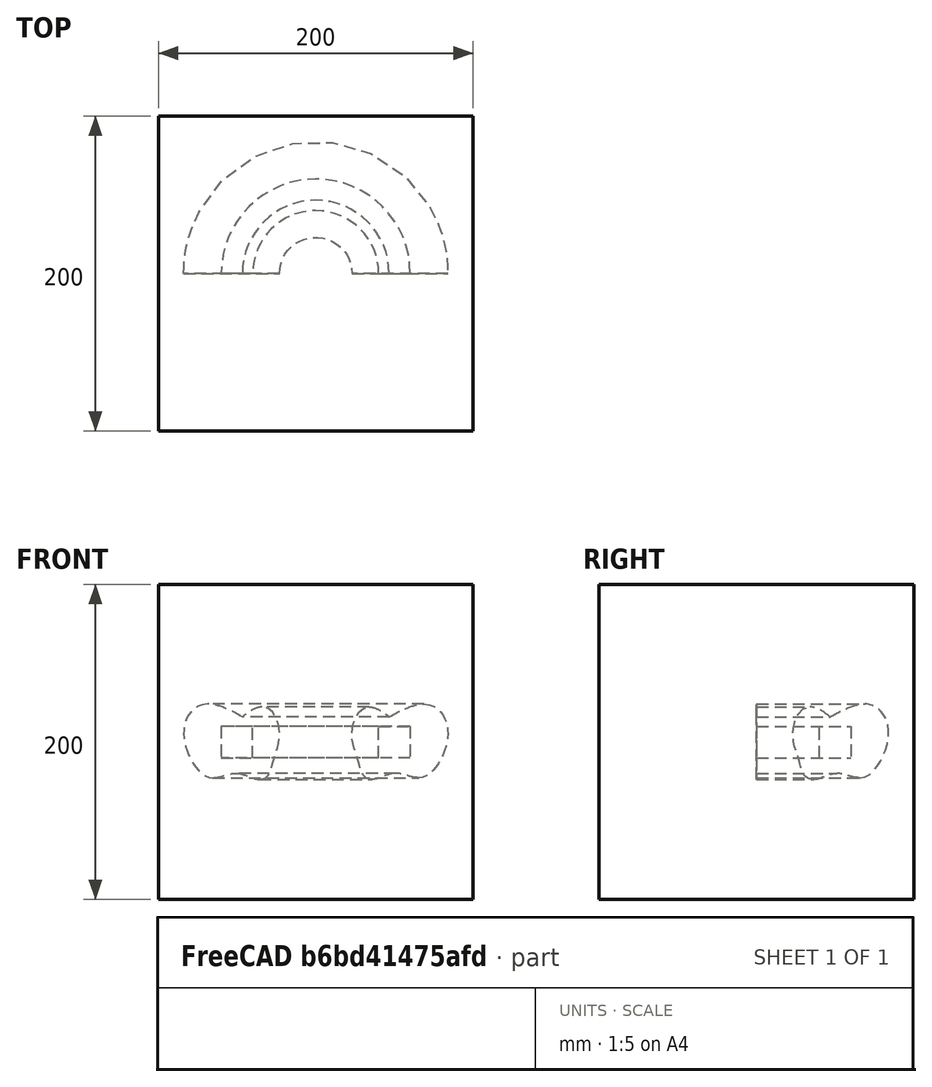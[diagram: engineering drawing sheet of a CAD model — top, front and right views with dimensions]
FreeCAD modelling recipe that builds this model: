
FCSTD DOCUMENT  (FreeCAD 0.21R33694 (Git))
Label: revolve
License: All rights reserved
LicenseURL: http://en.wikipedia.org/wiki/All_rights_reserved
objects: App::DocumentObjectGroupPython×1248, App::Part×2, Part::FeaturePython×1, Sketcher::SketchObject×1, Part::Revolution×1
note: 3 computed .brp shape members not serialized (recipe doc carries the construction recipe); baked Part::Feature solids carry a one-line shape summary decoded from their .brp

FEATURE [App::DocumentObjectGroupPython] HALFPI  # scripted group (container) (typed FeaturePython)
  name = HALFPI
  value = pi/2.
FEATURE [App::DocumentObjectGroupPython] PI  # scripted group (container) (typed FeaturePython)
  name = PI
  value = 1.*pi
FEATURE [App::DocumentObjectGroupPython] TWOPI  # scripted group (container) (typed FeaturePython)
  name = TWOPI
  value = 2.*pi
FEATURE [App::DocumentObjectGroupPython] Constants  # scripted group (container) (typed FeaturePython)
  Group = -> [HALFPI,PI,TWOPI]
FEATURE [App::DocumentObjectGroupPython] Variables  # scripted group (container) (typed FeaturePython)
FEATURE [App::DocumentObjectGroupPython] Quantities  # scripted group (container) (typed FeaturePython)
FEATURE [App::DocumentObjectGroupPython] Isotopes  # scripted group (container) (typed FeaturePython)
FEATURE [App::DocumentObjectGroupPython] Elements  # scripted group (container) (typed FeaturePython)
FEATURE [App::DocumentObjectGroupPython] G4Isotopes  # scripted group (container) (typed FeaturePython)
FEATURE [App::DocumentObjectGroupPython] H_element  # scripted group (container) (typed FeaturePython)
  Z = 1
  atom_value = 1.008
  formula = H
  name = H_element
FEATURE [App::DocumentObjectGroupPython] He_element  # scripted group (container) (typed FeaturePython)
  Z = 2
  atom_value = 4.0026
  formula = He
  name = He_element
FEATURE [App::DocumentObjectGroupPython] Li_element  # scripted group (container) (typed FeaturePython)
  Z = 3
  atom_value = 6.94
  formula = Li
  name = Li_element
FEATURE [App::DocumentObjectGroupPython] Be_element  # scripted group (container) (typed FeaturePython)
  Z = 4
  atom_value = 9.01218
  formula = Be
  name = Be_element
FEATURE [App::DocumentObjectGroupPython] B_element  # scripted group (container) (typed FeaturePython)
  Z = 5
  atom_value = 10.81
  formula = B
  name = B_element
FEATURE [App::DocumentObjectGroupPython] C_element  # scripted group (container) (typed FeaturePython)
  Z = 6
  atom_value = 12.011
  formula = C
  name = C_element
FEATURE [App::DocumentObjectGroupPython] N_element  # scripted group (container) (typed FeaturePython)
  Z = 7
  atom_value = 14.007
  formula = N
  name = N_element
FEATURE [App::DocumentObjectGroupPython] O_element  # scripted group (container) (typed FeaturePython)
  Z = 8
  atom_value = 15.999
  formula = O
  name = O_element
FEATURE [App::DocumentObjectGroupPython] F_element  # scripted group (container) (typed FeaturePython)
  Z = 9
  atom_value = 18.9984
  formula = F
  name = F_element
FEATURE [App::DocumentObjectGroupPython] Ne_element  # scripted group (container) (typed FeaturePython)
  Z = 10
  atom_value = 20.1797
  formula = Ne
  name = Ne_element
FEATURE [App::DocumentObjectGroupPython] Na_element  # scripted group (container) (typed FeaturePython)
  Z = 11
  atom_value = 22.9898
  formula = Na
  name = Na_element
FEATURE [App::DocumentObjectGroupPython] Mg_element  # scripted group (container) (typed FeaturePython)
  Z = 12
  atom_value = 24.305
  formula = Mg
  name = Mg_element
FEATURE [App::DocumentObjectGroupPython] Al_element  # scripted group (container) (typed FeaturePython)
  Z = 13
  atom_value = 26.9815
  formula = Al
  name = Al_element
FEATURE [App::DocumentObjectGroupPython] Si_element  # scripted group (container) (typed FeaturePython)
  Z = 14
  atom_value = 28.085
  formula = Si
  name = Si_element
FEATURE [App::DocumentObjectGroupPython] P_element  # scripted group (container) (typed FeaturePython)
  Z = 15
  atom_value = 30.9738
  formula = P
  name = P_element
FEATURE [App::DocumentObjectGroupPython] S_element  # scripted group (container) (typed FeaturePython)
  Z = 16
  atom_value = 32.06
  formula = S
  name = S_element
FEATURE [App::DocumentObjectGroupPython] Cl_element  # scripted group (container) (typed FeaturePython)
  Z = 17
  atom_value = 35.45
  formula = Cl
  name = Cl_element
FEATURE [App::DocumentObjectGroupPython] Ar_element  # scripted group (container) (typed FeaturePython)
  Z = 18
  atom_value = 39.95
  formula = Ar
  name = Ar_element
FEATURE [App::DocumentObjectGroupPython] K_element  # scripted group (container) (typed FeaturePython)
  Z = 19
  atom_value = 39.0983
  formula = K
  name = K_element
FEATURE [App::DocumentObjectGroupPython] Ca_element  # scripted group (container) (typed FeaturePython)
  Z = 20
  atom_value = 40.078
  formula = Ca
  name = Ca_element
FEATURE [App::DocumentObjectGroupPython] Sc_element  # scripted group (container) (typed FeaturePython)
  Z = 21
  atom_value = 44.9559
  formula = Sc
  name = Sc_element
FEATURE [App::DocumentObjectGroupPython] Ti_element  # scripted group (container) (typed FeaturePython)
  Z = 22
  atom_value = 47.867
  formula = Ti
  name = Ti_element
FEATURE [App::DocumentObjectGroupPython] V_element  # scripted group (container) (typed FeaturePython)
  Z = 23
  atom_value = 50.9415
  formula = V
  name = V_element
FEATURE [App::DocumentObjectGroupPython] Cr_element  # scripted group (container) (typed FeaturePython)
  Z = 24
  atom_value = 51.9961
  formula = Cr
  name = Cr_element
FEATURE [App::DocumentObjectGroupPython] Mn_element  # scripted group (container) (typed FeaturePython)
  Z = 25
  atom_value = 54.938
  formula = Mn
  name = Mn_element
FEATURE [App::DocumentObjectGroupPython] Fe_element  # scripted group (container) (typed FeaturePython)
  Z = 26
  atom_value = 55.845
  formula = Fe
  name = Fe_element
FEATURE [App::DocumentObjectGroupPython] Co_element  # scripted group (container) (typed FeaturePython)
  Z = 27
  atom_value = 58.9332
  formula = Co
  name = Co_element
FEATURE [App::DocumentObjectGroupPython] Ni_element  # scripted group (container) (typed FeaturePython)
  Z = 28
  atom_value = 58.6934
  formula = Ni
  name = Ni_element
FEATURE [App::DocumentObjectGroupPython] Cu_element  # scripted group (container) (typed FeaturePython)
  Z = 29
  atom_value = 63.546
  formula = Cu
  name = Cu_element
FEATURE [App::DocumentObjectGroupPython] Zn_element  # scripted group (container) (typed FeaturePython)
  Z = 30
  atom_value = 65.38
  formula = Zn
  name = Zn_element
FEATURE [App::DocumentObjectGroupPython] Ga_element  # scripted group (container) (typed FeaturePython)
  Z = 31
  atom_value = 69.723
  formula = Ga
  name = Ga_element
FEATURE [App::DocumentObjectGroupPython] Ge_element  # scripted group (container) (typed FeaturePython)
  Z = 32
  atom_value = 72.63
  formula = Ge
  name = Ge_element
FEATURE [App::DocumentObjectGroupPython] As_element  # scripted group (container) (typed FeaturePython)
  Z = 33
  atom_value = 74.9216
  formula = As
  name = As_element
FEATURE [App::DocumentObjectGroupPython] Se_element  # scripted group (container) (typed FeaturePython)
  Z = 34
  atom_value = 78.971
  formula = Se
  name = Se_element
FEATURE [App::DocumentObjectGroupPython] Br_element  # scripted group (container) (typed FeaturePython)
  Z = 35
  atom_value = 79.904
  formula = Br
  name = Br_element
FEATURE [App::DocumentObjectGroupPython] Kr_element  # scripted group (container) (typed FeaturePython)
  Z = 36
  atom_value = 83.798
  formula = Kr
  name = Kr_element
FEATURE [App::DocumentObjectGroupPython] Rb_element  # scripted group (container) (typed FeaturePython)
  Z = 37
  atom_value = 85.4678
  formula = Rb
  name = Rb_element
FEATURE [App::DocumentObjectGroupPython] Sr_element  # scripted group (container) (typed FeaturePython)
  Z = 38
  atom_value = 87.62
  formula = Sr
  name = Sr_element
FEATURE [App::DocumentObjectGroupPython] Y_element  # scripted group (container) (typed FeaturePython)
  Z = 39
  atom_value = 88.9058
  formula = Y
  name = Y_element
FEATURE [App::DocumentObjectGroupPython] Zr_element  # scripted group (container) (typed FeaturePython)
  Z = 40
  atom_value = 91.224
  formula = Zr
  name = Zr_element
FEATURE [App::DocumentObjectGroupPython] Nb_element  # scripted group (container) (typed FeaturePython)
  Z = 41
  atom_value = 92.9064
  formula = Nb
  name = Nb_element
FEATURE [App::DocumentObjectGroupPython] Mo_element  # scripted group (container) (typed FeaturePython)
  Z = 42
  atom_value = 95.95
  formula = Mo
  name = Mo_element
FEATURE [App::DocumentObjectGroupPython] Tc_element  # scripted group (container) (typed FeaturePython)
  Z = 43
  atom_value = 97
  formula = Tc
  name = Tc_element
FEATURE [App::DocumentObjectGroupPython] Ru_element  # scripted group (container) (typed FeaturePython)
  Z = 44
  atom_value = 101.07
  formula = Ru
  name = Ru_element
FEATURE [App::DocumentObjectGroupPython] Rh_element  # scripted group (container) (typed FeaturePython)
  Z = 45
  atom_value = 102.905
  formula = Rh
  name = Rh_element
FEATURE [App::DocumentObjectGroupPython] Pd_element  # scripted group (container) (typed FeaturePython)
  Z = 46
  atom_value = 106.42
  formula = Pd
  name = Pd_element
FEATURE [App::DocumentObjectGroupPython] Ag_element  # scripted group (container) (typed FeaturePython)
  Z = 47
  atom_value = 107.868
  formula = Ag
  name = Ag_element
FEATURE [App::DocumentObjectGroupPython] Cd_element  # scripted group (container) (typed FeaturePython)
  Z = 48
  atom_value = 112.414
  formula = Cd
  name = Cd_element
FEATURE [App::DocumentObjectGroupPython] In_element  # scripted group (container) (typed FeaturePython)
  Z = 49
  atom_value = 114.818
  formula = In
  name = In_element
FEATURE [App::DocumentObjectGroupPython] Sn_element  # scripted group (container) (typed FeaturePython)
  Z = 50
  atom_value = 118.71
  formula = Sn
  name = Sn_element
FEATURE [App::DocumentObjectGroupPython] Sb_element  # scripted group (container) (typed FeaturePython)
  Z = 51
  atom_value = 121.76
  formula = Sb
  name = Sb_element
FEATURE [App::DocumentObjectGroupPython] Te_element  # scripted group (container) (typed FeaturePython)
  Z = 52
  atom_value = 127.6
  formula = Te
  name = Te_element
FEATURE [App::DocumentObjectGroupPython] I_element  # scripted group (container) (typed FeaturePython)
  Z = 53
  atom_value = 126.904
  formula = I
  name = I_element
FEATURE [App::DocumentObjectGroupPython] Xe_element  # scripted group (container) (typed FeaturePython)
  Z = 54
  atom_value = 131.293
  formula = Xe
  name = Xe_element
FEATURE [App::DocumentObjectGroupPython] Cs_element  # scripted group (container) (typed FeaturePython)
  Z = 55
  atom_value = 132.905
  formula = Cs
  name = Cs_element
FEATURE [App::DocumentObjectGroupPython] Ba_element  # scripted group (container) (typed FeaturePython)
  Z = 56
  atom_value = 137.327
  formula = Ba
  name = Ba_element
FEATURE [App::DocumentObjectGroupPython] La_element  # scripted group (container) (typed FeaturePython)
  Z = 57
  atom_value = 138.905
  formula = La
  name = La_element
FEATURE [App::DocumentObjectGroupPython] Ce_element  # scripted group (container) (typed FeaturePython)
  Z = 58
  atom_value = 140.116
  formula = Ce
  name = Ce_element
FEATURE [App::DocumentObjectGroupPython] Pr_element  # scripted group (container) (typed FeaturePython)
  Z = 59
  atom_value = 140.908
  formula = Pr
  name = Pr_element
FEATURE [App::DocumentObjectGroupPython] Nd_element  # scripted group (container) (typed FeaturePython)
  Z = 60
  atom_value = 144.242
  formula = Nd
  name = Nd_element
FEATURE [App::DocumentObjectGroupPython] Pm_element  # scripted group (container) (typed FeaturePython)
  Z = 61
  atom_value = 145
  formula = Pm
  name = Pm_element
FEATURE [App::DocumentObjectGroupPython] Sm_element  # scripted group (container) (typed FeaturePython)
  Z = 62
  atom_value = 150.36
  formula = Sm
  name = Sm_element
FEATURE [App::DocumentObjectGroupPython] Eu_element  # scripted group (container) (typed FeaturePython)
  Z = 63
  atom_value = 151.964
  formula = Eu
  name = Eu_element
FEATURE [App::DocumentObjectGroupPython] Gd_element  # scripted group (container) (typed FeaturePython)
  Z = 64
  atom_value = 157.25
  formula = Gd
  name = Gd_element
FEATURE [App::DocumentObjectGroupPython] Tb_element  # scripted group (container) (typed FeaturePython)
  Z = 65
  atom_value = 158.925
  formula = Tb
  name = Tb_element
FEATURE [App::DocumentObjectGroupPython] Dy_element  # scripted group (container) (typed FeaturePython)
  Z = 66
  atom_value = 162.5
  formula = Dy
  name = Dy_element
FEATURE [App::DocumentObjectGroupPython] Ho_element  # scripted group (container) (typed FeaturePython)
  Z = 67
  atom_value = 164.93
  formula = Ho
  name = Ho_element
FEATURE [App::DocumentObjectGroupPython] Er_element  # scripted group (container) (typed FeaturePython)
  Z = 68
  atom_value = 167.259
  formula = Er
  name = Er_element
FEATURE [App::DocumentObjectGroupPython] Tm_element  # scripted group (container) (typed FeaturePython)
  Z = 69
  atom_value = 168.934
  formula = Tm
  name = Tm_element
FEATURE [App::DocumentObjectGroupPython] Yb_element  # scripted group (container) (typed FeaturePython)
  Z = 70
  atom_value = 173.045
  formula = Yb
  name = Yb_element
FEATURE [App::DocumentObjectGroupPython] Lu_element  # scripted group (container) (typed FeaturePython)
  Z = 71
  atom_value = 174.967
  formula = Lu
  name = Lu_element
FEATURE [App::DocumentObjectGroupPython] Hf_element  # scripted group (container) (typed FeaturePython)
  Z = 72
  atom_value = 178.49
  formula = Hf
  name = Hf_element
FEATURE [App::DocumentObjectGroupPython] Ta_element  # scripted group (container) (typed FeaturePython)
  Z = 73
  atom_value = 180.948
  formula = Ta
  name = Ta_element
FEATURE [App::DocumentObjectGroupPython] W_element  # scripted group (container) (typed FeaturePython)
  Z = 74
  atom_value = 183.84
  formula = W
  name = W_element
FEATURE [App::DocumentObjectGroupPython] Re_element  # scripted group (container) (typed FeaturePython)
  Z = 75
  atom_value = 186.207
  formula = Re
  name = Re_element
FEATURE [App::DocumentObjectGroupPython] Os_element  # scripted group (container) (typed FeaturePython)
  Z = 76
  atom_value = 190.23
  formula = Os
  name = Os_element
FEATURE [App::DocumentObjectGroupPython] Ir_element  # scripted group (container) (typed FeaturePython)
  Z = 77
  atom_value = 192.217
  formula = Ir
  name = Ir_element
FEATURE [App::DocumentObjectGroupPython] Pt_element  # scripted group (container) (typed FeaturePython)
  Z = 78
  atom_value = 195.084
  formula = Pt
  name = Pt_element
FEATURE [App::DocumentObjectGroupPython] Au_element  # scripted group (container) (typed FeaturePython)
  Z = 79
  atom_value = 196.967
  formula = Au
  name = Au_element
FEATURE [App::DocumentObjectGroupPython] Hg_element  # scripted group (container) (typed FeaturePython)
  Z = 80
  atom_value = 200.592
  formula = Hg
  name = Hg_element
FEATURE [App::DocumentObjectGroupPython] Tl_element  # scripted group (container) (typed FeaturePython)
  Z = 81
  atom_value = 204.38
  formula = Tl
  name = Tl_element
FEATURE [App::DocumentObjectGroupPython] Pb_element  # scripted group (container) (typed FeaturePython)
  Z = 82
  atom_value = 207.2
  formula = Pb
  name = Pb_element
FEATURE [App::DocumentObjectGroupPython] Bi_element  # scripted group (container) (typed FeaturePython)
  Z = 83
  atom_value = 208.98
  formula = Bi
  name = Bi_element
FEATURE [App::DocumentObjectGroupPython] Po_element  # scripted group (container) (typed FeaturePython)
  Z = 84
  atom_value = 209
  formula = Po
  name = Po_element
FEATURE [App::DocumentObjectGroupPython] At_element  # scripted group (container) (typed FeaturePython)
  Z = 85
  atom_value = 210
  formula = At
  name = At_element
FEATURE [App::DocumentObjectGroupPython] Rn_element  # scripted group (container) (typed FeaturePython)
  Z = 86
  atom_value = 222
  formula = Rn
  name = Rn_element
FEATURE [App::DocumentObjectGroupPython] Fr_element  # scripted group (container) (typed FeaturePython)
  Z = 87
  atom_value = 223
  formula = Fr
  name = Fr_element
FEATURE [App::DocumentObjectGroupPython] Ra_element  # scripted group (container) (typed FeaturePython)
  Z = 88
  atom_value = 226
  formula = Ra
  name = Ra_element
FEATURE [App::DocumentObjectGroupPython] Ac_element  # scripted group (container) (typed FeaturePython)
  Z = 89
  atom_value = 227
  formula = Ac
  name = Ac_element
FEATURE [App::DocumentObjectGroupPython] Th_element  # scripted group (container) (typed FeaturePython)
  Z = 90
  atom_value = 232.038
  formula = Th
  name = Th_element
FEATURE [App::DocumentObjectGroupPython] Pa_element  # scripted group (container) (typed FeaturePython)
  Z = 91
  atom_value = 231.036
  formula = Pa
  name = Pa_element
FEATURE [App::DocumentObjectGroupPython] U_element  # scripted group (container) (typed FeaturePython)
  Z = 92
  atom_value = 238.029
  formula = U
  name = U_element
FEATURE [App::DocumentObjectGroupPython] Np_element  # scripted group (container) (typed FeaturePython)
  Z = 93
  atom_value = 237
  formula = Np
  name = Np_element
FEATURE [App::DocumentObjectGroupPython] Pu_element  # scripted group (container) (typed FeaturePython)
  Z = 94
  atom_value = 244
  formula = Pu
  name = Pu_element
FEATURE [App::DocumentObjectGroupPython] Am_element  # scripted group (container) (typed FeaturePython)
  Z = 95
  atom_value = 243
  formula = Am
  name = Am_element
FEATURE [App::DocumentObjectGroupPython] Cm_element  # scripted group (container) (typed FeaturePython)
  Z = 96
  atom_value = 247
  formula = Cm
  name = Cm_element
FEATURE [App::DocumentObjectGroupPython] Bk_element  # scripted group (container) (typed FeaturePython)
  Z = 97
  atom_value = 247
  formula = Bk
  name = Bk_element
FEATURE [App::DocumentObjectGroupPython] Cf_element  # scripted group (container) (typed FeaturePython)
  Z = 98
  atom_value = 251
  formula = Cf
  name = Cf_element
FEATURE [App::DocumentObjectGroupPython] G4Elements  # scripted group (container) (typed FeaturePython)
  Group = -> [H_element,He_element,Li_element,Be_element,B_element,C_element,N_element,O_element,F_element,Ne_element,Na_element,Mg_element,Al_element,Si_element,P_element,S_element,Cl_element,Ar_element,K_element,Ca_element,Sc_element,Ti_element,V_element,Cr_element,Mn_element,Fe_element,Co_element,Ni_element,Cu_element,Zn_element,Ga_element,Ge_element,As_element,Se_element,Br_element,Kr_element,Rb_element,+61 more]
FEATURE [App::DocumentObjectGroupPython] H_element001  label="H_element : 0.101"  # scripted group (container) (typed FeaturePython)
  n = 0.101327
FEATURE [App::DocumentObjectGroupPython] C_element001  label="C_element : 0.775"  # scripted group (container) (typed FeaturePython)
  n = 0.7755
FEATURE [App::DocumentObjectGroupPython] N_element001  label="N_element : 0.035"  # scripted group (container) (typed FeaturePython)
  n = 0.035057
FEATURE [App::DocumentObjectGroupPython] O_element001  label="O_element : 0.052"  # scripted group (container) (typed FeaturePython)
  n = 0.0523159
FEATURE [App::DocumentObjectGroupPython] F_element001  label="F_element : 0.017"  # scripted group (container) (typed FeaturePython)
  n = 0.017422
FEATURE [App::DocumentObjectGroupPython] Ca_element001  label="Ca_element : 0.018"  # scripted group (container) (typed FeaturePython)
  n = 0.018378
FEATURE [App::DocumentObjectGroupPython] G4_A_150_TISSUE  label="G4_A-150_TISSUE"  # scripted group (container) (typed FeaturePython)
  Dunit = g/cm3
  Dvalue = 1.127
  Group = -> [H_element001,C_element001,N_element001,O_element001,F_element001,Ca_element001]
  conduct = 2
  density = 1
  expand = 3
  formula = G4_A-150_TISSUE
  name = G4_A-150_TISSUE
  specific = 4
FEATURE [App::DocumentObjectGroupPython] C_element002  label="C_element : 3"  # scripted group (container) (typed FeaturePython)
  n = 3
  ref = C_element
FEATURE [App::DocumentObjectGroupPython] H_element002  label="H_element : 6"  # scripted group (container) (typed FeaturePython)
  n = 6
  ref = H_element
FEATURE [App::DocumentObjectGroupPython] O_element002  label="O_element : 1"  # scripted group (container) (typed FeaturePython)
  n = 1
  ref = O_element
FEATURE [App::DocumentObjectGroupPython] G4_ACETONE  # scripted group (container) (typed FeaturePython)
  Dunit = g/cm3
  Dvalue = 0.7899
  Group = -> [C_element002,H_element002,O_element002]
  conduct = 2
  density = 1
  expand = 3
  formula = G4_ACETONE
  name = G4_ACETONE
  specific = 4
FEATURE [App::DocumentObjectGroupPython] C_element003  label="C_element : 2"  # scripted group (container) (typed FeaturePython)
  n = 2
  ref = C_element
FEATURE [App::DocumentObjectGroupPython] H_element003  label="H_element : 2"  # scripted group (container) (typed FeaturePython)
  n = 2
  ref = H_element
FEATURE [App::DocumentObjectGroupPython] G4_ACETYLENE  # scripted group (container) (typed FeaturePython)
  Dunit = g/cm3
  Dvalue = 0.0010967
  Group = -> [C_element003,H_element003]
  conduct = 2
  density = 1
  expand = 3
  formula = G4_ACETYLENE
  name = G4_ACETYLENE
  specific = 4
FEATURE [App::DocumentObjectGroupPython] C_element004  label="C_element : 5"  # scripted group (container) (typed FeaturePython)
  n = 5
  ref = C_element
FEATURE [App::DocumentObjectGroupPython] H_element004  label="H_element : 5"  # scripted group (container) (typed FeaturePython)
  n = 5
  ref = H_element
FEATURE [App::DocumentObjectGroupPython] N_element002  label="N_element : 5"  # scripted group (container) (typed FeaturePython)
  n = 5
  ref = N_element
FEATURE [App::DocumentObjectGroupPython] G4_ADENINE  # scripted group (container) (typed FeaturePython)
  Dunit = g/cm3
  Dvalue = 1.6
  Group = -> [C_element004,H_element004,N_element002]
  conduct = 2
  density = 1
  expand = 3
  formula = G4_ADENINE
  name = G4_ADENINE
  specific = 4
FEATURE [App::DocumentObjectGroupPython] H_element005  label="H_element : 0.114"  # scripted group (container) (typed FeaturePython)
  n = 0.114
FEATURE [App::DocumentObjectGroupPython] C_element005  label="C_element : 0.598"  # scripted group (container) (typed FeaturePython)
  n = 0.598
FEATURE [App::DocumentObjectGroupPython] N_element003  label="N_element : 0.007"  # scripted group (container) (typed FeaturePython)
  n = 0.007
FEATURE [App::DocumentObjectGroupPython] O_element003  label="O_element : 0.278"  # scripted group (container) (typed FeaturePython)
  n = 0.278
FEATURE [App::DocumentObjectGroupPython] Na_element001  label="Na_element : 0.001"  # scripted group (container) (typed FeaturePython)
  n = 0.001
FEATURE [App::DocumentObjectGroupPython] S_element001  label="S_element : 0.001"  # scripted group (container) (typed FeaturePython)
  n = 0.001
FEATURE [App::DocumentObjectGroupPython] Cl_element001  label="Cl_element : 0.001"  # scripted group (container) (typed FeaturePython)
  n = 0.001
FEATURE [App::DocumentObjectGroupPython] G4_ADIPOSE_TISSUE_ICRP  # scripted group (container) (typed FeaturePython)
  Dunit = g/cm3
  Dvalue = 0.95
  Group = -> [H_element005,C_element005,N_element003,O_element003,Na_element001,S_element001,Cl_element001]
  conduct = 2
  density = 1
  expand = 3
  formula = G4_ADIPOSE_TISSUE_ICRP
  name = G4_ADIPOSE_TISSUE_ICRP
  specific = 4
FEATURE [App::DocumentObjectGroupPython] C_element006  label="C_element : 0.000"  # scripted group (container) (typed FeaturePython)
  n = 0.000124
FEATURE [App::DocumentObjectGroupPython] N_element004  label="N_element : 0.755"  # scripted group (container) (typed FeaturePython)
  n = 0.755268
FEATURE [App::DocumentObjectGroupPython] O_element004  label="O_element : 0.232"  # scripted group (container) (typed FeaturePython)
  n = 0.231781
FEATURE [App::DocumentObjectGroupPython] Ar_element001  label="Ar_element : 0.013"  # scripted group (container) (typed FeaturePython)
  n = 0.012827
FEATURE [App::DocumentObjectGroupPython] G4_AIR  # scripted group (container) (typed FeaturePython)
  Dunit = g/cm3
  Dvalue = 0.00120479
  Group = -> [C_element006,N_element004,O_element004,Ar_element001]
  conduct = 2
  density = 1
  expand = 3
  formula = G4_AIR
  name = G4_AIR
  specific = 4
FEATURE [App::DocumentObjectGroupPython] C_element007  label="C_element : 006"  # scripted group (container) (typed FeaturePython)
  n = 3
  ref = C_element
FEATURE [App::DocumentObjectGroupPython] H_element006  label="H_element : 7"  # scripted group (container) (typed FeaturePython)
  n = 7
  ref = H_element
FEATURE [App::DocumentObjectGroupPython] N_element005  label="N_element : 1"  # scripted group (container) (typed FeaturePython)
  n = 1
  ref = N_element
FEATURE [App::DocumentObjectGroupPython] O_element005  label="O_element : 2"  # scripted group (container) (typed FeaturePython)
  n = 2
  ref = O_element
FEATURE [App::DocumentObjectGroupPython] G4_ALANINE  # scripted group (container) (typed FeaturePython)
  Dunit = g/cm3
  Dvalue = 1.42
  Group = -> [C_element007,H_element006,N_element005,O_element005]
  conduct = 2
  density = 1
  expand = 3
  formula = G4_ALANINE
  name = G4_ALANINE
  specific = 4
FEATURE [App::DocumentObjectGroupPython] Al_element001  label="Al_element : 2"  # scripted group (container) (typed FeaturePython)
  n = 2
  ref = Al_element
FEATURE [App::DocumentObjectGroupPython] O_element006  label="O_element : 3"  # scripted group (container) (typed FeaturePython)
  n = 3
  ref = O_element
FEATURE [App::DocumentObjectGroupPython] G4_ALUMINUM_OXIDE  # scripted group (container) (typed FeaturePython)
  Dunit = g/cm3
  Dvalue = 3.97
  Group = -> [Al_element001,O_element006]
  conduct = 2
  density = 1
  expand = 3
  formula = G4_ALUMINUM_OXIDE
  name = G4_ALUMINUM_OXIDE
  specific = 4
FEATURE [App::DocumentObjectGroupPython] H_element007  label="H_element : 0.106"  # scripted group (container) (typed FeaturePython)
  n = 0.10593
FEATURE [App::DocumentObjectGroupPython] C_element008  label="C_element : 0.789"  # scripted group (container) (typed FeaturePython)
  n = 0.788974
FEATURE [App::DocumentObjectGroupPython] O_element007  label="O_element : 0.105"  # scripted group (container) (typed FeaturePython)
  n = 0.105096
FEATURE [App::DocumentObjectGroupPython] G4_AMBER  # scripted group (container) (typed FeaturePython)
  Dunit = g/cm3
  Dvalue = 1.1
  Group = -> [H_element007,C_element008,O_element007]
  conduct = 2
  density = 1
  expand = 3
  formula = G4_AMBER
  name = G4_AMBER
  specific = 4
FEATURE [App::DocumentObjectGroupPython] N_element006  label="N_element : 006"  # scripted group (container) (typed FeaturePython)
  n = 1
  ref = N_element
FEATURE [App::DocumentObjectGroupPython] H_element008  label="H_element : 3"  # scripted group (container) (typed FeaturePython)
  n = 3
  ref = H_element
FEATURE [App::DocumentObjectGroupPython] G4_AMMONIA  # scripted group (container) (typed FeaturePython)
  Dunit = g/cm3
  Dvalue = 0.000826019
  Group = -> [N_element006,H_element008]
  conduct = 2
  density = 1
  expand = 3
  formula = G4_AMMONIA
  name = G4_AMMONIA
  specific = 4
FEATURE [App::DocumentObjectGroupPython] C_element009  label="C_element : 6"  # scripted group (container) (typed FeaturePython)
  n = 6
  ref = C_element
FEATURE [App::DocumentObjectGroupPython] H_element009  label="H_element : 008"  # scripted group (container) (typed FeaturePython)
  n = 7
  ref = H_element
FEATURE [App::DocumentObjectGroupPython] N_element007  label="N_element : 007"  # scripted group (container) (typed FeaturePython)
  n = 1
  ref = N_element
FEATURE [App::DocumentObjectGroupPython] G4_ANILINE  # scripted group (container) (typed FeaturePython)
  Dunit = g/cm3
  Dvalue = 1.0235
  Group = -> [C_element009,H_element009,N_element007]
  conduct = 2
  density = 1
  expand = 3
  formula = G4_ANILINE
  name = G4_ANILINE
  specific = 4
FEATURE [App::DocumentObjectGroupPython] C_element010  label="C_element : 14"  # scripted group (container) (typed FeaturePython)
  n = 14
  ref = C_element
FEATURE [App::DocumentObjectGroupPython] H_element010  label="H_element : 10"  # scripted group (container) (typed FeaturePython)
  n = 10
  ref = H_element
FEATURE [App::DocumentObjectGroupPython] G4_ANTHRACENE  # scripted group (container) (typed FeaturePython)
  Dunit = g/cm3
  Dvalue = 1.283
  Group = -> [C_element010,H_element010]
  conduct = 2
  density = 1
  expand = 3
  formula = G4_ANTHRACENE
  name = G4_ANTHRACENE
  specific = 4
FEATURE [App::DocumentObjectGroupPython] H_element011  label="H_element : 0.065"  # scripted group (container) (typed FeaturePython)
  n = 0.0654709
FEATURE [App::DocumentObjectGroupPython] C_element011  label="C_element : 0.537"  # scripted group (container) (typed FeaturePython)
  n = 0.536944
FEATURE [App::DocumentObjectGroupPython] N_element008  label="N_element : 0.021"  # scripted group (container) (typed FeaturePython)
  n = 0.0215
FEATURE [App::DocumentObjectGroupPython] O_element008  label="O_element : 0.032"  # scripted group (container) (typed FeaturePython)
  n = 0.032085
FEATURE [App::DocumentObjectGroupPython] F_element002  label="F_element : 0.167"  # scripted group (container) (typed FeaturePython)
  n = 0.167411
FEATURE [App::DocumentObjectGroupPython] Ca_element002  label="Ca_element : 0.177"  # scripted group (container) (typed FeaturePython)
  n = 0.176589
FEATURE [App::DocumentObjectGroupPython] G4_B_100_BONE  label="G4_B-100_BONE"  # scripted group (container) (typed FeaturePython)
  Dunit = g/cm3
  Dvalue = 1.45
  Group = -> [H_element011,C_element011,N_element008,O_element008,F_element002,Ca_element002]
  conduct = 2
  density = 1
  expand = 3
  formula = G4_B-100_BONE
  name = G4_B-100_BONE
  specific = 4
FEATURE [App::DocumentObjectGroupPython] H_element012  label="H_element : 0.057"  # scripted group (container) (typed FeaturePython)
  n = 0.057441
FEATURE [App::DocumentObjectGroupPython] C_element012  label="C_element : 0.790"  # scripted group (container) (typed FeaturePython)
  n = 0.774591
FEATURE [App::DocumentObjectGroupPython] O_element009  label="O_element : 0.168"  # scripted group (container) (typed FeaturePython)
  n = 0.167968
FEATURE [App::DocumentObjectGroupPython] G4_BAKELITE  # scripted group (container) (typed FeaturePython)
  Dunit = g/cm3
  Dvalue = 1.25
  Group = -> [H_element012,C_element012,O_element009]
  conduct = 2
  density = 1
  expand = 3
  formula = G4_BAKELITE
  name = G4_BAKELITE
  specific = 4
FEATURE [App::DocumentObjectGroupPython] Ba_element001  label="Ba_element : 1"  # scripted group (container) (typed FeaturePython)
  n = 1
  ref = Ba_element
FEATURE [App::DocumentObjectGroupPython] F_element003  label="F_element : 2"  # scripted group (container) (typed FeaturePython)
  n = 2
  ref = F_element
FEATURE [App::DocumentObjectGroupPython] G4_BARIUM_FLUORIDE  # scripted group (container) (typed FeaturePython)
  Dunit = g/cm3
  Dvalue = 4.89
  Group = -> [Ba_element001,F_element003]
  conduct = 2
  density = 1
  expand = 3
  formula = G4_BARIUM_FLUORIDE
  name = G4_BARIUM_FLUORIDE
  specific = 4
FEATURE [App::DocumentObjectGroupPython] Ba_element002  label="Ba_element : 002"  # scripted group (container) (typed FeaturePython)
  n = 1
  ref = Ba_element
FEATURE [App::DocumentObjectGroupPython] S_element002  label="S_element : 1"  # scripted group (container) (typed FeaturePython)
  n = 1
  ref = S_element
FEATURE [App::DocumentObjectGroupPython] O_element010  label="O_element : 4"  # scripted group (container) (typed FeaturePython)
  n = 4
  ref = O_element
FEATURE [App::DocumentObjectGroupPython] G4_BARIUM_SULFATE  # scripted group (container) (typed FeaturePython)
  Dunit = g/cm3
  Dvalue = 4.5
  Group = -> [Ba_element002,S_element002,O_element010]
  conduct = 2
  density = 1
  expand = 3
  formula = G4_BARIUM_SULFATE
  name = G4_BARIUM_SULFATE
  specific = 4
FEATURE [App::DocumentObjectGroupPython] C_element013  label="C_element : 007"  # scripted group (container) (typed FeaturePython)
  n = 6
  ref = C_element
FEATURE [App::DocumentObjectGroupPython] H_element013  label="H_element : 009"  # scripted group (container) (typed FeaturePython)
  n = 6
  ref = H_element
FEATURE [App::DocumentObjectGroupPython] G4_BENZENE  # scripted group (container) (typed FeaturePython)
  Dunit = g/cm3
  Dvalue = 0.87865
  Group = -> [C_element013,H_element013]
  conduct = 2
  density = 1
  expand = 3
  formula = G4_BENZENE
  name = G4_BENZENE
  specific = 4
FEATURE [App::DocumentObjectGroupPython] Be_element001  label="Be_element : 1"  # scripted group (container) (typed FeaturePython)
  n = 1
  ref = Be_element
FEATURE [App::DocumentObjectGroupPython] O_element011  label="O_element : 005"  # scripted group (container) (typed FeaturePython)
  n = 1
  ref = O_element
FEATURE [App::DocumentObjectGroupPython] G4_BERYLLIUM_OXIDE  # scripted group (container) (typed FeaturePython)
  Dunit = g/cm3
  Dvalue = 3.01
  Group = -> [Be_element001,O_element011]
  conduct = 2
  density = 1
  expand = 3
  formula = G4_BERYLLIUM_OXIDE
  name = G4_BERYLLIUM_OXIDE
  specific = 4
FEATURE [App::DocumentObjectGroupPython] Bi_element001  label="Bi_element : 4"  # scripted group (container) (typed FeaturePython)
  n = 4
  ref = Bi_element
FEATURE [App::DocumentObjectGroupPython] Ge_element001  label="Ge_element : 3"  # scripted group (container) (typed FeaturePython)
  n = 3
  ref = Ge_element
FEATURE [App::DocumentObjectGroupPython] O_element012  label="O_element : 12"  # scripted group (container) (typed FeaturePython)
  n = 12
  ref = O_element
FEATURE [App::DocumentObjectGroupPython] G4_BGO  # scripted group (container) (typed FeaturePython)
  Dunit = g/cm3
  Dvalue = 7.13
  Group = -> [Bi_element001,Ge_element001,O_element012]
  conduct = 2
  density = 1
  expand = 3
  formula = G4_BGO
  name = G4_BGO
  specific = 4
FEATURE [App::DocumentObjectGroupPython] H_element014  label="H_element : 0.102"  # scripted group (container) (typed FeaturePython)
  n = 0.102
FEATURE [App::DocumentObjectGroupPython] C_element014  label="C_element : 0.110"  # scripted group (container) (typed FeaturePython)
  n = 0.11
FEATURE [App::DocumentObjectGroupPython] N_element009  label="N_element : 0.033"  # scripted group (container) (typed FeaturePython)
  n = 0.033
FEATURE [App::DocumentObjectGroupPython] O_element013  label="O_element : 0.745"  # scripted group (container) (typed FeaturePython)
  n = 0.745
FEATURE [App::DocumentObjectGroupPython] Na_element002  label="Na_element : 0.002"  # scripted group (container) (typed FeaturePython)
  n = 0.001
FEATURE [App::DocumentObjectGroupPython] P_element001  label="P_element : 0.001"  # scripted group (container) (typed FeaturePython)
  n = 0.001
FEATURE [App::DocumentObjectGroupPython] S_element003  label="S_element : 0.002"  # scripted group (container) (typed FeaturePython)
  n = 0.002
FEATURE [App::DocumentObjectGroupPython] Cl_element002  label="Cl_element : 0.003"  # scripted group (container) (typed FeaturePython)
  n = 0.003
FEATURE [App::DocumentObjectGroupPython] K_element001  label="K_element : 0.002"  # scripted group (container) (typed FeaturePython)
  n = 0.002
FEATURE [App::DocumentObjectGroupPython] Fe_element001  label="Fe_element : 0.001"  # scripted group (container) (typed FeaturePython)
  n = 0.001
FEATURE [App::DocumentObjectGroupPython] G4_BLOOD_ICRP  # scripted group (container) (typed FeaturePython)
  Dunit = g/cm3
  Dvalue = 1.06
  Group = -> [H_element014,C_element014,N_element009,O_element013,Na_element002,P_element001,S_element003,Cl_element002,K_element001,Fe_element001]
  conduct = 2
  density = 1
  expand = 3
  formula = G4_BLOOD_ICRP
  name = G4_BLOOD_ICRP
  specific = 4
FEATURE [App::DocumentObjectGroupPython] H_element015  label="H_element : 0.064"  # scripted group (container) (typed FeaturePython)
  n = 0.064
FEATURE [App::DocumentObjectGroupPython] C_element015  label="C_element : 0.278"  # scripted group (container) (typed FeaturePython)
  n = 0.278
FEATURE [App::DocumentObjectGroupPython] N_element010  label="N_element : 0.027"  # scripted group (container) (typed FeaturePython)
  n = 0.027
FEATURE [App::DocumentObjectGroupPython] O_element014  label="O_element : 0.410"  # scripted group (container) (typed FeaturePython)
  n = 0.41
FEATURE [App::DocumentObjectGroupPython] Mg_element001  label="Mg_element : 0.002"  # scripted group (container) (typed FeaturePython)
  n = 0.002
FEATURE [App::DocumentObjectGroupPython] P_element002  label="P_element : 0.070"  # scripted group (container) (typed FeaturePython)
  n = 0.07
FEATURE [App::DocumentObjectGroupPython] S_element004  label="S_element : 0.003"  # scripted group (container) (typed FeaturePython)
  n = 0.002
FEATURE [App::DocumentObjectGroupPython] Ca_element003  label="Ca_element : 0.147"  # scripted group (container) (typed FeaturePython)
  n = 0.147
FEATURE [App::DocumentObjectGroupPython] G4_BONE_COMPACT_ICRU  # scripted group (container) (typed FeaturePython)
  Dunit = g/cm3
  Dvalue = 1.85
  Group = -> [H_element015,C_element015,N_element010,O_element014,Mg_element001,P_element002,S_element004,Ca_element003]
  conduct = 2
  density = 1
  expand = 3
  formula = G4_BONE_COMPACT_ICRU
  name = G4_BONE_COMPACT_ICRU
  specific = 4
FEATURE [App::DocumentObjectGroupPython] H_element016  label="H_element : 0.034"  # scripted group (container) (typed FeaturePython)
  n = 0.034
FEATURE [App::DocumentObjectGroupPython] C_element016  label="C_element : 0.155"  # scripted group (container) (typed FeaturePython)
  n = 0.155
FEATURE [App::DocumentObjectGroupPython] N_element011  label="N_element : 0.042"  # scripted group (container) (typed FeaturePython)
  n = 0.042
FEATURE [App::DocumentObjectGroupPython] O_element015  label="O_element : 0.435"  # scripted group (container) (typed FeaturePython)
  n = 0.435
FEATURE [App::DocumentObjectGroupPython] Na_element003  label="Na_element : 0.003"  # scripted group (container) (typed FeaturePython)
  n = 0.001
FEATURE [App::DocumentObjectGroupPython] Mg_element002  label="Mg_element : 0.003"  # scripted group (container) (typed FeaturePython)
  n = 0.002
FEATURE [App::DocumentObjectGroupPython] P_element003  label="P_element : 0.103"  # scripted group (container) (typed FeaturePython)
  n = 0.103
FEATURE [App::DocumentObjectGroupPython] S_element005  label="S_element : 0.004"  # scripted group (container) (typed FeaturePython)
  n = 0.003
FEATURE [App::DocumentObjectGroupPython] Ca_element004  label="Ca_element : 0.225"  # scripted group (container) (typed FeaturePython)
  n = 0.225
FEATURE [App::DocumentObjectGroupPython] G4_BONE_CORTICAL_ICRP  # scripted group (container) (typed FeaturePython)
  Dunit = g/cm3
  Dvalue = 1.92
  Group = -> [H_element016,C_element016,N_element011,O_element015,Na_element003,Mg_element002,P_element003,S_element005,Ca_element004]
  conduct = 2
  density = 1
  expand = 3
  formula = G4_BONE_CORTICAL_ICRP
  name = G4_BONE_CORTICAL_ICRP
  specific = 4
FEATURE [App::DocumentObjectGroupPython] B_element001  label="B_element : 4"  # scripted group (container) (typed FeaturePython)
  n = 4
  ref = B_element
FEATURE [App::DocumentObjectGroupPython] C_element017  label="C_element : 1"  # scripted group (container) (typed FeaturePython)
  n = 1
  ref = C_element
FEATURE [App::DocumentObjectGroupPython] G4_BORON_CARBIDE  # scripted group (container) (typed FeaturePython)
  Dunit = g/cm3
  Dvalue = 2.52
  Group = -> [B_element001,C_element017]
  conduct = 2
  density = 1
  expand = 3
  formula = G4_BORON_CARBIDE
  name = G4_BORON_CARBIDE
  specific = 4
FEATURE [App::DocumentObjectGroupPython] B_element002  label="B_element : 2"  # scripted group (container) (typed FeaturePython)
  n = 2
  ref = B_element
FEATURE [App::DocumentObjectGroupPython] O_element016  label="O_element : 006"  # scripted group (container) (typed FeaturePython)
  n = 3
  ref = O_element
FEATURE [App::DocumentObjectGroupPython] G4_BORON_OXIDE  # scripted group (container) (typed FeaturePython)
  Dunit = g/cm3
  Dvalue = 1.812
  Group = -> [B_element002,O_element016]
  conduct = 2
  density = 1
  expand = 3
  formula = G4_BORON_OXIDE
  name = G4_BORON_OXIDE
  specific = 4
FEATURE [App::DocumentObjectGroupPython] H_element017  label="H_element : 0.107"  # scripted group (container) (typed FeaturePython)
  n = 0.107
FEATURE [App::DocumentObjectGroupPython] C_element018  label="C_element : 0.145"  # scripted group (container) (typed FeaturePython)
  n = 0.145
FEATURE [App::DocumentObjectGroupPython] N_element012  label="N_element : 0.022"  # scripted group (container) (typed FeaturePython)
  n = 0.022
FEATURE [App::DocumentObjectGroupPython] O_element017  label="O_element : 0.712"  # scripted group (container) (typed FeaturePython)
  n = 0.712
FEATURE [App::DocumentObjectGroupPython] Na_element004  label="Na_element : 0.004"  # scripted group (container) (typed FeaturePython)
  n = 0.002
FEATURE [App::DocumentObjectGroupPython] P_element004  label="P_element : 0.004"  # scripted group (container) (typed FeaturePython)
  n = 0.004
FEATURE [App::DocumentObjectGroupPython] S_element006  label="S_element : 0.005"  # scripted group (container) (typed FeaturePython)
  n = 0.002
FEATURE [App::DocumentObjectGroupPython] Cl_element003  label="Cl_element : 0.004"  # scripted group (container) (typed FeaturePython)
  n = 0.003
FEATURE [App::DocumentObjectGroupPython] K_element002  label="K_element : 0.003"  # scripted group (container) (typed FeaturePython)
  n = 0.003
FEATURE [App::DocumentObjectGroupPython] G4_BRAIN_ICRP  # scripted group (container) (typed FeaturePython)
  Dunit = g/cm3
  Dvalue = 1.04
  Group = -> [H_element017,C_element018,N_element012,O_element017,Na_element004,P_element004,S_element006,Cl_element003,K_element002]
  conduct = 2
  density = 1
  expand = 3
  formula = G4_BRAIN_ICRP
  name = G4_BRAIN_ICRP
  specific = 4
FEATURE [App::DocumentObjectGroupPython] C_element019  label="C_element : 4"  # scripted group (container) (typed FeaturePython)
  n = 4
  ref = C_element
FEATURE [App::DocumentObjectGroupPython] H_element018  label="H_element : 010"  # scripted group (container) (typed FeaturePython)
  n = 10
  ref = H_element
FEATURE [App::DocumentObjectGroupPython] G4_BUTANE  # scripted group (container) (typed FeaturePython)
  Dunit = g/cm3
  Dvalue = 0.00249343
  Group = -> [C_element019,H_element018]
  conduct = 2
  density = 1
  expand = 3
  formula = G4_BUTANE
  name = G4_BUTANE
  specific = 4
FEATURE [App::DocumentObjectGroupPython] C_element020  label="C_element : 008"  # scripted group (container) (typed FeaturePython)
  n = 4
  ref = C_element
FEATURE [App::DocumentObjectGroupPython] H_element019  label="H_element : 011"  # scripted group (container) (typed FeaturePython)
  n = 10
  ref = H_element
FEATURE [App::DocumentObjectGroupPython] O_element018  label="O_element : 007"  # scripted group (container) (typed FeaturePython)
  n = 1
  ref = O_element
FEATURE [App::DocumentObjectGroupPython] G4_N_BUTYL_ALCOHOL  label="G4_N-BUTYL_ALCOHOL"  # scripted group (container) (typed FeaturePython)
  Dunit = g/cm3
  Dvalue = 0.8098
  Group = -> [C_element020,H_element019,O_element018]
  conduct = 2
  density = 1
  expand = 3
  formula = G4_N-BUTYL_ALCOHOL
  name = G4_N-BUTYL_ALCOHOL
  specific = 4
FEATURE [App::DocumentObjectGroupPython] H_element020  label="H_element : 0.025"  # scripted group (container) (typed FeaturePython)
  n = 0.02468
FEATURE [App::DocumentObjectGroupPython] C_element021  label="C_element : 0.502"  # scripted group (container) (typed FeaturePython)
  n = 0.501611
FEATURE [App::DocumentObjectGroupPython] O_element019  label="O_element : 0.005"  # scripted group (container) (typed FeaturePython)
  n = 0.004527
FEATURE [App::DocumentObjectGroupPython] F_element004  label="F_element : 0.465"  # scripted group (container) (typed FeaturePython)
  n = 0.465209
FEATURE [App::DocumentObjectGroupPython] Si_element001  label="Si_element : 0.004"  # scripted group (container) (typed FeaturePython)
  n = 0.003973
FEATURE [App::DocumentObjectGroupPython] G4_C_552  label="G4_C-552"  # scripted group (container) (typed FeaturePython)
  Dunit = g/cm3
  Dvalue = 1.76
  Group = -> [H_element020,C_element021,O_element019,F_element004,Si_element001]
  conduct = 2
  density = 1
  expand = 3
  formula = G4_C-552
  name = G4_C-552
  specific = 4
FEATURE [App::DocumentObjectGroupPython] Cd_element001  label="Cd_element : 1"  # scripted group (container) (typed FeaturePython)
  n = 1
  ref = Cd_element
FEATURE [App::DocumentObjectGroupPython] Te_element001  label="Te_element : 1"  # scripted group (container) (typed FeaturePython)
  n = 1
  ref = Te_element
FEATURE [App::DocumentObjectGroupPython] G4_CADMIUM_TELLURIDE  # scripted group (container) (typed FeaturePython)
  Dunit = g/cm3
  Dvalue = 6.2
  Group = -> [Cd_element001,Te_element001]
  conduct = 2
  density = 1
  expand = 3
  formula = G4_CADMIUM_TELLURIDE
  name = G4_CADMIUM_TELLURIDE
  specific = 4
FEATURE [App::DocumentObjectGroupPython] Cd_element002  label="Cd_element : 002"  # scripted group (container) (typed FeaturePython)
  n = 1
  ref = Cd_element
FEATURE [App::DocumentObjectGroupPython] W_element001  label="W_element : 1"  # scripted group (container) (typed FeaturePython)
  n = 1
  ref = W_element
FEATURE [App::DocumentObjectGroupPython] O_element020  label="O_element : 008"  # scripted group (container) (typed FeaturePython)
  n = 4
  ref = O_element
FEATURE [App::DocumentObjectGroupPython] G4_CADMIUM_TUNGSTATE  # scripted group (container) (typed FeaturePython)
  Dunit = g/cm3
  Dvalue = 7.9
  Group = -> [Cd_element002,W_element001,O_element020]
  conduct = 2
  density = 1
  expand = 3
  formula = G4_CADMIUM_TUNGSTATE
  name = G4_CADMIUM_TUNGSTATE
  specific = 4
FEATURE [App::DocumentObjectGroupPython] Ca_element005  label="Ca_element : 1"  # scripted group (container) (typed FeaturePython)
  n = 1
  ref = Ca_element
FEATURE [App::DocumentObjectGroupPython] C_element022  label="C_element : 009"  # scripted group (container) (typed FeaturePython)
  n = 1
  ref = C_element
FEATURE [App::DocumentObjectGroupPython] O_element021  label="O_element : 009"  # scripted group (container) (typed FeaturePython)
  n = 3
  ref = O_element
FEATURE [App::DocumentObjectGroupPython] G4_CALCIUM_CARBONATE  # scripted group (container) (typed FeaturePython)
  Dunit = g/cm3
  Dvalue = 2.8
  Group = -> [Ca_element005,C_element022,O_element021]
  conduct = 2
  density = 1
  expand = 3
  formula = G4_CALCIUM_CARBONATE
  name = G4_CALCIUM_CARBONATE
  specific = 4
FEATURE [App::DocumentObjectGroupPython] Ca_element006  label="Ca_element : 002"  # scripted group (container) (typed FeaturePython)
  n = 1
  ref = Ca_element
FEATURE [App::DocumentObjectGroupPython] F_element005  label="F_element : 003"  # scripted group (container) (typed FeaturePython)
  n = 2
  ref = F_element
FEATURE [App::DocumentObjectGroupPython] G4_CALCIUM_FLUORIDE  # scripted group (container) (typed FeaturePython)
  Dunit = g/cm3
  Dvalue = 3.18
  Group = -> [Ca_element006,F_element005]
  conduct = 2
  density = 1
  expand = 3
  formula = G4_CALCIUM_FLUORIDE
  name = G4_CALCIUM_FLUORIDE
  specific = 4
FEATURE [App::DocumentObjectGroupPython] Ca_element007  label="Ca_element : 003"  # scripted group (container) (typed FeaturePython)
  n = 1
  ref = Ca_element
FEATURE [App::DocumentObjectGroupPython] O_element022  label="O_element : 010"  # scripted group (container) (typed FeaturePython)
  n = 1
  ref = O_element
FEATURE [App::DocumentObjectGroupPython] G4_CALCIUM_OXIDE  # scripted group (container) (typed FeaturePython)
  Dunit = g/cm3
  Dvalue = 3.3
  Group = -> [Ca_element007,O_element022]
  conduct = 2
  density = 1
  expand = 3
  formula = G4_CALCIUM_OXIDE
  name = G4_CALCIUM_OXIDE
  specific = 4
FEATURE [App::DocumentObjectGroupPython] Ca_element008  label="Ca_element : 004"  # scripted group (container) (typed FeaturePython)
  n = 1
  ref = Ca_element
FEATURE [App::DocumentObjectGroupPython] S_element007  label="S_element : 002"  # scripted group (container) (typed FeaturePython)
  n = 1
  ref = S_element
FEATURE [App::DocumentObjectGroupPython] O_element023  label="O_element : 011"  # scripted group (container) (typed FeaturePython)
  n = 4
  ref = O_element
FEATURE [App::DocumentObjectGroupPython] G4_CALCIUM_SULFATE  # scripted group (container) (typed FeaturePython)
  Dunit = g/cm3
  Dvalue = 2.96
  Group = -> [Ca_element008,S_element007,O_element023]
  conduct = 2
  density = 1
  expand = 3
  formula = G4_CALCIUM_SULFATE
  name = G4_CALCIUM_SULFATE
  specific = 4
FEATURE [App::DocumentObjectGroupPython] Ca_element009  label="Ca_element : 005"  # scripted group (container) (typed FeaturePython)
  n = 1
  ref = Ca_element
FEATURE [App::DocumentObjectGroupPython] W_element002  label="W_element : 002"  # scripted group (container) (typed FeaturePython)
  n = 1
  ref = W_element
FEATURE [App::DocumentObjectGroupPython] O_element024  label="O_element : 012"  # scripted group (container) (typed FeaturePython)
  n = 4
  ref = O_element
FEATURE [App::DocumentObjectGroupPython] G4_CALCIUM_TUNGSTATE  # scripted group (container) (typed FeaturePython)
  Dunit = g/cm3
  Dvalue = 6.062
  Group = -> [Ca_element009,W_element002,O_element024]
  conduct = 2
  density = 1
  expand = 3
  formula = G4_CALCIUM_TUNGSTATE
  name = G4_CALCIUM_TUNGSTATE
  specific = 4
FEATURE [App::DocumentObjectGroupPython] C_element023  label="C_element : 010"  # scripted group (container) (typed FeaturePython)
  n = 1
  ref = C_element
FEATURE [App::DocumentObjectGroupPython] O_element025  label="O_element : 013"  # scripted group (container) (typed FeaturePython)
  n = 2
  ref = O_element
FEATURE [App::DocumentObjectGroupPython] G4_CARBON_DIOXIDE  # scripted group (container) (typed FeaturePython)
  Dunit = g/cm3
  Dvalue = 0.00184212
  Group = -> [C_element023,O_element025]
  conduct = 2
  density = 1
  expand = 3
  formula = G4_CARBON_DIOXIDE
  name = G4_CARBON_DIOXIDE
  specific = 4
FEATURE [App::DocumentObjectGroupPython] C_element024  label="C_element : 011"  # scripted group (container) (typed FeaturePython)
  n = 1
  ref = C_element
FEATURE [App::DocumentObjectGroupPython] Cl_element004  label="Cl_element : 4"  # scripted group (container) (typed FeaturePython)
  n = 4
  ref = Cl_element
FEATURE [App::DocumentObjectGroupPython] G4_CARBON_TETRACHLORIDE  # scripted group (container) (typed FeaturePython)
  Dunit = g/cm3
  Dvalue = 1.594
  Group = -> [C_element024,Cl_element004]
  conduct = 2
  density = 1
  expand = 3
  formula = G4_CARBON_TETRACHLORIDE
  name = G4_CARBON_TETRACHLORIDE
  specific = 4
FEATURE [App::DocumentObjectGroupPython] C_element025  label="C_element : 012"  # scripted group (container) (typed FeaturePython)
  n = 6
  ref = C_element
FEATURE [App::DocumentObjectGroupPython] H_element021  label="H_element : 012"  # scripted group (container) (typed FeaturePython)
  n = 10
  ref = H_element
FEATURE [App::DocumentObjectGroupPython] O_element026  label="O_element : 5"  # scripted group (container) (typed FeaturePython)
  n = 5
  ref = O_element
FEATURE [App::DocumentObjectGroupPython] G4_CELLULOSE_CELLOPHANE  # scripted group (container) (typed FeaturePython)
  Dunit = g/cm3
  Dvalue = 1.42
  Group = -> [C_element025,H_element021,O_element026]
  conduct = 2
  density = 1
  expand = 3
  formula = G4_CELLULOSE_CELLOPHANE
  name = G4_CELLULOSE_CELLOPHANE
  specific = 4
FEATURE [App::DocumentObjectGroupPython] H_element022  label="H_element : 0.067"  # scripted group (container) (typed FeaturePython)
  n = 0.067125
FEATURE [App::DocumentObjectGroupPython] C_element026  label="C_element : 0.545"  # scripted group (container) (typed FeaturePython)
  n = 0.545403
FEATURE [App::DocumentObjectGroupPython] O_element027  label="O_element : 0.387"  # scripted group (container) (typed FeaturePython)
  n = 0.387472
FEATURE [App::DocumentObjectGroupPython] G4_CELLULOSE_BUTYRATE  # scripted group (container) (typed FeaturePython)
  Dunit = g/cm3
  Dvalue = 1.2
  Group = -> [H_element022,C_element026,O_element027]
  conduct = 2
  density = 1
  expand = 3
  formula = G4_CELLULOSE_BUTYRATE
  name = G4_CELLULOSE_BUTYRATE
  specific = 4
FEATURE [App::DocumentObjectGroupPython] H_element023  label="H_element : 0.029"  # scripted group (container) (typed FeaturePython)
  n = 0.029216
FEATURE [App::DocumentObjectGroupPython] C_element027  label="C_element : 0.271"  # scripted group (container) (typed FeaturePython)
  n = 0.271296
FEATURE [App::DocumentObjectGroupPython] N_element013  label="N_element : 0.121"  # scripted group (container) (typed FeaturePython)
  n = 0.121276
FEATURE [App::DocumentObjectGroupPython] O_element028  label="O_element : 0.578"  # scripted group (container) (typed FeaturePython)
  n = 0.578212
FEATURE [App::DocumentObjectGroupPython] G4_CELLULOSE_NITRATE  # scripted group (container) (typed FeaturePython)
  Dunit = g/cm3
  Dvalue = 1.49
  Group = -> [H_element023,C_element027,N_element013,O_element028]
  conduct = 2
  density = 1
  expand = 3
  formula = G4_CELLULOSE_NITRATE
  name = G4_CELLULOSE_NITRATE
  specific = 4
FEATURE [App::DocumentObjectGroupPython] H_element024  label="H_element : 0.108"  # scripted group (container) (typed FeaturePython)
  n = 0.107596
FEATURE [App::DocumentObjectGroupPython] N_element014  label="N_element : 0.001"  # scripted group (container) (typed FeaturePython)
  n = 0.0008
FEATURE [App::DocumentObjectGroupPython] O_element029  label="O_element : 0.875"  # scripted group (container) (typed FeaturePython)
  n = 0.874976
FEATURE [App::DocumentObjectGroupPython] S_element008  label="S_element : 0.015"  # scripted group (container) (typed FeaturePython)
  n = 0.014627
FEATURE [App::DocumentObjectGroupPython] Ce_element001  label="Ce_element : 0.002"  # scripted group (container) (typed FeaturePython)
  n = 0.002001
FEATURE [App::DocumentObjectGroupPython] G4_CERIC_SULFATE  # scripted group (container) (typed FeaturePython)
  Dunit = g/cm3
  Dvalue = 1.03
  Group = -> [H_element024,N_element014,O_element029,S_element008,Ce_element001]
  conduct = 2
  density = 1
  expand = 3
  formula = G4_CERIC_SULFATE
  name = G4_CERIC_SULFATE
  specific = 4
FEATURE [App::DocumentObjectGroupPython] Cs_element001  label="Cs_element : 1"  # scripted group (container) (typed FeaturePython)
  n = 1
  ref = Cs_element
FEATURE [App::DocumentObjectGroupPython] F_element006  label="F_element : 1"  # scripted group (container) (typed FeaturePython)
  n = 1
  ref = F_element
FEATURE [App::DocumentObjectGroupPython] G4_CESIUM_FLUORIDE  # scripted group (container) (typed FeaturePython)
  Dunit = g/cm3
  Dvalue = 4.115
  Group = -> [Cs_element001,F_element006]
  conduct = 2
  density = 1
  expand = 3
  formula = G4_CESIUM_FLUORIDE
  name = G4_CESIUM_FLUORIDE
  specific = 4
FEATURE [App::DocumentObjectGroupPython] Cs_element002  label="Cs_element : 002"  # scripted group (container) (typed FeaturePython)
  n = 1
  ref = Cs_element
FEATURE [App::DocumentObjectGroupPython] I_element001  label="I_element : 1"  # scripted group (container) (typed FeaturePython)
  n = 1
  ref = I_element
FEATURE [App::DocumentObjectGroupPython] G4_CESIUM_IODIDE  # scripted group (container) (typed FeaturePython)
  Dunit = g/cm3
  Dvalue = 4.51
  Group = -> [Cs_element002,I_element001]
  conduct = 2
  density = 1
  expand = 3
  formula = G4_CESIUM_IODIDE
  name = G4_CESIUM_IODIDE
  specific = 4
FEATURE [App::DocumentObjectGroupPython] C_element028  label="C_element : 013"  # scripted group (container) (typed FeaturePython)
  n = 6
  ref = C_element
FEATURE [App::DocumentObjectGroupPython] H_element025  label="H_element : 013"  # scripted group (container) (typed FeaturePython)
  n = 5
  ref = H_element
FEATURE [App::DocumentObjectGroupPython] Cl_element005  label="Cl_element : 1"  # scripted group (container) (typed FeaturePython)
  n = 1
  ref = Cl_element
FEATURE [App::DocumentObjectGroupPython] G4_CHLOROBENZENE  # scripted group (container) (typed FeaturePython)
  Dunit = g/cm3
  Dvalue = 1.1058
  Group = -> [C_element028,H_element025,Cl_element005]
  conduct = 2
  density = 1
  expand = 3
  formula = G4_CHLOROBENZENE
  name = G4_CHLOROBENZENE
  specific = 4
FEATURE [App::DocumentObjectGroupPython] C_element029  label="C_element : 014"  # scripted group (container) (typed FeaturePython)
  n = 1
  ref = C_element
FEATURE [App::DocumentObjectGroupPython] H_element026  label="H_element : 1"  # scripted group (container) (typed FeaturePython)
  n = 1
  ref = H_element
FEATURE [App::DocumentObjectGroupPython] Cl_element006  label="Cl_element : 3"  # scripted group (container) (typed FeaturePython)
  n = 3
  ref = Cl_element
FEATURE [App::DocumentObjectGroupPython] G4_CHLOROFORM  # scripted group (container) (typed FeaturePython)
  Dunit = g/cm3
  Dvalue = 1.4832
  Group = -> [C_element029,H_element026,Cl_element006]
  conduct = 2
  density = 1
  expand = 3
  formula = G4_CHLOROFORM
  name = G4_CHLOROFORM
  specific = 4
FEATURE [App::DocumentObjectGroupPython] H_element027  label="H_element : 0.010"  # scripted group (container) (typed FeaturePython)
  n = 0.01
FEATURE [App::DocumentObjectGroupPython] C_element030  label="C_element : 0.001"  # scripted group (container) (typed FeaturePython)
  n = 0.001
FEATURE [App::DocumentObjectGroupPython] O_element030  label="O_element : 0.529"  # scripted group (container) (typed FeaturePython)
  n = 0.529107
FEATURE [App::DocumentObjectGroupPython] Na_element005  label="Na_element : 0.016"  # scripted group (container) (typed FeaturePython)
  n = 0.016
FEATURE [App::DocumentObjectGroupPython] Mg_element003  label="Mg_element : 0.004"  # scripted group (container) (typed FeaturePython)
  n = 0.002
FEATURE [App::DocumentObjectGroupPython] Al_element002  label="Al_element : 0.034"  # scripted group (container) (typed FeaturePython)
  n = 0.033872
FEATURE [App::DocumentObjectGroupPython] Si_element002  label="Si_element : 0.337"  # scripted group (container) (typed FeaturePython)
  n = 0.337021
FEATURE [App::DocumentObjectGroupPython] K_element003  label="K_element : 0.013"  # scripted group (container) (typed FeaturePython)
  n = 0.013
FEATURE [App::DocumentObjectGroupPython] Ca_element010  label="Ca_element : 0.044"  # scripted group (container) (typed FeaturePython)
  n = 0.044
FEATURE [App::DocumentObjectGroupPython] Fe_element002  label="Fe_element : 0.014"  # scripted group (container) (typed FeaturePython)
  n = 0.014
FEATURE [App::DocumentObjectGroupPython] G4_CONCRETE  # scripted group (container) (typed FeaturePython)
  Dunit = g/cm3
  Dvalue = 2.3
  Group = -> [H_element027,C_element030,O_element030,Na_element005,Mg_element003,Al_element002,Si_element002,K_element003,Ca_element010,Fe_element002]
  conduct = 2
  density = 1
  expand = 3
  formula = G4_CONCRETE
  name = G4_CONCRETE
  specific = 4
FEATURE [App::DocumentObjectGroupPython] C_element031  label="C_element : 015"  # scripted group (container) (typed FeaturePython)
  n = 6
  ref = C_element
FEATURE [App::DocumentObjectGroupPython] H_element028  label="H_element : 12"  # scripted group (container) (typed FeaturePython)
  n = 12
  ref = H_element
FEATURE [App::DocumentObjectGroupPython] G4_CYCLOHEXANE  # scripted group (container) (typed FeaturePython)
  Dunit = g/cm3
  Dvalue = 0.779
  Group = -> [C_element031,H_element028]
  conduct = 2
  density = 1
  expand = 3
  formula = G4_CYCLOHEXANE
  name = G4_CYCLOHEXANE
  specific = 4
FEATURE [App::DocumentObjectGroupPython] C_element032  label="C_element : 016"  # scripted group (container) (typed FeaturePython)
  n = 6
  ref = C_element
FEATURE [App::DocumentObjectGroupPython] H_element029  label="H_element : 4"  # scripted group (container) (typed FeaturePython)
  n = 4
  ref = H_element
FEATURE [App::DocumentObjectGroupPython] Cl_element007  label="Cl_element : 2"  # scripted group (container) (typed FeaturePython)
  n = 2
  ref = Cl_element
FEATURE [App::DocumentObjectGroupPython] G4_1_2_DICHLOROBENZENE  label="G4_1.2-DICHLOROBENZENE"  # scripted group (container) (typed FeaturePython)
  Dunit = g/cm3
  Dvalue = 1.3048
  Group = -> [C_element032,H_element029,Cl_element007]
  conduct = 2
  density = 1
  expand = 3
  formula = G4_1.2-DICHLOROBENZENE
  name = G4_1.2-DICHLOROBENZENE
  specific = 4
FEATURE [App::DocumentObjectGroupPython] C_element033  label="C_element : 017"  # scripted group (container) (typed FeaturePython)
  n = 4
  ref = C_element
FEATURE [App::DocumentObjectGroupPython] H_element030  label="H_element : 8"  # scripted group (container) (typed FeaturePython)
  n = 8
  ref = H_element
FEATURE [App::DocumentObjectGroupPython] O_element031  label="O_element : 014"  # scripted group (container) (typed FeaturePython)
  n = 1
  ref = O_element
FEATURE [App::DocumentObjectGroupPython] Cl_element008  label="Cl_element : 005"  # scripted group (container) (typed FeaturePython)
  n = 2
  ref = Cl_element
FEATURE [App::DocumentObjectGroupPython] G4_DICHLORODIETHYL_ETHER  # scripted group (container) (typed FeaturePython)
  Dunit = g/cm3
  Dvalue = 1.2199
  Group = -> [C_element033,H_element030,O_element031,Cl_element008]
  conduct = 2
  density = 1
  expand = 3
  formula = G4_DICHLORODIETHYL_ETHER
  name = G4_DICHLORODIETHYL_ETHER
  specific = 4
FEATURE [App::DocumentObjectGroupPython] C_element034  label="C_element : 018"  # scripted group (container) (typed FeaturePython)
  n = 2
  ref = C_element
FEATURE [App::DocumentObjectGroupPython] H_element031  label="H_element : 014"  # scripted group (container) (typed FeaturePython)
  n = 4
  ref = H_element
FEATURE [App::DocumentObjectGroupPython] Cl_element009  label="Cl_element : 006"  # scripted group (container) (typed FeaturePython)
  n = 2
  ref = Cl_element
FEATURE [App::DocumentObjectGroupPython] G4_1_2_DICHLOROETHANE  label="G4_1.2-DICHLOROETHANE"  # scripted group (container) (typed FeaturePython)
  Dunit = g/cm3
  Dvalue = 1.2351
  Group = -> [C_element034,H_element031,Cl_element009]
  conduct = 2
  density = 1
  expand = 3
  formula = G4_1.2-DICHLOROETHANE
  name = G4_1.2-DICHLOROETHANE
  specific = 4
FEATURE [App::DocumentObjectGroupPython] C_element035  label="C_element : 019"  # scripted group (container) (typed FeaturePython)
  n = 4
  ref = C_element
FEATURE [App::DocumentObjectGroupPython] H_element032  label="H_element : 015"  # scripted group (container) (typed FeaturePython)
  n = 10
  ref = H_element
FEATURE [App::DocumentObjectGroupPython] O_element032  label="O_element : 015"  # scripted group (container) (typed FeaturePython)
  n = 1
  ref = O_element
FEATURE [App::DocumentObjectGroupPython] G4_DIETHYL_ETHER  # scripted group (container) (typed FeaturePython)
  Dunit = g/cm3
  Dvalue = 0.71378
  Group = -> [C_element035,H_element032,O_element032]
  conduct = 2
  density = 1
  expand = 3
  formula = G4_DIETHYL_ETHER
  name = G4_DIETHYL_ETHER
  specific = 4
FEATURE [App::DocumentObjectGroupPython] C_element036  label="C_element : 020"  # scripted group (container) (typed FeaturePython)
  n = 3
  ref = C_element
FEATURE [App::DocumentObjectGroupPython] H_element033  label="H_element : 016"  # scripted group (container) (typed FeaturePython)
  n = 7
  ref = H_element
FEATURE [App::DocumentObjectGroupPython] N_element015  label="N_element : 008"  # scripted group (container) (typed FeaturePython)
  n = 1
  ref = N_element
FEATURE [App::DocumentObjectGroupPython] O_element033  label="O_element : 016"  # scripted group (container) (typed FeaturePython)
  n = 1
  ref = O_element
FEATURE [App::DocumentObjectGroupPython] G4_N_N_DIMETHYL_FORMAMIDE  label="G4_N.N-DIMETHYL_FORMAMIDE"  # scripted group (container) (typed FeaturePython)
  Dunit = g/cm3
  Dvalue = 0.9487
  Group = -> [C_element036,H_element033,N_element015,O_element033]
  conduct = 2
  density = 1
  expand = 3
  formula = G4_N.N-DIMETHYL_FORMAMIDE
  name = G4_N.N-DIMETHYL_FORMAMIDE
  specific = 4
FEATURE [App::DocumentObjectGroupPython] C_element037  label="C_element : 021"  # scripted group (container) (typed FeaturePython)
  n = 2
  ref = C_element
FEATURE [App::DocumentObjectGroupPython] H_element034  label="H_element : 017"  # scripted group (container) (typed FeaturePython)
  n = 6
  ref = H_element
FEATURE [App::DocumentObjectGroupPython] O_element034  label="O_element : 017"  # scripted group (container) (typed FeaturePython)
  n = 1
  ref = O_element
FEATURE [App::DocumentObjectGroupPython] S_element009  label="S_element : 003"  # scripted group (container) (typed FeaturePython)
  n = 1
  ref = S_element
FEATURE [App::DocumentObjectGroupPython] G4_DIMETHYL_SULFOXIDE  # scripted group (container) (typed FeaturePython)
  Dunit = g/cm3
  Dvalue = 1.1014
  Group = -> [C_element037,H_element034,O_element034,S_element009]
  conduct = 2
  density = 1
  expand = 3
  formula = G4_DIMETHYL_SULFOXIDE
  name = G4_DIMETHYL_SULFOXIDE
  specific = 4
FEATURE [App::DocumentObjectGroupPython] C_element038  label="C_element : 022"  # scripted group (container) (typed FeaturePython)
  n = 2
  ref = C_element
FEATURE [App::DocumentObjectGroupPython] H_element035  label="H_element : 018"  # scripted group (container) (typed FeaturePython)
  n = 6
  ref = H_element
FEATURE [App::DocumentObjectGroupPython] G4_ETHANE  # scripted group (container) (typed FeaturePython)
  Dunit = g/cm3
  Dvalue = 0.00125324
  Group = -> [C_element038,H_element035]
  conduct = 2
  density = 1
  expand = 3
  formula = G4_ETHANE
  name = G4_ETHANE
  specific = 4
FEATURE [App::DocumentObjectGroupPython] C_element039  label="C_element : 023"  # scripted group (container) (typed FeaturePython)
  n = 2
  ref = C_element
FEATURE [App::DocumentObjectGroupPython] H_element036  label="H_element : 019"  # scripted group (container) (typed FeaturePython)
  n = 6
  ref = H_element
FEATURE [App::DocumentObjectGroupPython] O_element035  label="O_element : 018"  # scripted group (container) (typed FeaturePython)
  n = 1
  ref = O_element
FEATURE [App::DocumentObjectGroupPython] G4_ETHYL_ALCOHOL  # scripted group (container) (typed FeaturePython)
  Dunit = g/cm3
  Dvalue = 0.7893
  Group = -> [C_element039,H_element036,O_element035]
  conduct = 2
  density = 1
  expand = 3
  formula = G4_ETHYL_ALCOHOL
  name = G4_ETHYL_ALCOHOL
  specific = 4
FEATURE [App::DocumentObjectGroupPython] H_element037  label="H_element : 0.090"  # scripted group (container) (typed FeaturePython)
  n = 0.090027
FEATURE [App::DocumentObjectGroupPython] C_element040  label="C_element : 0.585"  # scripted group (container) (typed FeaturePython)
  n = 0.585182
FEATURE [App::DocumentObjectGroupPython] O_element036  label="O_element : 0.325"  # scripted group (container) (typed FeaturePython)
  n = 0.324791
FEATURE [App::DocumentObjectGroupPython] G4_ETHYL_CELLULOSE  # scripted group (container) (typed FeaturePython)
  Dunit = g/cm3
  Dvalue = 1.13
  Group = -> [H_element037,C_element040,O_element036]
  conduct = 2
  density = 1
  expand = 3
  formula = G4_ETHYL_CELLULOSE
  name = G4_ETHYL_CELLULOSE
  specific = 4
FEATURE [App::DocumentObjectGroupPython] C_element041  label="C_element : 024"  # scripted group (container) (typed FeaturePython)
  n = 2
  ref = C_element
FEATURE [App::DocumentObjectGroupPython] H_element038  label="H_element : 020"  # scripted group (container) (typed FeaturePython)
  n = 4
  ref = H_element
FEATURE [App::DocumentObjectGroupPython] G4_ETHYLENE  # scripted group (container) (typed FeaturePython)
  Dunit = g/cm3
  Dvalue = 0.00117497
  Group = -> [C_element041,H_element038]
  conduct = 2
  density = 1
  expand = 3
  formula = G4_ETHYLENE
  name = G4_ETHYLENE
  specific = 4
FEATURE [App::DocumentObjectGroupPython] H_element039  label="H_element : 0.096"  # scripted group (container) (typed FeaturePython)
  n = 0.096
FEATURE [App::DocumentObjectGroupPython] C_element042  label="C_element : 0.195"  # scripted group (container) (typed FeaturePython)
  n = 0.195
FEATURE [App::DocumentObjectGroupPython] N_element016  label="N_element : 0.057"  # scripted group (container) (typed FeaturePython)
  n = 0.057
FEATURE [App::DocumentObjectGroupPython] O_element037  label="O_element : 0.646"  # scripted group (container) (typed FeaturePython)
  n = 0.646
FEATURE [App::DocumentObjectGroupPython] Na_element006  label="Na_element : 0.017"  # scripted group (container) (typed FeaturePython)
  n = 0.001
FEATURE [App::DocumentObjectGroupPython] P_element005  label="P_element : 0.104"  # scripted group (container) (typed FeaturePython)
  n = 0.001
FEATURE [App::DocumentObjectGroupPython] S_element010  label="S_element : 0.016"  # scripted group (container) (typed FeaturePython)
  n = 0.003
FEATURE [App::DocumentObjectGroupPython] Cl_element010  label="Cl_element : 0.005"  # scripted group (container) (typed FeaturePython)
  n = 0.001
FEATURE [App::DocumentObjectGroupPython] G4_EYE_LENS_ICRP  # scripted group (container) (typed FeaturePython)
  Dunit = g/cm3
  Dvalue = 1.07
  Group = -> [H_element039,C_element042,N_element016,O_element037,Na_element006,P_element005,S_element010,Cl_element010]
  conduct = 2
  density = 1
  expand = 3
  formula = G4_EYE_LENS_ICRP
  name = G4_EYE_LENS_ICRP
  specific = 4
FEATURE [App::DocumentObjectGroupPython] Fe_element003  label="Fe_element : 2"  # scripted group (container) (typed FeaturePython)
  n = 2
  ref = Fe_element
FEATURE [App::DocumentObjectGroupPython] O_element038  label="O_element : 019"  # scripted group (container) (typed FeaturePython)
  n = 3
  ref = O_element
FEATURE [App::DocumentObjectGroupPython] G4_FERRIC_OXIDE  # scripted group (container) (typed FeaturePython)
  Dunit = g/cm3
  Dvalue = 5.2
  Group = -> [Fe_element003,O_element038]
  conduct = 2
  density = 1
  expand = 3
  formula = G4_FERRIC_OXIDE
  name = G4_FERRIC_OXIDE
  specific = 4
FEATURE [App::DocumentObjectGroupPython] Fe_element004  label="Fe_element : 1"  # scripted group (container) (typed FeaturePython)
  n = 1
  ref = Fe_element
FEATURE [App::DocumentObjectGroupPython] B_element003  label="B_element : 1"  # scripted group (container) (typed FeaturePython)
  n = 1
  ref = B_element
FEATURE [App::DocumentObjectGroupPython] G4_FERROBORIDE  # scripted group (container) (typed FeaturePython)
  Dunit = g/cm3
  Dvalue = 7.15
  Group = -> [Fe_element004,B_element003]
  conduct = 2
  density = 1
  expand = 3
  formula = G4_FERROBORIDE
  name = G4_FERROBORIDE
  specific = 4
FEATURE [App::DocumentObjectGroupPython] Fe_element005  label="Fe_element : 003"  # scripted group (container) (typed FeaturePython)
  n = 1
  ref = Fe_element
FEATURE [App::DocumentObjectGroupPython] O_element039  label="O_element : 020"  # scripted group (container) (typed FeaturePython)
  n = 1
  ref = O_element
FEATURE [App::DocumentObjectGroupPython] G4_FERROUS_OXIDE  # scripted group (container) (typed FeaturePython)
  Dunit = g/cm3
  Dvalue = 5.7
  Group = -> [Fe_element005,O_element039]
  conduct = 2
  density = 1
  expand = 3
  formula = G4_FERROUS_OXIDE
  name = G4_FERROUS_OXIDE
  specific = 4
FEATURE [App::DocumentObjectGroupPython] H_element040  label="H_element : 0.115"  # scripted group (container) (typed FeaturePython)
  n = 0.108259
FEATURE [App::DocumentObjectGroupPython] N_element017  label="N_element : 0.000"  # scripted group (container) (typed FeaturePython)
  n = 2.7e-05
FEATURE [App::DocumentObjectGroupPython] O_element040  label="O_element : 0.879"  # scripted group (container) (typed FeaturePython)
  n = 0.878636
FEATURE [App::DocumentObjectGroupPython] Na_element007  label="Na_element : 0.000"  # scripted group (container) (typed FeaturePython)
  n = 2.2e-05
FEATURE [App::DocumentObjectGroupPython] S_element011  label="S_element : 0.013"  # scripted group (container) (typed FeaturePython)
  n = 0.012968
FEATURE [App::DocumentObjectGroupPython] Cl_element011  label="Cl_element : 0.000"  # scripted group (container) (typed FeaturePython)
  n = 3.4e-05
FEATURE [App::DocumentObjectGroupPython] Fe_element006  label="Fe_element : 0.000"  # scripted group (container) (typed FeaturePython)
  n = 5.4e-05
FEATURE [App::DocumentObjectGroupPython] G4_FERROUS_SULFATE  # scripted group (container) (typed FeaturePython)
  Dunit = g/cm3
  Dvalue = 1.024
  Group = -> [H_element040,N_element017,O_element040,Na_element007,S_element011,Cl_element011,Fe_element006]
  conduct = 2
  density = 1
  expand = 3
  formula = G4_FERROUS_SULFATE
  name = G4_FERROUS_SULFATE
  specific = 4
FEATURE [App::DocumentObjectGroupPython] C_element043  label="C_element : 0.099"  # scripted group (container) (typed FeaturePython)
  n = 0.099335
FEATURE [App::DocumentObjectGroupPython] F_element007  label="F_element : 0.314"  # scripted group (container) (typed FeaturePython)
  n = 0.314247
FEATURE [App::DocumentObjectGroupPython] Cl_element012  label="Cl_element : 0.586"  # scripted group (container) (typed FeaturePython)
  n = 0.586418
FEATURE [App::DocumentObjectGroupPython] G4_FREON_12  label="G4_FREON-12"  # scripted group (container) (typed FeaturePython)
  Dunit = g/cm3
  Dvalue = 1.12
  Group = -> [C_element043,F_element007,Cl_element012]
  conduct = 2
  density = 1
  expand = 3
  formula = G4_FREON-12
  name = G4_FREON-12
  specific = 4
FEATURE [App::DocumentObjectGroupPython] C_element044  label="C_element : 0.057"  # scripted group (container) (typed FeaturePython)
  n = 0.057245
FEATURE [App::DocumentObjectGroupPython] F_element008  label="F_element : 0.181"  # scripted group (container) (typed FeaturePython)
  n = 0.181096
FEATURE [App::DocumentObjectGroupPython] Br_element001  label="Br_element : 0.762"  # scripted group (container) (typed FeaturePython)
  n = 0.761659
FEATURE [App::DocumentObjectGroupPython] G4_FREON_12B2  label="G4_FREON-12B2"  # scripted group (container) (typed FeaturePython)
  Dunit = g/cm3
  Dvalue = 1.8
  Group = -> [C_element044,F_element008,Br_element001]
  conduct = 2
  density = 1
  expand = 3
  formula = G4_FREON-12B2
  name = G4_FREON-12B2
  specific = 4
FEATURE [App::DocumentObjectGroupPython] C_element045  label="C_element : 0.115"  # scripted group (container) (typed FeaturePython)
  n = 0.114983
FEATURE [App::DocumentObjectGroupPython] F_element009  label="F_element : 0.546"  # scripted group (container) (typed FeaturePython)
  n = 0.545621
FEATURE [App::DocumentObjectGroupPython] Cl_element013  label="Cl_element : 0.339"  # scripted group (container) (typed FeaturePython)
  n = 0.339396
FEATURE [App::DocumentObjectGroupPython] G4_FREON_13  label="G4_FREON-13"  # scripted group (container) (typed FeaturePython)
  Dunit = g/cm3
  Dvalue = 0.95
  Group = -> [C_element045,F_element009,Cl_element013]
  conduct = 2
  density = 1
  expand = 3
  formula = G4_FREON-13
  name = G4_FREON-13
  specific = 4
FEATURE [App::DocumentObjectGroupPython] C_element046  label="C_element : 025"  # scripted group (container) (typed FeaturePython)
  n = 1
  ref = C_element
FEATURE [App::DocumentObjectGroupPython] F_element010  label="F_element : 3"  # scripted group (container) (typed FeaturePython)
  n = 3
  ref = F_element
FEATURE [App::DocumentObjectGroupPython] Br_element002  label="Br_element : 1"  # scripted group (container) (typed FeaturePython)
  n = 1
  ref = Br_element
FEATURE [App::DocumentObjectGroupPython] G4_FREON_13B1  label="G4_FREON-13B1"  # scripted group (container) (typed FeaturePython)
  Dunit = g/cm3
  Dvalue = 1.5
  Group = -> [C_element046,F_element010,Br_element002]
  conduct = 2
  density = 1
  expand = 3
  formula = G4_FREON-13B1
  name = G4_FREON-13B1
  specific = 4
FEATURE [App::DocumentObjectGroupPython] C_element047  label="C_element : 0.061"  # scripted group (container) (typed FeaturePython)
  n = 0.061309
FEATURE [App::DocumentObjectGroupPython] F_element011  label="F_element : 0.291"  # scripted group (container) (typed FeaturePython)
  n = 0.290924
FEATURE [App::DocumentObjectGroupPython] I_element002  label="I_element : 0.648"  # scripted group (container) (typed FeaturePython)
  n = 0.647767
FEATURE [App::DocumentObjectGroupPython] G4_FREON_13I1  label="G4_FREON-13I1"  # scripted group (container) (typed FeaturePython)
  Dunit = g/cm3
  Dvalue = 1.8
  Group = -> [C_element047,F_element011,I_element002]
  conduct = 2
  density = 1
  expand = 3
  formula = G4_FREON-13I1
  name = G4_FREON-13I1
  specific = 4
FEATURE [App::DocumentObjectGroupPython] Gd_element001  label="Gd_element : 2"  # scripted group (container) (typed FeaturePython)
  n = 2
  ref = Gd_element
FEATURE [App::DocumentObjectGroupPython] O_element041  label="O_element : 021"  # scripted group (container) (typed FeaturePython)
  n = 2
  ref = O_element
FEATURE [App::DocumentObjectGroupPython] S_element012  label="S_element : 004"  # scripted group (container) (typed FeaturePython)
  n = 1
  ref = S_element
FEATURE [App::DocumentObjectGroupPython] G4_GADOLINIUM_OXYSULFIDE  # scripted group (container) (typed FeaturePython)
  Dunit = g/cm3
  Dvalue = 7.44
  Group = -> [Gd_element001,O_element041,S_element012]
  conduct = 2
  density = 1
  expand = 3
  formula = G4_GADOLINIUM_OXYSULFIDE
  name = G4_GADOLINIUM_OXYSULFIDE
  specific = 4
FEATURE [App::DocumentObjectGroupPython] Ga_element001  label="Ga_element : 1"  # scripted group (container) (typed FeaturePython)
  n = 1
  ref = Ga_element
FEATURE [App::DocumentObjectGroupPython] As_element001  label="As_element : 1"  # scripted group (container) (typed FeaturePython)
  n = 1
  ref = As_element
FEATURE [App::DocumentObjectGroupPython] G4_GALLIUM_ARSENIDE  # scripted group (container) (typed FeaturePython)
  Dunit = g/cm3
  Dvalue = 5.31
  Group = -> [Ga_element001,As_element001]
  conduct = 2
  density = 1
  expand = 3
  formula = G4_GALLIUM_ARSENIDE
  name = G4_GALLIUM_ARSENIDE
  specific = 4
FEATURE [App::DocumentObjectGroupPython] H_element041  label="H_element : 0.081"  # scripted group (container) (typed FeaturePython)
  n = 0.08118
FEATURE [App::DocumentObjectGroupPython] C_element048  label="C_element : 0.416"  # scripted group (container) (typed FeaturePython)
  n = 0.41606
FEATURE [App::DocumentObjectGroupPython] N_element018  label="N_element : 0.111"  # scripted group (container) (typed FeaturePython)
  n = 0.11124
FEATURE [App::DocumentObjectGroupPython] O_element042  label="O_element : 0.381"  # scripted group (container) (typed FeaturePython)
  n = 0.38064
FEATURE [App::DocumentObjectGroupPython] S_element013  label="S_element : 0.011"  # scripted group (container) (typed FeaturePython)
  n = 0.01088
FEATURE [App::DocumentObjectGroupPython] G4_GEL_PHOTO_EMULSION  # scripted group (container) (typed FeaturePython)
  Dunit = g/cm3
  Dvalue = 1.2914
  Group = -> [H_element041,C_element048,N_element018,O_element042,S_element013]
  conduct = 2
  density = 1
  expand = 3
  formula = G4_GEL_PHOTO_EMULSION
  name = G4_GEL_PHOTO_EMULSION
  specific = 4
FEATURE [App::DocumentObjectGroupPython] B_element004  label="B_element : 0.040"  # scripted group (container) (typed FeaturePython)
  n = 0.0400639
FEATURE [App::DocumentObjectGroupPython] O_element043  label="O_element : 0.540"  # scripted group (container) (typed FeaturePython)
  n = 0.539561
FEATURE [App::DocumentObjectGroupPython] Na_element008  label="Na_element : 0.028"  # scripted group (container) (typed FeaturePython)
  n = 0.0281909
FEATURE [App::DocumentObjectGroupPython] Al_element003  label="Al_element : 0.012"  # scripted group (container) (typed FeaturePython)
  n = 0.011644
FEATURE [App::DocumentObjectGroupPython] Si_element003  label="Si_element : 0.377"  # scripted group (container) (typed FeaturePython)
  n = 0.377219
FEATURE [App::DocumentObjectGroupPython] K_element004  label="K_element : 0.014"  # scripted group (container) (typed FeaturePython)
  n = 0.00332099
FEATURE [App::DocumentObjectGroupPython] G4_Pyrex_Glass  # scripted group (container) (typed FeaturePython)
  Dunit = g/cm3
  Dvalue = 2.23
  Group = -> [B_element004,O_element043,Na_element008,Al_element003,Si_element003,K_element004]
  conduct = 2
  density = 1
  expand = 3
  formula = G4_Pyrex_Glass
  name = G4_Pyrex_Glass
  specific = 4
FEATURE [App::DocumentObjectGroupPython] O_element044  label="O_element : 0.156"  # scripted group (container) (typed FeaturePython)
  n = 0.156453
FEATURE [App::DocumentObjectGroupPython] Si_element004  label="Si_element : 0.081"  # scripted group (container) (typed FeaturePython)
  n = 0.080866
FEATURE [App::DocumentObjectGroupPython] Ti_element001  label="Ti_element : 0.008"  # scripted group (container) (typed FeaturePython)
  n = 0.008092
FEATURE [App::DocumentObjectGroupPython] As_element002  label="As_element : 0.003"  # scripted group (container) (typed FeaturePython)
  n = 0.002651
FEATURE [App::DocumentObjectGroupPython] Pb_element001  label="Pb_element : 0.752"  # scripted group (container) (typed FeaturePython)
  n = 0.751938
FEATURE [App::DocumentObjectGroupPython] G4_GLASS_LEAD  # scripted group (container) (typed FeaturePython)
  Dunit = g/cm3
  Dvalue = 6.22
  Group = -> [O_element044,Si_element004,Ti_element001,As_element002,Pb_element001]
  conduct = 2
  density = 1
  expand = 3
  formula = G4_GLASS_LEAD
  name = G4_GLASS_LEAD
  specific = 4
FEATURE [App::DocumentObjectGroupPython] O_element045  label="O_element : 0.460"  # scripted group (container) (typed FeaturePython)
  n = 0.4598
FEATURE [App::DocumentObjectGroupPython] Na_element009  label="Na_element : 0.096"  # scripted group (container) (typed FeaturePython)
  n = 0.0964411
FEATURE [App::DocumentObjectGroupPython] Si_element005  label="Si_element : 0.378"  # scripted group (container) (typed FeaturePython)
  n = 0.336553
FEATURE [App::DocumentObjectGroupPython] Ca_element011  label="Ca_element : 0.107"  # scripted group (container) (typed FeaturePython)
  n = 0.107205
FEATURE [App::DocumentObjectGroupPython] G4_GLASS_PLATE  # scripted group (container) (typed FeaturePython)
  Dunit = g/cm3
  Dvalue = 2.4
  Group = -> [O_element045,Na_element009,Si_element005,Ca_element011]
  conduct = 2
  density = 1
  expand = 3
  formula = G4_GLASS_PLATE
  name = G4_GLASS_PLATE
  specific = 4
FEATURE [App::DocumentObjectGroupPython] C_element049  label="C_element : 026"  # scripted group (container) (typed FeaturePython)
  n = 5
  ref = C_element
FEATURE [App::DocumentObjectGroupPython] H_element042  label="H_element : 021"  # scripted group (container) (typed FeaturePython)
  n = 10
  ref = H_element
FEATURE [App::DocumentObjectGroupPython] N_element019  label="N_element : 2"  # scripted group (container) (typed FeaturePython)
  n = 2
  ref = N_element
FEATURE [App::DocumentObjectGroupPython] O_element046  label="O_element : 022"  # scripted group (container) (typed FeaturePython)
  n = 3
  ref = O_element
FEATURE [App::DocumentObjectGroupPython] G4_GLUTAMINE  # scripted group (container) (typed FeaturePython)
  Dunit = g/cm3
  Dvalue = 1.46
  Group = -> [C_element049,H_element042,N_element019,O_element046]
  conduct = 2
  density = 1
  expand = 3
  formula = G4_GLUTAMINE
  name = G4_GLUTAMINE
  specific = 4
FEATURE [App::DocumentObjectGroupPython] C_element050  label="C_element : 027"  # scripted group (container) (typed FeaturePython)
  n = 3
  ref = C_element
FEATURE [App::DocumentObjectGroupPython] H_element043  label="H_element : 022"  # scripted group (container) (typed FeaturePython)
  n = 8
  ref = H_element
FEATURE [App::DocumentObjectGroupPython] O_element047  label="O_element : 023"  # scripted group (container) (typed FeaturePython)
  n = 3
  ref = O_element
FEATURE [App::DocumentObjectGroupPython] G4_GLYCEROL  # scripted group (container) (typed FeaturePython)
  Dunit = g/cm3
  Dvalue = 1.2613
  Group = -> [C_element050,H_element043,O_element047]
  conduct = 2
  density = 1
  expand = 3
  formula = G4_GLYCEROL
  name = G4_GLYCEROL
  specific = 4
FEATURE [App::DocumentObjectGroupPython] C_element051  label="C_element : 028"  # scripted group (container) (typed FeaturePython)
  n = 5
  ref = C_element
FEATURE [App::DocumentObjectGroupPython] H_element044  label="H_element : 023"  # scripted group (container) (typed FeaturePython)
  n = 5
  ref = H_element
FEATURE [App::DocumentObjectGroupPython] N_element020  label="N_element : 009"  # scripted group (container) (typed FeaturePython)
  n = 5
  ref = N_element
FEATURE [App::DocumentObjectGroupPython] O_element048  label="O_element : 024"  # scripted group (container) (typed FeaturePython)
  n = 1
  ref = O_element
FEATURE [App::DocumentObjectGroupPython] G4_GUANINE  # scripted group (container) (typed FeaturePython)
  Dunit = g/cm3
  Dvalue = 2.2
  Group = -> [C_element051,H_element044,N_element020,O_element048]
  conduct = 2
  density = 1
  expand = 3
  formula = G4_GUANINE
  name = G4_GUANINE
  specific = 4
FEATURE [App::DocumentObjectGroupPython] Ca_element012  label="Ca_element : 006"  # scripted group (container) (typed FeaturePython)
  n = 1
  ref = Ca_element
FEATURE [App::DocumentObjectGroupPython] S_element014  label="S_element : 005"  # scripted group (container) (typed FeaturePython)
  n = 1
  ref = S_element
FEATURE [App::DocumentObjectGroupPython] O_element049  label="O_element : 6"  # scripted group (container) (typed FeaturePython)
  n = 6
  ref = O_element
FEATURE [App::DocumentObjectGroupPython] H_element045  label="H_element : 024"  # scripted group (container) (typed FeaturePython)
  n = 4
  ref = H_element
FEATURE [App::DocumentObjectGroupPython] G4_GYPSUM  # scripted group (container) (typed FeaturePython)
  Dunit = g/cm3
  Dvalue = 2.32
  Group = -> [Ca_element012,S_element014,O_element049,H_element045]
  conduct = 2
  density = 1
  expand = 3
  formula = G4_GYPSUM
  name = G4_GYPSUM
  specific = 4
FEATURE [App::DocumentObjectGroupPython] C_element052  label="C_element : 7"  # scripted group (container) (typed FeaturePython)
  n = 7
  ref = C_element
FEATURE [App::DocumentObjectGroupPython] H_element046  label="H_element : 16"  # scripted group (container) (typed FeaturePython)
  n = 16
  ref = H_element
FEATURE [App::DocumentObjectGroupPython] G4_N_HEPTANE  label="G4_N-HEPTANE"  # scripted group (container) (typed FeaturePython)
  Dunit = g/cm3
  Dvalue = 0.68376
  Group = -> [C_element052,H_element046]
  conduct = 2
  density = 1
  expand = 3
  formula = G4_N-HEPTANE
  name = G4_N-HEPTANE
  specific = 4
FEATURE [App::DocumentObjectGroupPython] C_element053  label="C_element : 029"  # scripted group (container) (typed FeaturePython)
  n = 6
  ref = C_element
FEATURE [App::DocumentObjectGroupPython] H_element047  label="H_element : 14"  # scripted group (container) (typed FeaturePython)
  n = 14
  ref = H_element
FEATURE [App::DocumentObjectGroupPython] G4_N_HEXANE  label="G4_N-HEXANE"  # scripted group (container) (typed FeaturePython)
  Dunit = g/cm3
  Dvalue = 0.6603
  Group = -> [C_element053,H_element047]
  conduct = 2
  density = 1
  expand = 3
  formula = G4_N-HEXANE
  name = G4_N-HEXANE
  specific = 4
FEATURE [App::DocumentObjectGroupPython] C_element054  label="C_element : 22"  # scripted group (container) (typed FeaturePython)
  n = 22
  ref = C_element
FEATURE [App::DocumentObjectGroupPython] H_element048  label="H_element : 025"  # scripted group (container) (typed FeaturePython)
  n = 10
  ref = H_element
FEATURE [App::DocumentObjectGroupPython] N_element021  label="N_element : 010"  # scripted group (container) (typed FeaturePython)
  n = 2
  ref = N_element
FEATURE [App::DocumentObjectGroupPython] O_element050  label="O_element : 025"  # scripted group (container) (typed FeaturePython)
  n = 5
  ref = O_element
FEATURE [App::DocumentObjectGroupPython] G4_KAPTON  # scripted group (container) (typed FeaturePython)
  Dunit = g/cm3
  Dvalue = 1.42
  Group = -> [C_element054,H_element048,N_element021,O_element050]
  conduct = 2
  density = 1
  expand = 3
  formula = G4_KAPTON
  name = G4_KAPTON
  specific = 4
FEATURE [App::DocumentObjectGroupPython] La_element001  label="La_element : 1"  # scripted group (container) (typed FeaturePython)
  n = 1
  ref = La_element
FEATURE [App::DocumentObjectGroupPython] Br_element003  label="Br_element : 002"  # scripted group (container) (typed FeaturePython)
  n = 1
  ref = Br_element
FEATURE [App::DocumentObjectGroupPython] O_element051  label="O_element : 026"  # scripted group (container) (typed FeaturePython)
  n = 1
  ref = O_element
FEATURE [App::DocumentObjectGroupPython] G4_LANTHANUM_OXYBROMIDE  # scripted group (container) (typed FeaturePython)
  Dunit = g/cm3
  Dvalue = 6.28
  Group = -> [La_element001,Br_element003,O_element051]
  conduct = 2
  density = 1
  expand = 3
  formula = G4_LANTHANUM_OXYBROMIDE
  name = G4_LANTHANUM_OXYBROMIDE
  specific = 4
FEATURE [App::DocumentObjectGroupPython] La_element002  label="La_element : 2"  # scripted group (container) (typed FeaturePython)
  n = 2
  ref = La_element
FEATURE [App::DocumentObjectGroupPython] O_element052  label="O_element : 027"  # scripted group (container) (typed FeaturePython)
  n = 2
  ref = O_element
FEATURE [App::DocumentObjectGroupPython] S_element015  label="S_element : 006"  # scripted group (container) (typed FeaturePython)
  n = 1
  ref = S_element
FEATURE [App::DocumentObjectGroupPython] G4_LANTHANUM_OXYSULFIDE  # scripted group (container) (typed FeaturePython)
  Dunit = g/cm3
  Dvalue = 5.86
  Group = -> [La_element002,O_element052,S_element015]
  conduct = 2
  density = 1
  expand = 3
  formula = G4_LANTHANUM_OXYSULFIDE
  name = G4_LANTHANUM_OXYSULFIDE
  specific = 4
FEATURE [App::DocumentObjectGroupPython] O_element053  label="O_element : 0.072"  # scripted group (container) (typed FeaturePython)
  n = 0.071682
FEATURE [App::DocumentObjectGroupPython] Pb_element002  label="Pb_element : 0.928"  # scripted group (container) (typed FeaturePython)
  n = 0.928318
FEATURE [App::DocumentObjectGroupPython] G4_LEAD_OXIDE  # scripted group (container) (typed FeaturePython)
  Dunit = g/cm3
  Dvalue = 9.53
  Group = -> [O_element053,Pb_element002]
  conduct = 2
  density = 1
  expand = 3
  formula = G4_LEAD_OXIDE
  name = G4_LEAD_OXIDE
  specific = 4
FEATURE [App::DocumentObjectGroupPython] Li_element001  label="Li_element : 1"  # scripted group (container) (typed FeaturePython)
  n = 1
  ref = Li_element
FEATURE [App::DocumentObjectGroupPython] N_element022  label="N_element : 011"  # scripted group (container) (typed FeaturePython)
  n = 1
  ref = N_element
FEATURE [App::DocumentObjectGroupPython] H_element049  label="H_element : 026"  # scripted group (container) (typed FeaturePython)
  n = 2
  ref = H_element
FEATURE [App::DocumentObjectGroupPython] G4_LITHIUM_AMIDE  # scripted group (container) (typed FeaturePython)
  Dunit = g/cm3
  Dvalue = 1.178
  Group = -> [Li_element001,N_element022,H_element049]
  conduct = 2
  density = 1
  expand = 3
  formula = G4_LITHIUM_AMIDE
  name = G4_LITHIUM_AMIDE
  specific = 4
FEATURE [App::DocumentObjectGroupPython] Li_element002  label="Li_element : 2"  # scripted group (container) (typed FeaturePython)
  n = 2
  ref = Li_element
FEATURE [App::DocumentObjectGroupPython] C_element055  label="C_element : 030"  # scripted group (container) (typed FeaturePython)
  n = 1
  ref = C_element
FEATURE [App::DocumentObjectGroupPython] O_element054  label="O_element : 028"  # scripted group (container) (typed FeaturePython)
  n = 3
  ref = O_element
FEATURE [App::DocumentObjectGroupPython] G4_LITHIUM_CARBONATE  # scripted group (container) (typed FeaturePython)
  Dunit = g/cm3
  Dvalue = 2.11
  Group = -> [Li_element002,C_element055,O_element054]
  conduct = 2
  density = 1
  expand = 3
  formula = G4_LITHIUM_CARBONATE
  name = G4_LITHIUM_CARBONATE
  specific = 4
FEATURE [App::DocumentObjectGroupPython] Li_element003  label="Li_element : 003"  # scripted group (container) (typed FeaturePython)
  n = 1
  ref = Li_element
FEATURE [App::DocumentObjectGroupPython] F_element012  label="F_element : 004"  # scripted group (container) (typed FeaturePython)
  n = 1
  ref = F_element
FEATURE [App::DocumentObjectGroupPython] G4_LITHIUM_FLUORIDE  # scripted group (container) (typed FeaturePython)
  Dunit = g/cm3
  Dvalue = 2.635
  Group = -> [Li_element003,F_element012]
  conduct = 2
  density = 1
  expand = 3
  formula = G4_LITHIUM_FLUORIDE
  name = G4_LITHIUM_FLUORIDE
  specific = 4
FEATURE [App::DocumentObjectGroupPython] Li_element004  label="Li_element : 004"  # scripted group (container) (typed FeaturePython)
  n = 1
  ref = Li_element
FEATURE [App::DocumentObjectGroupPython] H_element050  label="H_element : 027"  # scripted group (container) (typed FeaturePython)
  n = 1
  ref = H_element
FEATURE [App::DocumentObjectGroupPython] G4_LITHIUM_HYDRIDE  # scripted group (container) (typed FeaturePython)
  Dunit = g/cm3
  Dvalue = 0.82
  Group = -> [Li_element004,H_element050]
  conduct = 2
  density = 1
  expand = 3
  formula = G4_LITHIUM_HYDRIDE
  name = G4_LITHIUM_HYDRIDE
  specific = 4
FEATURE [App::DocumentObjectGroupPython] Li_element005  label="Li_element : 005"  # scripted group (container) (typed FeaturePython)
  n = 1
  ref = Li_element
FEATURE [App::DocumentObjectGroupPython] I_element003  label="I_element : 002"  # scripted group (container) (typed FeaturePython)
  n = 1
  ref = I_element
FEATURE [App::DocumentObjectGroupPython] G4_LITHIUM_IODIDE  # scripted group (container) (typed FeaturePython)
  Dunit = g/cm3
  Dvalue = 3.494
  Group = -> [Li_element005,I_element003]
  conduct = 2
  density = 1
  expand = 3
  formula = G4_LITHIUM_IODIDE
  name = G4_LITHIUM_IODIDE
  specific = 4
FEATURE [App::DocumentObjectGroupPython] Li_element006  label="Li_element : 006"  # scripted group (container) (typed FeaturePython)
  n = 2
  ref = Li_element
FEATURE [App::DocumentObjectGroupPython] O_element055  label="O_element : 029"  # scripted group (container) (typed FeaturePython)
  n = 1
  ref = O_element
FEATURE [App::DocumentObjectGroupPython] G4_LITHIUM_OXIDE  # scripted group (container) (typed FeaturePython)
  Dunit = g/cm3
  Dvalue = 2.013
  Group = -> [Li_element006,O_element055]
  conduct = 2
  density = 1
  expand = 3
  formula = G4_LITHIUM_OXIDE
  name = G4_LITHIUM_OXIDE
  specific = 4
FEATURE [App::DocumentObjectGroupPython] Li_element007  label="Li_element : 007"  # scripted group (container) (typed FeaturePython)
  n = 2
  ref = Li_element
FEATURE [App::DocumentObjectGroupPython] B_element005  label="B_element : 005"  # scripted group (container) (typed FeaturePython)
  n = 4
  ref = B_element
FEATURE [App::DocumentObjectGroupPython] O_element056  label="O_element : 7"  # scripted group (container) (typed FeaturePython)
  n = 7
  ref = O_element
FEATURE [App::DocumentObjectGroupPython] G4_LITHIUM_TETRABORATE  # scripted group (container) (typed FeaturePython)
  Dunit = g/cm3
  Dvalue = 2.44
  Group = -> [Li_element007,B_element005,O_element056]
  conduct = 2
  density = 1
  expand = 3
  formula = G4_LITHIUM_TETRABORATE
  name = G4_LITHIUM_TETRABORATE
  specific = 4
FEATURE [App::DocumentObjectGroupPython] H_element051  label="H_element : 0.105"  # scripted group (container) (typed FeaturePython)
  n = 0.105
FEATURE [App::DocumentObjectGroupPython] C_element056  label="C_element : 0.083"  # scripted group (container) (typed FeaturePython)
  n = 0.083
FEATURE [App::DocumentObjectGroupPython] N_element023  label="N_element : 0.023"  # scripted group (container) (typed FeaturePython)
  n = 0.023
FEATURE [App::DocumentObjectGroupPython] O_element057  label="O_element : 0.779"  # scripted group (container) (typed FeaturePython)
  n = 0.779
FEATURE [App::DocumentObjectGroupPython] Na_element010  label="Na_element : 0.097"  # scripted group (container) (typed FeaturePython)
  n = 0.002
FEATURE [App::DocumentObjectGroupPython] P_element006  label="P_element : 0.105"  # scripted group (container) (typed FeaturePython)
  n = 0.001
FEATURE [App::DocumentObjectGroupPython] S_element016  label="S_element : 0.017"  # scripted group (container) (typed FeaturePython)
  n = 0.002
FEATURE [App::DocumentObjectGroupPython] Cl_element014  label="Cl_element : 0.587"  # scripted group (container) (typed FeaturePython)
  n = 0.003
FEATURE [App::DocumentObjectGroupPython] K_element005  label="K_element : 0.015"  # scripted group (container) (typed FeaturePython)
  n = 0.002
FEATURE [App::DocumentObjectGroupPython] G4_LUNG_ICRP  # scripted group (container) (typed FeaturePython)
  Dunit = g/cm3
  Dvalue = 1.04
  Group = -> [H_element051,C_element056,N_element023,O_element057,Na_element010,P_element006,S_element016,Cl_element014,K_element005]
  conduct = 2
  density = 1
  expand = 3
  formula = G4_LUNG_ICRP
  name = G4_LUNG_ICRP
  specific = 4
FEATURE [App::DocumentObjectGroupPython] H_element052  label="H_element : 0.116"  # scripted group (container) (typed FeaturePython)
  n = 0.114318
FEATURE [App::DocumentObjectGroupPython] C_element057  label="C_element : 0.656"  # scripted group (container) (typed FeaturePython)
  n = 0.655824
FEATURE [App::DocumentObjectGroupPython] O_element058  label="O_element : 0.092"  # scripted group (container) (typed FeaturePython)
  n = 0.0921831
FEATURE [App::DocumentObjectGroupPython] Mg_element004  label="Mg_element : 0.135"  # scripted group (container) (typed FeaturePython)
  n = 0.134792
FEATURE [App::DocumentObjectGroupPython] Ca_element013  label="Ca_element : 0.003"  # scripted group (container) (typed FeaturePython)
  n = 0.002883
FEATURE [App::DocumentObjectGroupPython] G4_M3_WAX  # scripted group (container) (typed FeaturePython)
  Dunit = g/cm3
  Dvalue = 1.05
  Group = -> [H_element052,C_element057,O_element058,Mg_element004,Ca_element013]
  conduct = 2
  density = 1
  expand = 3
  formula = G4_M3_WAX
  name = G4_M3_WAX
  specific = 4
FEATURE [App::DocumentObjectGroupPython] Mg_element005  label="Mg_element : 1"  # scripted group (container) (typed FeaturePython)
  n = 1
  ref = Mg_element
FEATURE [App::DocumentObjectGroupPython] C_element058  label="C_element : 031"  # scripted group (container) (typed FeaturePython)
  n = 1
  ref = C_element
FEATURE [App::DocumentObjectGroupPython] O_element059  label="O_element : 030"  # scripted group (container) (typed FeaturePython)
  n = 3
  ref = O_element
FEATURE [App::DocumentObjectGroupPython] G4_MAGNESIUM_CARBONATE  # scripted group (container) (typed FeaturePython)
  Dunit = g/cm3
  Dvalue = 2.958
  Group = -> [Mg_element005,C_element058,O_element059]
  conduct = 2
  density = 1
  expand = 3
  formula = G4_MAGNESIUM_CARBONATE
  name = G4_MAGNESIUM_CARBONATE
  specific = 4
FEATURE [App::DocumentObjectGroupPython] Mg_element006  label="Mg_element : 002"  # scripted group (container) (typed FeaturePython)
  n = 1
  ref = Mg_element
FEATURE [App::DocumentObjectGroupPython] F_element013  label="F_element : 005"  # scripted group (container) (typed FeaturePython)
  n = 2
  ref = F_element
FEATURE [App::DocumentObjectGroupPython] G4_MAGNESIUM_FLUORIDE  # scripted group (container) (typed FeaturePython)
  Dunit = g/cm3
  Dvalue = 3
  Group = -> [Mg_element006,F_element013]
  conduct = 2
  density = 1
  expand = 3
  formula = G4_MAGNESIUM_FLUORIDE
  name = G4_MAGNESIUM_FLUORIDE
  specific = 4
FEATURE [App::DocumentObjectGroupPython] Mg_element007  label="Mg_element : 003"  # scripted group (container) (typed FeaturePython)
  n = 1
  ref = Mg_element
FEATURE [App::DocumentObjectGroupPython] O_element060  label="O_element : 031"  # scripted group (container) (typed FeaturePython)
  n = 1
  ref = O_element
FEATURE [App::DocumentObjectGroupPython] G4_MAGNESIUM_OXIDE  # scripted group (container) (typed FeaturePython)
  Dunit = g/cm3
  Dvalue = 3.58
  Group = -> [Mg_element007,O_element060]
  conduct = 2
  density = 1
  expand = 3
  formula = G4_MAGNESIUM_OXIDE
  name = G4_MAGNESIUM_OXIDE
  specific = 4
FEATURE [App::DocumentObjectGroupPython] Mg_element008  label="Mg_element : 004"  # scripted group (container) (typed FeaturePython)
  n = 1
  ref = Mg_element
FEATURE [App::DocumentObjectGroupPython] B_element006  label="B_element : 006"  # scripted group (container) (typed FeaturePython)
  n = 4
  ref = B_element
FEATURE [App::DocumentObjectGroupPython] O_element061  label="O_element : 032"  # scripted group (container) (typed FeaturePython)
  n = 7
  ref = O_element
FEATURE [App::DocumentObjectGroupPython] G4_MAGNESIUM_TETRABORATE  # scripted group (container) (typed FeaturePython)
  Dunit = g/cm3
  Dvalue = 2.53
  Group = -> [Mg_element008,B_element006,O_element061]
  conduct = 2
  density = 1
  expand = 3
  formula = G4_MAGNESIUM_TETRABORATE
  name = G4_MAGNESIUM_TETRABORATE
  specific = 4
FEATURE [App::DocumentObjectGroupPython] Hg_element001  label="Hg_element : 1"  # scripted group (container) (typed FeaturePython)
  n = 1
  ref = Hg_element
FEATURE [App::DocumentObjectGroupPython] I_element004  label="I_element : 2"  # scripted group (container) (typed FeaturePython)
  n = 2
  ref = I_element
FEATURE [App::DocumentObjectGroupPython] G4_MERCURIC_IODIDE  # scripted group (container) (typed FeaturePython)
  Dunit = g/cm3
  Dvalue = 6.36
  Group = -> [Hg_element001,I_element004]
  conduct = 2
  density = 1
  expand = 3
  formula = G4_MERCURIC_IODIDE
  name = G4_MERCURIC_IODIDE
  specific = 4
FEATURE [App::DocumentObjectGroupPython] C_element059  label="C_element : 032"  # scripted group (container) (typed FeaturePython)
  n = 1
  ref = C_element
FEATURE [App::DocumentObjectGroupPython] H_element053  label="H_element : 028"  # scripted group (container) (typed FeaturePython)
  n = 4
  ref = H_element
FEATURE [App::DocumentObjectGroupPython] G4_METHANE  # scripted group (container) (typed FeaturePython)
  Dunit = g/cm3
  Dvalue = 0.000667151
  Group = -> [C_element059,H_element053]
  conduct = 2
  density = 1
  expand = 3
  formula = G4_METHANE
  name = G4_METHANE
  specific = 4
FEATURE [App::DocumentObjectGroupPython] C_element060  label="C_element : 033"  # scripted group (container) (typed FeaturePython)
  n = 1
  ref = C_element
FEATURE [App::DocumentObjectGroupPython] H_element054  label="H_element : 029"  # scripted group (container) (typed FeaturePython)
  n = 4
  ref = H_element
FEATURE [App::DocumentObjectGroupPython] O_element062  label="O_element : 033"  # scripted group (container) (typed FeaturePython)
  n = 1
  ref = O_element
FEATURE [App::DocumentObjectGroupPython] G4_METHANOL  # scripted group (container) (typed FeaturePython)
  Dunit = g/cm3
  Dvalue = 0.7914
  Group = -> [C_element060,H_element054,O_element062]
  conduct = 2
  density = 1
  expand = 3
  formula = G4_METHANOL
  name = G4_METHANOL
  specific = 4
FEATURE [App::DocumentObjectGroupPython] H_element055  label="H_element : 0.134"  # scripted group (container) (typed FeaturePython)
  n = 0.13404
FEATURE [App::DocumentObjectGroupPython] C_element061  label="C_element : 0.778"  # scripted group (container) (typed FeaturePython)
  n = 0.77796
FEATURE [App::DocumentObjectGroupPython] O_element063  label="O_element : 0.035"  # scripted group (container) (typed FeaturePython)
  n = 0.03502
FEATURE [App::DocumentObjectGroupPython] Mg_element009  label="Mg_element : 0.039"  # scripted group (container) (typed FeaturePython)
  n = 0.038594
FEATURE [App::DocumentObjectGroupPython] Ti_element002  label="Ti_element : 0.014"  # scripted group (container) (typed FeaturePython)
  n = 0.014386
FEATURE [App::DocumentObjectGroupPython] G4_MIX_D_WAX  # scripted group (container) (typed FeaturePython)
  Dunit = g/cm3
  Dvalue = 0.99
  Group = -> [H_element055,C_element061,O_element063,Mg_element009,Ti_element002]
  conduct = 2
  density = 1
  expand = 3
  formula = G4_MIX_D_WAX
  name = G4_MIX_D_WAX
  specific = 4
FEATURE [App::DocumentObjectGroupPython] H_element056  label="H_element : 0.135"  # scripted group (container) (typed FeaturePython)
  n = 0.081192
FEATURE [App::DocumentObjectGroupPython] C_element062  label="C_element : 0.583"  # scripted group (container) (typed FeaturePython)
  n = 0.583442
FEATURE [App::DocumentObjectGroupPython] N_element024  label="N_element : 0.018"  # scripted group (container) (typed FeaturePython)
  n = 0.017798
FEATURE [App::DocumentObjectGroupPython] O_element064  label="O_element : 0.186"  # scripted group (container) (typed FeaturePython)
  n = 0.186381
FEATURE [App::DocumentObjectGroupPython] Mg_element010  label="Mg_element : 0.130"  # scripted group (container) (typed FeaturePython)
  n = 0.130287
FEATURE [App::DocumentObjectGroupPython] Cl_element015  label="Cl_element : 0.588"  # scripted group (container) (typed FeaturePython)
  n = 0.0009
FEATURE [App::DocumentObjectGroupPython] G4_MS20_TISSUE  # scripted group (container) (typed FeaturePython)
  Dunit = g/cm3
  Dvalue = 1
  Group = -> [H_element056,C_element062,N_element024,O_element064,Mg_element010,Cl_element015]
  conduct = 2
  density = 1
  expand = 3
  formula = G4_MS20_TISSUE
  name = G4_MS20_TISSUE
  specific = 4
FEATURE [App::DocumentObjectGroupPython] H_element057  label="H_element : 0.136"  # scripted group (container) (typed FeaturePython)
  n = 0.102
FEATURE [App::DocumentObjectGroupPython] C_element063  label="C_element : 0.143"  # scripted group (container) (typed FeaturePython)
  n = 0.143
FEATURE [App::DocumentObjectGroupPython] N_element025  label="N_element : 0.034"  # scripted group (container) (typed FeaturePython)
  n = 0.034
FEATURE [App::DocumentObjectGroupPython] O_element065  label="O_element : 0.710"  # scripted group (container) (typed FeaturePython)
  n = 0.71
FEATURE [App::DocumentObjectGroupPython] Na_element011  label="Na_element : 0.098"  # scripted group (container) (typed FeaturePython)
  n = 0.001
FEATURE [App::DocumentObjectGroupPython] P_element007  label="P_element : 0.002"  # scripted group (container) (typed FeaturePython)
  n = 0.002
FEATURE [App::DocumentObjectGroupPython] S_element017  label="S_element : 0.018"  # scripted group (container) (typed FeaturePython)
  n = 0.003
FEATURE [App::DocumentObjectGroupPython] Cl_element016  label="Cl_element : 0.589"  # scripted group (container) (typed FeaturePython)
  n = 0.001
FEATURE [App::DocumentObjectGroupPython] K_element006  label="K_element : 0.004"  # scripted group (container) (typed FeaturePython)
  n = 0.004
FEATURE [App::DocumentObjectGroupPython] G4_MUSCLE_SKELETAL_ICRP  # scripted group (container) (typed FeaturePython)
  Dunit = g/cm3
  Dvalue = 1.05
  Group = -> [H_element057,C_element063,N_element025,O_element065,Na_element011,P_element007,S_element017,Cl_element016,K_element006]
  conduct = 2
  density = 1
  expand = 3
  formula = G4_MUSCLE_SKELETAL_ICRP
  name = G4_MUSCLE_SKELETAL_ICRP
  specific = 4
FEATURE [App::DocumentObjectGroupPython] H_element058  label="H_element : 0.137"  # scripted group (container) (typed FeaturePython)
  n = 0.102102
FEATURE [App::DocumentObjectGroupPython] C_element064  label="C_element : 0.123"  # scripted group (container) (typed FeaturePython)
  n = 0.123123
FEATURE [App::DocumentObjectGroupPython] N_element026  label="N_element : 0.756"  # scripted group (container) (typed FeaturePython)
  n = 0.035035
FEATURE [App::DocumentObjectGroupPython] O_element066  label="O_element : 0.730"  # scripted group (container) (typed FeaturePython)
  n = 0.72973
FEATURE [App::DocumentObjectGroupPython] Na_element012  label="Na_element : 0.099"  # scripted group (container) (typed FeaturePython)
  n = 0.001001
FEATURE [App::DocumentObjectGroupPython] P_element008  label="P_element : 0.106"  # scripted group (container) (typed FeaturePython)
  n = 0.002002
FEATURE [App::DocumentObjectGroupPython] S_element018  label="S_element : 0.019"  # scripted group (container) (typed FeaturePython)
  n = 0.004004
FEATURE [App::DocumentObjectGroupPython] K_element007  label="K_element : 0.016"  # scripted group (container) (typed FeaturePython)
  n = 0.003003
FEATURE [App::DocumentObjectGroupPython] G4_MUSCLE_STRIATED_ICRU  # scripted group (container) (typed FeaturePython)
  Dunit = g/cm3
  Dvalue = 1.04
  Group = -> [H_element058,C_element064,N_element026,O_element066,Na_element012,P_element008,S_element018,K_element007]
  conduct = 2
  density = 1
  expand = 3
  formula = G4_MUSCLE_STRIATED_ICRU
  name = G4_MUSCLE_STRIATED_ICRU
  specific = 4
FEATURE [App::DocumentObjectGroupPython] H_element059  label="H_element : 0.098"  # scripted group (container) (typed FeaturePython)
  n = 0.0982341
FEATURE [App::DocumentObjectGroupPython] C_element065  label="C_element : 0.156"  # scripted group (container) (typed FeaturePython)
  n = 0.156214
FEATURE [App::DocumentObjectGroupPython] N_element027  label="N_element : 0.757"  # scripted group (container) (typed FeaturePython)
  n = 0.035451
FEATURE [App::DocumentObjectGroupPython] O_element067  label="O_element : 0.880"  # scripted group (container) (typed FeaturePython)
  n = 0.710101
FEATURE [App::DocumentObjectGroupPython] G4_MUSCLE_WITH_SUCROSE  # scripted group (container) (typed FeaturePython)
  Dunit = g/cm3
  Dvalue = 1.11
  Group = -> [H_element059,C_element065,N_element027,O_element067]
  conduct = 2
  density = 1
  expand = 3
  formula = G4_MUSCLE_WITH_SUCROSE
  name = G4_MUSCLE_WITH_SUCROSE
  specific = 4
FEATURE [App::DocumentObjectGroupPython] H_element060  label="H_element : 0.138"  # scripted group (container) (typed FeaturePython)
  n = 0.101969
FEATURE [App::DocumentObjectGroupPython] C_element066  label="C_element : 0.120"  # scripted group (container) (typed FeaturePython)
  n = 0.120058
FEATURE [App::DocumentObjectGroupPython] N_element028  label="N_element : 0.758"  # scripted group (container) (typed FeaturePython)
  n = 0.035451
FEATURE [App::DocumentObjectGroupPython] O_element068  label="O_element : 0.743"  # scripted group (container) (typed FeaturePython)
  n = 0.742522
FEATURE [App::DocumentObjectGroupPython] G4_MUSCLE_WITHOUT_SUCROSE  # scripted group (container) (typed FeaturePython)
  Dunit = g/cm3
  Dvalue = 1.07
  Group = -> [H_element060,C_element066,N_element028,O_element068]
  conduct = 2
  density = 1
  expand = 3
  formula = G4_MUSCLE_WITHOUT_SUCROSE
  name = G4_MUSCLE_WITHOUT_SUCROSE
  specific = 4
FEATURE [App::DocumentObjectGroupPython] C_element067  label="C_element : 10"  # scripted group (container) (typed FeaturePython)
  n = 10
  ref = C_element
FEATURE [App::DocumentObjectGroupPython] H_element061  label="H_element : 030"  # scripted group (container) (typed FeaturePython)
  n = 8
  ref = H_element
FEATURE [App::DocumentObjectGroupPython] G4_NAPHTHALENE  # scripted group (container) (typed FeaturePython)
  Dunit = g/cm3
  Dvalue = 1.145
  Group = -> [C_element067,H_element061]
  conduct = 2
  density = 1
  expand = 3
  formula = G4_NAPHTHALENE
  name = G4_NAPHTHALENE
  specific = 4
FEATURE [App::DocumentObjectGroupPython] C_element068  label="C_element : 034"  # scripted group (container) (typed FeaturePython)
  n = 6
  ref = C_element
FEATURE [App::DocumentObjectGroupPython] H_element062  label="H_element : 031"  # scripted group (container) (typed FeaturePython)
  n = 5
  ref = H_element
FEATURE [App::DocumentObjectGroupPython] N_element029  label="N_element : 012"  # scripted group (container) (typed FeaturePython)
  n = 1
  ref = N_element
FEATURE [App::DocumentObjectGroupPython] O_element069  label="O_element : 034"  # scripted group (container) (typed FeaturePython)
  n = 2
  ref = O_element
FEATURE [App::DocumentObjectGroupPython] G4_NITROBENZENE  # scripted group (container) (typed FeaturePython)
  Dunit = g/cm3
  Dvalue = 1.19867
  Group = -> [C_element068,H_element062,N_element029,O_element069]
  conduct = 2
  density = 1
  expand = 3
  formula = G4_NITROBENZENE
  name = G4_NITROBENZENE
  specific = 4
FEATURE [App::DocumentObjectGroupPython] N_element030  label="N_element : 013"  # scripted group (container) (typed FeaturePython)
  n = 2
  ref = N_element
FEATURE [App::DocumentObjectGroupPython] O_element070  label="O_element : 035"  # scripted group (container) (typed FeaturePython)
  n = 1
  ref = O_element
FEATURE [App::DocumentObjectGroupPython] G4_NITROUS_OXIDE  # scripted group (container) (typed FeaturePython)
  Dunit = g/cm3
  Dvalue = 0.00183094
  Group = -> [N_element030,O_element070]
  conduct = 2
  density = 1
  expand = 3
  formula = G4_NITROUS_OXIDE
  name = G4_NITROUS_OXIDE
  specific = 4
FEATURE [App::DocumentObjectGroupPython] H_element063  label="H_element : 0.104"  # scripted group (container) (typed FeaturePython)
  n = 0.103509
FEATURE [App::DocumentObjectGroupPython] C_element069  label="C_element : 0.648"  # scripted group (container) (typed FeaturePython)
  n = 0.648416
FEATURE [App::DocumentObjectGroupPython] N_element031  label="N_element : 0.100"  # scripted group (container) (typed FeaturePython)
  n = 0.0995361
FEATURE [App::DocumentObjectGroupPython] O_element071  label="O_element : 0.149"  # scripted group (container) (typed FeaturePython)
  n = 0.148539
FEATURE [App::DocumentObjectGroupPython] G4_NYLON_8062  label="G4_NYLON-8062"  # scripted group (container) (typed FeaturePython)
  Dunit = g/cm3
  Dvalue = 1.08
  Group = -> [H_element063,C_element069,N_element031,O_element071]
  conduct = 2
  density = 1
  expand = 3
  formula = G4_NYLON-8062
  name = G4_NYLON-8062
  specific = 4
FEATURE [App::DocumentObjectGroupPython] C_element070  label="C_element : 035"  # scripted group (container) (typed FeaturePython)
  n = 6
  ref = C_element
FEATURE [App::DocumentObjectGroupPython] H_element064  label="H_element : 11"  # scripted group (container) (typed FeaturePython)
  n = 11
  ref = H_element
FEATURE [App::DocumentObjectGroupPython] N_element032  label="N_element : 014"  # scripted group (container) (typed FeaturePython)
  n = 1
  ref = N_element
FEATURE [App::DocumentObjectGroupPython] O_element072  label="O_element : 036"  # scripted group (container) (typed FeaturePython)
  n = 1
  ref = O_element
FEATURE [App::DocumentObjectGroupPython] G4_NYLON_6_6  label="G4_NYLON-6-6"  # scripted group (container) (typed FeaturePython)
  Dunit = g/cm3
  Dvalue = 1.14
  Group = -> [C_element070,H_element064,N_element032,O_element072]
  conduct = 2
  density = 1
  expand = 3
  formula = G4_NYLON-6-6
  name = G4_NYLON-6-6
  specific = 4
FEATURE [App::DocumentObjectGroupPython] H_element065  label="H_element : 0.139"  # scripted group (container) (typed FeaturePython)
  n = 0.107062
FEATURE [App::DocumentObjectGroupPython] C_element071  label="C_element : 0.680"  # scripted group (container) (typed FeaturePython)
  n = 0.680449
FEATURE [App::DocumentObjectGroupPython] N_element033  label="N_element : 0.099"  # scripted group (container) (typed FeaturePython)
  n = 0.099189
FEATURE [App::DocumentObjectGroupPython] O_element073  label="O_element : 0.113"  # scripted group (container) (typed FeaturePython)
  n = 0.1133
FEATURE [App::DocumentObjectGroupPython] G4_NYLON_6_10  label="G4_NYLON-6-10"  # scripted group (container) (typed FeaturePython)
  Dunit = g/cm3
  Dvalue = 1.14
  Group = -> [H_element065,C_element071,N_element033,O_element073]
  conduct = 2
  density = 1
  expand = 3
  formula = G4_NYLON-6-10
  name = G4_NYLON-6-10
  specific = 4
FEATURE [App::DocumentObjectGroupPython] H_element066  label="H_element : 0.140"  # scripted group (container) (typed FeaturePython)
  n = 0.115476
FEATURE [App::DocumentObjectGroupPython] C_element072  label="C_element : 0.721"  # scripted group (container) (typed FeaturePython)
  n = 0.720818
FEATURE [App::DocumentObjectGroupPython] N_element034  label="N_element : 0.076"  # scripted group (container) (typed FeaturePython)
  n = 0.0764169
FEATURE [App::DocumentObjectGroupPython] O_element074  label="O_element : 0.087"  # scripted group (container) (typed FeaturePython)
  n = 0.0872889
FEATURE [App::DocumentObjectGroupPython] G4_NYLON_11_RILSAN  label="G4_NYLON-11_RILSAN"  # scripted group (container) (typed FeaturePython)
  Dunit = g/cm3
  Dvalue = 1.425
  Group = -> [H_element066,C_element072,N_element034,O_element074]
  conduct = 2
  density = 1
  expand = 3
  formula = G4_NYLON-11_RILSAN
  name = G4_NYLON-11_RILSAN
  specific = 4
FEATURE [App::DocumentObjectGroupPython] C_element073  label="C_element : 8"  # scripted group (container) (typed FeaturePython)
  n = 8
  ref = C_element
FEATURE [App::DocumentObjectGroupPython] H_element067  label="H_element : 18"  # scripted group (container) (typed FeaturePython)
  n = 18
  ref = H_element
FEATURE [App::DocumentObjectGroupPython] G4_OCTANE  # scripted group (container) (typed FeaturePython)
  Dunit = g/cm3
  Dvalue = 0.7026
  Group = -> [C_element073,H_element067]
  conduct = 2
  density = 1
  expand = 3
  formula = G4_OCTANE
  name = G4_OCTANE
  specific = 4
FEATURE [App::DocumentObjectGroupPython] C_element074  label="C_element : 25"  # scripted group (container) (typed FeaturePython)
  n = 25
  ref = C_element
FEATURE [App::DocumentObjectGroupPython] H_element068  label="H_element : 52"  # scripted group (container) (typed FeaturePython)
  n = 52
  ref = H_element
FEATURE [App::DocumentObjectGroupPython] G4_PARAFFIN  # scripted group (container) (typed FeaturePython)
  Dunit = g/cm3
  Dvalue = 0.93
  Group = -> [C_element074,H_element068]
  conduct = 2
  density = 1
  expand = 3
  formula = G4_PARAFFIN
  name = G4_PARAFFIN
  specific = 4
FEATURE [App::DocumentObjectGroupPython] C_element075  label="C_element : 036"  # scripted group (container) (typed FeaturePython)
  n = 5
  ref = C_element
FEATURE [App::DocumentObjectGroupPython] H_element069  label="H_element : 032"  # scripted group (container) (typed FeaturePython)
  n = 12
  ref = H_element
FEATURE [App::DocumentObjectGroupPython] G4_N_PENTANE  label="G4_N-PENTANE"  # scripted group (container) (typed FeaturePython)
  Dunit = g/cm3
  Dvalue = 0.6262
  Group = -> [C_element075,H_element069]
  conduct = 2
  density = 1
  expand = 3
  formula = G4_N-PENTANE
  name = G4_N-PENTANE
  specific = 4
FEATURE [App::DocumentObjectGroupPython] H_element070  label="H_element : 0.014"  # scripted group (container) (typed FeaturePython)
  n = 0.0141
FEATURE [App::DocumentObjectGroupPython] C_element076  label="C_element : 0.072"  # scripted group (container) (typed FeaturePython)
  n = 0.072261
FEATURE [App::DocumentObjectGroupPython] N_element035  label="N_element : 0.019"  # scripted group (container) (typed FeaturePython)
  n = 0.01932
FEATURE [App::DocumentObjectGroupPython] O_element075  label="O_element : 0.066"  # scripted group (container) (typed FeaturePython)
  n = 0.066101
FEATURE [App::DocumentObjectGroupPython] S_element019  label="S_element : 0.020"  # scripted group (container) (typed FeaturePython)
  n = 0.00189
FEATURE [App::DocumentObjectGroupPython] Br_element004  label="Br_element : 0.349"  # scripted group (container) (typed FeaturePython)
  n = 0.349103
FEATURE [App::DocumentObjectGroupPython] Ag_element001  label="Ag_element : 0.474"  # scripted group (container) (typed FeaturePython)
  n = 0.474105
FEATURE [App::DocumentObjectGroupPython] I_element005  label="I_element : 0.003"  # scripted group (container) (typed FeaturePython)
  n = 0.00312
FEATURE [App::DocumentObjectGroupPython] G4_PHOTO_EMULSION  # scripted group (container) (typed FeaturePython)
  Dunit = g/cm3
  Dvalue = 3.815
  Group = -> [H_element070,C_element076,N_element035,O_element075,S_element019,Br_element004,Ag_element001,I_element005]
  conduct = 2
  density = 1
  expand = 3
  formula = G4_PHOTO_EMULSION
  name = G4_PHOTO_EMULSION
  specific = 4
FEATURE [App::DocumentObjectGroupPython] C_element077  label="C_element : 9"  # scripted group (container) (typed FeaturePython)
  n = 9
  ref = C_element
FEATURE [App::DocumentObjectGroupPython] H_element071  label="H_element : 033"  # scripted group (container) (typed FeaturePython)
  n = 10
  ref = H_element
FEATURE [App::DocumentObjectGroupPython] G4_PLASTIC_SC_VINYLTOLUENE  # scripted group (container) (typed FeaturePython)
  Dunit = g/cm3
  Dvalue = 1.032
  Group = -> [C_element077,H_element071]
  conduct = 2
  density = 1
  expand = 3
  formula = G4_PLASTIC_SC_VINYLTOLUENE
  name = G4_PLASTIC_SC_VINYLTOLUENE
  specific = 4
FEATURE [App::DocumentObjectGroupPython] Pu_element001  label="Pu_element : 1"  # scripted group (container) (typed FeaturePython)
  n = 1
  ref = Pu_element
FEATURE [App::DocumentObjectGroupPython] O_element076  label="O_element : 037"  # scripted group (container) (typed FeaturePython)
  n = 2
  ref = O_element
FEATURE [App::DocumentObjectGroupPython] G4_PLUTONIUM_DIOXIDE  # scripted group (container) (typed FeaturePython)
  Dunit = g/cm3
  Dvalue = 11.46
  Group = -> [Pu_element001,O_element076]
  conduct = 2
  density = 1
  expand = 3
  formula = G4_PLUTONIUM_DIOXIDE
  name = G4_PLUTONIUM_DIOXIDE
  specific = 4
FEATURE [App::DocumentObjectGroupPython] C_element078  label="C_element : 037"  # scripted group (container) (typed FeaturePython)
  n = 3
  ref = C_element
FEATURE [App::DocumentObjectGroupPython] H_element072  label="H_element : 034"  # scripted group (container) (typed FeaturePython)
  n = 3
  ref = H_element
FEATURE [App::DocumentObjectGroupPython] N_element036  label="N_element : 015"  # scripted group (container) (typed FeaturePython)
  n = 1
  ref = N_element
FEATURE [App::DocumentObjectGroupPython] G4_POLYACRYLONITRILE  # scripted group (container) (typed FeaturePython)
  Dunit = g/cm3
  Dvalue = 1.17
  Group = -> [C_element078,H_element072,N_element036]
  conduct = 2
  density = 1
  expand = 3
  formula = G4_POLYACRYLONITRILE
  name = G4_POLYACRYLONITRILE
  specific = 4
FEATURE [App::DocumentObjectGroupPython] C_element079  label="C_element : 16"  # scripted group (container) (typed FeaturePython)
  n = 16
  ref = C_element
FEATURE [App::DocumentObjectGroupPython] H_element073  label="H_element : 035"  # scripted group (container) (typed FeaturePython)
  n = 14
  ref = H_element
FEATURE [App::DocumentObjectGroupPython] O_element077  label="O_element : 038"  # scripted group (container) (typed FeaturePython)
  n = 3
  ref = O_element
FEATURE [App::DocumentObjectGroupPython] G4_POLYCARBONATE  # scripted group (container) (typed FeaturePython)
  Dunit = g/cm3
  Dvalue = 1.2
  Group = -> [C_element079,H_element073,O_element077]
  conduct = 2
  density = 1
  expand = 3
  formula = G4_POLYCARBONATE
  name = G4_POLYCARBONATE
  specific = 4
FEATURE [App::DocumentObjectGroupPython] C_element080  label="C_element : 038"  # scripted group (container) (typed FeaturePython)
  n = 8
  ref = C_element
FEATURE [App::DocumentObjectGroupPython] H_element074  label="H_element : 036"  # scripted group (container) (typed FeaturePython)
  n = 7
  ref = H_element
FEATURE [App::DocumentObjectGroupPython] Cl_element017  label="Cl_element : 007"  # scripted group (container) (typed FeaturePython)
  n = 1
  ref = Cl_element
FEATURE [App::DocumentObjectGroupPython] G4_POLYCHLOROSTYRENE  # scripted group (container) (typed FeaturePython)
  Dunit = g/cm3
  Dvalue = 1.3
  Group = -> [C_element080,H_element074,Cl_element017]
  conduct = 2
  density = 1
  expand = 3
  formula = G4_POLYCHLOROSTYRENE
  name = G4_POLYCHLOROSTYRENE
  specific = 4
FEATURE [App::DocumentObjectGroupPython] C_element081  label="C_element : 039"  # scripted group (container) (typed FeaturePython)
  n = 1
  ref = C_element
FEATURE [App::DocumentObjectGroupPython] H_element075  label="H_element : 037"  # scripted group (container) (typed FeaturePython)
  n = 2
  ref = H_element
FEATURE [App::DocumentObjectGroupPython] G4_POLYETHYLENE  # scripted group (container) (typed FeaturePython)
  Dunit = g/cm3
  Dvalue = 0.94
  Group = -> [C_element081,H_element075]
  conduct = 2
  density = 1
  expand = 3
  formula = G4_POLYETHYLENE
  name = G4_POLYETHYLENE
  specific = 4
FEATURE [App::DocumentObjectGroupPython] C_element082  label="C_element : 040"  # scripted group (container) (typed FeaturePython)
  n = 10
  ref = C_element
FEATURE [App::DocumentObjectGroupPython] H_element076  label="H_element : 038"  # scripted group (container) (typed FeaturePython)
  n = 8
  ref = H_element
FEATURE [App::DocumentObjectGroupPython] O_element078  label="O_element : 039"  # scripted group (container) (typed FeaturePython)
  n = 4
  ref = O_element
FEATURE [App::DocumentObjectGroupPython] G4_MYLAR  # scripted group (container) (typed FeaturePython)
  Dunit = g/cm3
  Dvalue = 1.4
  Group = -> [C_element082,H_element076,O_element078]
  conduct = 2
  density = 1
  expand = 3
  formula = G4_MYLAR
  name = G4_MYLAR
  specific = 4
FEATURE [App::DocumentObjectGroupPython] C_element083  label="C_element : 041"  # scripted group (container) (typed FeaturePython)
  n = 5
  ref = C_element
FEATURE [App::DocumentObjectGroupPython] H_element077  label="H_element : 039"  # scripted group (container) (typed FeaturePython)
  n = 8
  ref = H_element
FEATURE [App::DocumentObjectGroupPython] O_element079  label="O_element : 040"  # scripted group (container) (typed FeaturePython)
  n = 2
  ref = O_element
FEATURE [App::DocumentObjectGroupPython] G4_PLEXIGLASS  # scripted group (container) (typed FeaturePython)
  Dunit = g/cm3
  Dvalue = 1.19
  Group = -> [C_element083,H_element077,O_element079]
  conduct = 2
  density = 1
  expand = 3
  formula = G4_PLEXIGLASS
  name = G4_PLEXIGLASS
  specific = 4
FEATURE [App::DocumentObjectGroupPython] C_element084  label="C_element : 042"  # scripted group (container) (typed FeaturePython)
  n = 1
  ref = C_element
FEATURE [App::DocumentObjectGroupPython] H_element078  label="H_element : 040"  # scripted group (container) (typed FeaturePython)
  n = 2
  ref = H_element
FEATURE [App::DocumentObjectGroupPython] O_element080  label="O_element : 041"  # scripted group (container) (typed FeaturePython)
  n = 1
  ref = O_element
FEATURE [App::DocumentObjectGroupPython] G4_POLYOXYMETHYLENE  # scripted group (container) (typed FeaturePython)
  Dunit = g/cm3
  Dvalue = 1.425
  Group = -> [C_element084,H_element078,O_element080]
  conduct = 2
  density = 1
  expand = 3
  formula = G4_POLYOXYMETHYLENE
  name = G4_POLYOXYMETHYLENE
  specific = 4
FEATURE [App::DocumentObjectGroupPython] C_element085  label="C_element : 043"  # scripted group (container) (typed FeaturePython)
  n = 2
  ref = C_element
FEATURE [App::DocumentObjectGroupPython] H_element079  label="H_element : 041"  # scripted group (container) (typed FeaturePython)
  n = 4
  ref = H_element
FEATURE [App::DocumentObjectGroupPython] G4_POLYPROPYLENE  # scripted group (container) (typed FeaturePython)
  Dunit = g/cm3
  Dvalue = 0.9
  Group = -> [C_element085,H_element079]
  conduct = 2
  density = 1
  expand = 3
  formula = G4_POLYPROPYLENE
  name = G4_POLYPROPYLENE
  specific = 4
FEATURE [App::DocumentObjectGroupPython] C_element086  label="C_element : 044"  # scripted group (container) (typed FeaturePython)
  n = 8
  ref = C_element
FEATURE [App::DocumentObjectGroupPython] H_element080  label="H_element : 042"  # scripted group (container) (typed FeaturePython)
  n = 8
  ref = H_element
FEATURE [App::DocumentObjectGroupPython] G4_POLYSTYRENE  # scripted group (container) (typed FeaturePython)
  Dunit = g/cm3
  Dvalue = 1.06
  Group = -> [C_element086,H_element080]
  conduct = 2
  density = 1
  expand = 3
  formula = G4_POLYSTYRENE
  name = G4_POLYSTYRENE
  specific = 4
FEATURE [App::DocumentObjectGroupPython] C_element087  label="C_element : 045"  # scripted group (container) (typed FeaturePython)
  n = 2
  ref = C_element
FEATURE [App::DocumentObjectGroupPython] F_element014  label="F_element : 4"  # scripted group (container) (typed FeaturePython)
  n = 4
  ref = F_element
FEATURE [App::DocumentObjectGroupPython] G4_TEFLON  # scripted group (container) (typed FeaturePython)
  Dunit = g/cm3
  Dvalue = 2.2
  Group = -> [C_element087,F_element014]
  conduct = 2
  density = 1
  expand = 3
  formula = G4_TEFLON
  name = G4_TEFLON
  specific = 4
FEATURE [App::DocumentObjectGroupPython] C_element088  label="C_element : 046"  # scripted group (container) (typed FeaturePython)
  n = 2
  ref = C_element
FEATURE [App::DocumentObjectGroupPython] F_element015  label="F_element : 006"  # scripted group (container) (typed FeaturePython)
  n = 3
  ref = F_element
FEATURE [App::DocumentObjectGroupPython] Cl_element018  label="Cl_element : 008"  # scripted group (container) (typed FeaturePython)
  n = 1
  ref = Cl_element
FEATURE [App::DocumentObjectGroupPython] G4_POLYTRIFLUOROCHLOROETHYLENE  # scripted group (container) (typed FeaturePython)
  Dunit = g/cm3
  Dvalue = 2.1
  Group = -> [C_element088,F_element015,Cl_element018]
  conduct = 2
  density = 1
  expand = 3
  formula = G4_POLYTRIFLUOROCHLOROETHYLENE
  name = G4_POLYTRIFLUOROCHLOROETHYLENE
  specific = 4
FEATURE [App::DocumentObjectGroupPython] C_element089  label="C_element : 047"  # scripted group (container) (typed FeaturePython)
  n = 4
  ref = C_element
FEATURE [App::DocumentObjectGroupPython] H_element081  label="H_element : 043"  # scripted group (container) (typed FeaturePython)
  n = 6
  ref = H_element
FEATURE [App::DocumentObjectGroupPython] O_element081  label="O_element : 042"  # scripted group (container) (typed FeaturePython)
  n = 2
  ref = O_element
FEATURE [App::DocumentObjectGroupPython] G4_POLYVINYL_ACETATE  # scripted group (container) (typed FeaturePython)
  Dunit = g/cm3
  Dvalue = 1.19
  Group = -> [C_element089,H_element081,O_element081]
  conduct = 2
  density = 1
  expand = 3
  formula = G4_POLYVINYL_ACETATE
  name = G4_POLYVINYL_ACETATE
  specific = 4
FEATURE [App::DocumentObjectGroupPython] C_element090  label="C_element : 048"  # scripted group (container) (typed FeaturePython)
  n = 2
  ref = C_element
FEATURE [App::DocumentObjectGroupPython] H_element082  label="H_element : 044"  # scripted group (container) (typed FeaturePython)
  n = 4
  ref = H_element
FEATURE [App::DocumentObjectGroupPython] O_element082  label="O_element : 043"  # scripted group (container) (typed FeaturePython)
  n = 1
  ref = O_element
FEATURE [App::DocumentObjectGroupPython] G4_POLYVINYL_ALCOHOL  # scripted group (container) (typed FeaturePython)
  Dunit = g/cm3
  Dvalue = 1.3
  Group = -> [C_element090,H_element082,O_element082]
  conduct = 2
  density = 1
  expand = 3
  formula = G4_POLYVINYL_ALCOHOL
  name = G4_POLYVINYL_ALCOHOL
  specific = 4
FEATURE [App::DocumentObjectGroupPython] C_element091  label="C_element : 049"  # scripted group (container) (typed FeaturePython)
  n = 8
  ref = C_element
FEATURE [App::DocumentObjectGroupPython] H_element083  label="H_element : 045"  # scripted group (container) (typed FeaturePython)
  n = 14
  ref = H_element
FEATURE [App::DocumentObjectGroupPython] O_element083  label="O_element : 044"  # scripted group (container) (typed FeaturePython)
  n = 2
  ref = O_element
FEATURE [App::DocumentObjectGroupPython] G4_POLYVINYL_BUTYRAL  # scripted group (container) (typed FeaturePython)
  Dunit = g/cm3
  Dvalue = 1.12
  Group = -> [C_element091,H_element083,O_element083]
  conduct = 2
  density = 1
  expand = 3
  formula = G4_POLYVINYL_BUTYRAL
  name = G4_POLYVINYL_BUTYRAL
  specific = 4
FEATURE [App::DocumentObjectGroupPython] C_element092  label="C_element : 050"  # scripted group (container) (typed FeaturePython)
  n = 2
  ref = C_element
FEATURE [App::DocumentObjectGroupPython] H_element084  label="H_element : 046"  # scripted group (container) (typed FeaturePython)
  n = 3
  ref = H_element
FEATURE [App::DocumentObjectGroupPython] Cl_element019  label="Cl_element : 009"  # scripted group (container) (typed FeaturePython)
  n = 1
  ref = Cl_element
FEATURE [App::DocumentObjectGroupPython] G4_POLYVINYL_CHLORIDE  # scripted group (container) (typed FeaturePython)
  Dunit = g/cm3
  Dvalue = 1.3
  Group = -> [C_element092,H_element084,Cl_element019]
  conduct = 2
  density = 1
  expand = 3
  formula = G4_POLYVINYL_CHLORIDE
  name = G4_POLYVINYL_CHLORIDE
  specific = 4
FEATURE [App::DocumentObjectGroupPython] C_element093  label="C_element : 051"  # scripted group (container) (typed FeaturePython)
  n = 2
  ref = C_element
FEATURE [App::DocumentObjectGroupPython] H_element085  label="H_element : 047"  # scripted group (container) (typed FeaturePython)
  n = 2
  ref = H_element
FEATURE [App::DocumentObjectGroupPython] Cl_element020  label="Cl_element : 010"  # scripted group (container) (typed FeaturePython)
  n = 2
  ref = Cl_element
FEATURE [App::DocumentObjectGroupPython] G4_POLYVINYLIDENE_CHLORIDE  # scripted group (container) (typed FeaturePython)
  Dunit = g/cm3
  Dvalue = 1.7
  Group = -> [C_element093,H_element085,Cl_element020]
  conduct = 2
  density = 1
  expand = 3
  formula = G4_POLYVINYLIDENE_CHLORIDE
  name = G4_POLYVINYLIDENE_CHLORIDE
  specific = 4
FEATURE [App::DocumentObjectGroupPython] C_element094  label="C_element : 052"  # scripted group (container) (typed FeaturePython)
  n = 2
  ref = C_element
FEATURE [App::DocumentObjectGroupPython] H_element086  label="H_element : 048"  # scripted group (container) (typed FeaturePython)
  n = 2
  ref = H_element
FEATURE [App::DocumentObjectGroupPython] F_element016  label="F_element : 007"  # scripted group (container) (typed FeaturePython)
  n = 2
  ref = F_element
FEATURE [App::DocumentObjectGroupPython] G4_POLYVINYLIDENE_FLUORIDE  # scripted group (container) (typed FeaturePython)
  Dunit = g/cm3
  Dvalue = 1.76
  Group = -> [C_element094,H_element086,F_element016]
  conduct = 2
  density = 1
  expand = 3
  formula = G4_POLYVINYLIDENE_FLUORIDE
  name = G4_POLYVINYLIDENE_FLUORIDE
  specific = 4
FEATURE [App::DocumentObjectGroupPython] C_element095  label="C_element : 053"  # scripted group (container) (typed FeaturePython)
  n = 6
  ref = C_element
FEATURE [App::DocumentObjectGroupPython] H_element087  label="H_element : 9"  # scripted group (container) (typed FeaturePython)
  n = 9
  ref = H_element
FEATURE [App::DocumentObjectGroupPython] N_element037  label="N_element : 016"  # scripted group (container) (typed FeaturePython)
  n = 1
  ref = N_element
FEATURE [App::DocumentObjectGroupPython] O_element084  label="O_element : 045"  # scripted group (container) (typed FeaturePython)
  n = 1
  ref = O_element
FEATURE [App::DocumentObjectGroupPython] G4_POLYVINYL_PYRROLIDONE  # scripted group (container) (typed FeaturePython)
  Dunit = g/cm3
  Dvalue = 1.25
  Group = -> [C_element095,H_element087,N_element037,O_element084]
  conduct = 2
  density = 1
  expand = 3
  formula = G4_POLYVINYL_PYRROLIDONE
  name = G4_POLYVINYL_PYRROLIDONE
  specific = 4
FEATURE [App::DocumentObjectGroupPython] K_element008  label="K_element : 1"  # scripted group (container) (typed FeaturePython)
  n = 1
  ref = K_element
FEATURE [App::DocumentObjectGroupPython] I_element006  label="I_element : 003"  # scripted group (container) (typed FeaturePython)
  n = 1
  ref = I_element
FEATURE [App::DocumentObjectGroupPython] G4_POTASSIUM_IODIDE  # scripted group (container) (typed FeaturePython)
  Dunit = g/cm3
  Dvalue = 3.13
  Group = -> [K_element008,I_element006]
  conduct = 2
  density = 1
  expand = 3
  formula = G4_POTASSIUM_IODIDE
  name = G4_POTASSIUM_IODIDE
  specific = 4
FEATURE [App::DocumentObjectGroupPython] K_element009  label="K_element : 2"  # scripted group (container) (typed FeaturePython)
  n = 2
  ref = K_element
FEATURE [App::DocumentObjectGroupPython] O_element085  label="O_element : 046"  # scripted group (container) (typed FeaturePython)
  n = 1
  ref = O_element
FEATURE [App::DocumentObjectGroupPython] G4_POTASSIUM_OXIDE  # scripted group (container) (typed FeaturePython)
  Dunit = g/cm3
  Dvalue = 2.32
  Group = -> [K_element009,O_element085]
  conduct = 2
  density = 1
  expand = 3
  formula = G4_POTASSIUM_OXIDE
  name = G4_POTASSIUM_OXIDE
  specific = 4
FEATURE [App::DocumentObjectGroupPython] C_element096  label="C_element : 054"  # scripted group (container) (typed FeaturePython)
  n = 3
  ref = C_element
FEATURE [App::DocumentObjectGroupPython] H_element088  label="H_element : 049"  # scripted group (container) (typed FeaturePython)
  n = 8
  ref = H_element
FEATURE [App::DocumentObjectGroupPython] G4_PROPANE  # scripted group (container) (typed FeaturePython)
  Dunit = g/cm3
  Dvalue = 0.00187939
  Group = -> [C_element096,H_element088]
  conduct = 2
  density = 1
  expand = 3
  formula = G4_PROPANE
  name = G4_PROPANE
  specific = 4
FEATURE [App::DocumentObjectGroupPython] C_element097  label="C_element : 055"  # scripted group (container) (typed FeaturePython)
  n = 3
  ref = C_element
FEATURE [App::DocumentObjectGroupPython] H_element089  label="H_element : 050"  # scripted group (container) (typed FeaturePython)
  n = 8
  ref = H_element
FEATURE [App::DocumentObjectGroupPython] G4_lPROPANE  # scripted group (container) (typed FeaturePython)
  Dunit = g/cm3
  Dvalue = 0.43
  Group = -> [C_element097,H_element089]
  conduct = 2
  density = 1
  expand = 3
  formula = G4_lPROPANE
  name = G4_lPROPANE
  specific = 4
FEATURE [App::DocumentObjectGroupPython] C_element098  label="C_element : 056"  # scripted group (container) (typed FeaturePython)
  n = 3
  ref = C_element
FEATURE [App::DocumentObjectGroupPython] H_element090  label="H_element : 051"  # scripted group (container) (typed FeaturePython)
  n = 8
  ref = H_element
FEATURE [App::DocumentObjectGroupPython] O_element086  label="O_element : 047"  # scripted group (container) (typed FeaturePython)
  n = 1
  ref = O_element
FEATURE [App::DocumentObjectGroupPython] G4_N_PROPYL_ALCOHOL  label="G4_N-PROPYL_ALCOHOL"  # scripted group (container) (typed FeaturePython)
  Dunit = g/cm3
  Dvalue = 0.8035
  Group = -> [C_element098,H_element090,O_element086]
  conduct = 2
  density = 1
  expand = 3
  formula = G4_N-PROPYL_ALCOHOL
  name = G4_N-PROPYL_ALCOHOL
  specific = 4
FEATURE [App::DocumentObjectGroupPython] C_element099  label="C_element : 057"  # scripted group (container) (typed FeaturePython)
  n = 5
  ref = C_element
FEATURE [App::DocumentObjectGroupPython] H_element091  label="H_element : 052"  # scripted group (container) (typed FeaturePython)
  n = 5
  ref = H_element
FEATURE [App::DocumentObjectGroupPython] N_element038  label="N_element : 017"  # scripted group (container) (typed FeaturePython)
  n = 1
  ref = N_element
FEATURE [App::DocumentObjectGroupPython] G4_PYRIDINE  # scripted group (container) (typed FeaturePython)
  Dunit = g/cm3
  Dvalue = 0.9819
  Group = -> [C_element099,H_element091,N_element038]
  conduct = 2
  density = 1
  expand = 3
  formula = G4_PYRIDINE
  name = G4_PYRIDINE
  specific = 4
FEATURE [App::DocumentObjectGroupPython] H_element092  label="H_element : 0.144"  # scripted group (container) (typed FeaturePython)
  n = 0.143711
FEATURE [App::DocumentObjectGroupPython] C_element100  label="C_element : 0.856"  # scripted group (container) (typed FeaturePython)
  n = 0.856289
FEATURE [App::DocumentObjectGroupPython] G4_RUBBER_BUTYL  # scripted group (container) (typed FeaturePython)
  Dunit = g/cm3
  Dvalue = 0.92
  Group = -> [H_element092,C_element100]
  conduct = 2
  density = 1
  expand = 3
  formula = G4_RUBBER_BUTYL
  name = G4_RUBBER_BUTYL
  specific = 4
FEATURE [App::DocumentObjectGroupPython] H_element093  label="H_element : 0.118"  # scripted group (container) (typed FeaturePython)
  n = 0.118371
FEATURE [App::DocumentObjectGroupPython] C_element101  label="C_element : 0.882"  # scripted group (container) (typed FeaturePython)
  n = 0.881629
FEATURE [App::DocumentObjectGroupPython] G4_RUBBER_NATURAL  # scripted group (container) (typed FeaturePython)
  Dunit = g/cm3
  Dvalue = 0.92
  Group = -> [H_element093,C_element101]
  conduct = 2
  density = 1
  expand = 3
  formula = G4_RUBBER_NATURAL
  name = G4_RUBBER_NATURAL
  specific = 4
FEATURE [App::DocumentObjectGroupPython] H_element094  label="H_element : 0.145"  # scripted group (container) (typed FeaturePython)
  n = 0.05692
FEATURE [App::DocumentObjectGroupPython] C_element102  label="C_element : 0.543"  # scripted group (container) (typed FeaturePython)
  n = 0.542646
FEATURE [App::DocumentObjectGroupPython] Cl_element021  label="Cl_element : 0.400"  # scripted group (container) (typed FeaturePython)
  n = 0.400434
FEATURE [App::DocumentObjectGroupPython] G4_RUBBER_NEOPRENE  # scripted group (container) (typed FeaturePython)
  Dunit = g/cm3
  Dvalue = 1.23
  Group = -> [H_element094,C_element102,Cl_element021]
  conduct = 2
  density = 1
  expand = 3
  formula = G4_RUBBER_NEOPRENE
  name = G4_RUBBER_NEOPRENE
  specific = 4
FEATURE [App::DocumentObjectGroupPython] Si_element006  label="Si_element : 1"  # scripted group (container) (typed FeaturePython)
  n = 1
  ref = Si_element
FEATURE [App::DocumentObjectGroupPython] O_element087  label="O_element : 048"  # scripted group (container) (typed FeaturePython)
  n = 2
  ref = O_element
FEATURE [App::DocumentObjectGroupPython] G4_SILICON_DIOXIDE  # scripted group (container) (typed FeaturePython)
  Dunit = g/cm3
  Dvalue = 2.32
  Group = -> [Si_element006,O_element087]
  conduct = 2
  density = 1
  expand = 3
  formula = G4_SILICON_DIOXIDE
  name = G4_SILICON_DIOXIDE
  specific = 4
FEATURE [App::DocumentObjectGroupPython] Ag_element002  label="Ag_element : 1"  # scripted group (container) (typed FeaturePython)
  n = 1
  ref = Ag_element
FEATURE [App::DocumentObjectGroupPython] Br_element005  label="Br_element : 003"  # scripted group (container) (typed FeaturePython)
  n = 1
  ref = Br_element
FEATURE [App::DocumentObjectGroupPython] G4_SILVER_BROMIDE  # scripted group (container) (typed FeaturePython)
  Dunit = g/cm3
  Dvalue = 6.473
  Group = -> [Ag_element002,Br_element005]
  conduct = 2
  density = 1
  expand = 3
  formula = G4_SILVER_BROMIDE
  name = G4_SILVER_BROMIDE
  specific = 4
FEATURE [App::DocumentObjectGroupPython] Ag_element003  label="Ag_element : 002"  # scripted group (container) (typed FeaturePython)
  n = 1
  ref = Ag_element
FEATURE [App::DocumentObjectGroupPython] Cl_element022  label="Cl_element : 011"  # scripted group (container) (typed FeaturePython)
  n = 1
  ref = Cl_element
FEATURE [App::DocumentObjectGroupPython] G4_SILVER_CHLORIDE  # scripted group (container) (typed FeaturePython)
  Dunit = g/cm3
  Dvalue = 5.56
  Group = -> [Ag_element003,Cl_element022]
  conduct = 2
  density = 1
  expand = 3
  formula = G4_SILVER_CHLORIDE
  name = G4_SILVER_CHLORIDE
  specific = 4
FEATURE [App::DocumentObjectGroupPython] Br_element006  label="Br_element : 0.423"  # scripted group (container) (typed FeaturePython)
  n = 0.422895
FEATURE [App::DocumentObjectGroupPython] Ag_element004  label="Ag_element : 0.574"  # scripted group (container) (typed FeaturePython)
  n = 0.573748
FEATURE [App::DocumentObjectGroupPython] I_element007  label="I_element : 0.649"  # scripted group (container) (typed FeaturePython)
  n = 0.003357
FEATURE [App::DocumentObjectGroupPython] G4_SILVER_HALIDES  # scripted group (container) (typed FeaturePython)
  Dunit = g/cm3
  Dvalue = 6.47
  Group = -> [Br_element006,Ag_element004,I_element007]
  conduct = 2
  density = 1
  expand = 3
  formula = G4_SILVER_HALIDES
  name = G4_SILVER_HALIDES
  specific = 4
FEATURE [App::DocumentObjectGroupPython] Ag_element005  label="Ag_element : 003"  # scripted group (container) (typed FeaturePython)
  n = 1
  ref = Ag_element
FEATURE [App::DocumentObjectGroupPython] I_element008  label="I_element : 004"  # scripted group (container) (typed FeaturePython)
  n = 1
  ref = I_element
FEATURE [App::DocumentObjectGroupPython] G4_SILVER_IODIDE  # scripted group (container) (typed FeaturePython)
  Dunit = g/cm3
  Dvalue = 6.01
  Group = -> [Ag_element005,I_element008]
  conduct = 2
  density = 1
  expand = 3
  formula = G4_SILVER_IODIDE
  name = G4_SILVER_IODIDE
  specific = 4
FEATURE [App::DocumentObjectGroupPython] H_element095  label="H_element : 0.100"  # scripted group (container) (typed FeaturePython)
  n = 0.1
FEATURE [App::DocumentObjectGroupPython] C_element103  label="C_element : 0.204"  # scripted group (container) (typed FeaturePython)
  n = 0.204
FEATURE [App::DocumentObjectGroupPython] N_element039  label="N_element : 0.759"  # scripted group (container) (typed FeaturePython)
  n = 0.042
FEATURE [App::DocumentObjectGroupPython] O_element088  label="O_element : 0.645"  # scripted group (container) (typed FeaturePython)
  n = 0.645
FEATURE [App::DocumentObjectGroupPython] Na_element013  label="Na_element : 0.100"  # scripted group (container) (typed FeaturePython)
  n = 0.002
FEATURE [App::DocumentObjectGroupPython] P_element009  label="P_element : 0.107"  # scripted group (container) (typed FeaturePython)
  n = 0.001
FEATURE [App::DocumentObjectGroupPython] S_element020  label="S_element : 0.021"  # scripted group (container) (typed FeaturePython)
  n = 0.002
FEATURE [App::DocumentObjectGroupPython] Cl_element023  label="Cl_element : 0.590"  # scripted group (container) (typed FeaturePython)
  n = 0.003
FEATURE [App::DocumentObjectGroupPython] K_element010  label="K_element : 0.001"  # scripted group (container) (typed FeaturePython)
  n = 0.001
FEATURE [App::DocumentObjectGroupPython] G4_SKIN_ICRP  # scripted group (container) (typed FeaturePython)
  Dunit = g/cm3
  Dvalue = 1.09
  Group = -> [H_element095,C_element103,N_element039,O_element088,Na_element013,P_element009,S_element020,Cl_element023,K_element010]
  conduct = 2
  density = 1
  expand = 3
  formula = G4_SKIN_ICRP
  name = G4_SKIN_ICRP
  specific = 4
FEATURE [App::DocumentObjectGroupPython] Na_element014  label="Na_element : 2"  # scripted group (container) (typed FeaturePython)
  n = 2
  ref = Na_element
FEATURE [App::DocumentObjectGroupPython] C_element104  label="C_element : 058"  # scripted group (container) (typed FeaturePython)
  n = 1
  ref = C_element
FEATURE [App::DocumentObjectGroupPython] O_element089  label="O_element : 049"  # scripted group (container) (typed FeaturePython)
  n = 3
  ref = O_element
FEATURE [App::DocumentObjectGroupPython] G4_SODIUM_CARBONATE  # scripted group (container) (typed FeaturePython)
  Dunit = g/cm3
  Dvalue = 2.532
  Group = -> [Na_element014,C_element104,O_element089]
  conduct = 2
  density = 1
  expand = 3
  formula = G4_SODIUM_CARBONATE
  name = G4_SODIUM_CARBONATE
  specific = 4
FEATURE [App::DocumentObjectGroupPython] Na_element015  label="Na_element : 1"  # scripted group (container) (typed FeaturePython)
  n = 1
  ref = Na_element
FEATURE [App::DocumentObjectGroupPython] I_element009  label="I_element : 005"  # scripted group (container) (typed FeaturePython)
  n = 1
  ref = I_element
FEATURE [App::DocumentObjectGroupPython] G4_SODIUM_IODIDE  # scripted group (container) (typed FeaturePython)
  Dunit = g/cm3
  Dvalue = 3.667
  Group = -> [Na_element015,I_element009]
  conduct = 2
  density = 1
  expand = 3
  formula = G4_SODIUM_IODIDE
  name = G4_SODIUM_IODIDE
  specific = 4
FEATURE [App::DocumentObjectGroupPython] Na_element016  label="Na_element : 003"  # scripted group (container) (typed FeaturePython)
  n = 2
  ref = Na_element
FEATURE [App::DocumentObjectGroupPython] O_element090  label="O_element : 050"  # scripted group (container) (typed FeaturePython)
  n = 1
  ref = O_element
FEATURE [App::DocumentObjectGroupPython] G4_SODIUM_MONOXIDE  # scripted group (container) (typed FeaturePython)
  Dunit = g/cm3
  Dvalue = 2.27
  Group = -> [Na_element016,O_element090]
  conduct = 2
  density = 1
  expand = 3
  formula = G4_SODIUM_MONOXIDE
  name = G4_SODIUM_MONOXIDE
  specific = 4
FEATURE [App::DocumentObjectGroupPython] Na_element017  label="Na_element : 004"  # scripted group (container) (typed FeaturePython)
  n = 1
  ref = Na_element
FEATURE [App::DocumentObjectGroupPython] N_element040  label="N_element : 018"  # scripted group (container) (typed FeaturePython)
  n = 1
  ref = N_element
FEATURE [App::DocumentObjectGroupPython] O_element091  label="O_element : 051"  # scripted group (container) (typed FeaturePython)
  n = 3
  ref = O_element
FEATURE [App::DocumentObjectGroupPython] G4_SODIUM_NITRATE  # scripted group (container) (typed FeaturePython)
  Dunit = g/cm3
  Dvalue = 2.261
  Group = -> [Na_element017,N_element040,O_element091]
  conduct = 2
  density = 1
  expand = 3
  formula = G4_SODIUM_NITRATE
  name = G4_SODIUM_NITRATE
  specific = 4
FEATURE [App::DocumentObjectGroupPython] C_element105  label="C_element : 059"  # scripted group (container) (typed FeaturePython)
  n = 14
  ref = C_element
FEATURE [App::DocumentObjectGroupPython] H_element096  label="H_element : 053"  # scripted group (container) (typed FeaturePython)
  n = 12
  ref = H_element
FEATURE [App::DocumentObjectGroupPython] G4_STILBENE  # scripted group (container) (typed FeaturePython)
  Dunit = g/cm3
  Dvalue = 0.9707
  Group = -> [C_element105,H_element096]
  conduct = 2
  density = 1
  expand = 3
  formula = G4_STILBENE
  name = G4_STILBENE
  specific = 4
FEATURE [App::DocumentObjectGroupPython] C_element106  label="C_element : 12"  # scripted group (container) (typed FeaturePython)
  n = 12
  ref = C_element
FEATURE [App::DocumentObjectGroupPython] H_element097  label="H_element : 22"  # scripted group (container) (typed FeaturePython)
  n = 22
  ref = H_element
FEATURE [App::DocumentObjectGroupPython] O_element092  label="O_element : 11"  # scripted group (container) (typed FeaturePython)
  n = 11
  ref = O_element
FEATURE [App::DocumentObjectGroupPython] G4_SUCROSE  # scripted group (container) (typed FeaturePython)
  Dunit = g/cm3
  Dvalue = 1.5805
  Group = -> [C_element106,H_element097,O_element092]
  conduct = 2
  density = 1
  expand = 3
  formula = G4_SUCROSE
  name = G4_SUCROSE
  specific = 4
FEATURE [App::DocumentObjectGroupPython] C_element107  label="C_element : 18"  # scripted group (container) (typed FeaturePython)
  n = 18
  ref = C_element
FEATURE [App::DocumentObjectGroupPython] H_element098  label="H_element : 054"  # scripted group (container) (typed FeaturePython)
  n = 14
  ref = H_element
FEATURE [App::DocumentObjectGroupPython] G4_TERPHENYL  # scripted group (container) (typed FeaturePython)
  Dunit = g/cm3
  Dvalue = 1.24
  Group = -> [C_element107,H_element098]
  conduct = 2
  density = 1
  expand = 3
  formula = G4_TERPHENYL
  name = G4_TERPHENYL
  specific = 4
FEATURE [App::DocumentObjectGroupPython] H_element099  label="H_element : 0.146"  # scripted group (container) (typed FeaturePython)
  n = 0.106
FEATURE [App::DocumentObjectGroupPython] C_element108  label="C_element : 0.883"  # scripted group (container) (typed FeaturePython)
  n = 0.099
FEATURE [App::DocumentObjectGroupPython] N_element041  label="N_element : 0.020"  # scripted group (container) (typed FeaturePython)
  n = 0.02
FEATURE [App::DocumentObjectGroupPython] O_element093  label="O_element : 0.766"  # scripted group (container) (typed FeaturePython)
  n = 0.766
FEATURE [App::DocumentObjectGroupPython] Na_element018  label="Na_element : 0.101"  # scripted group (container) (typed FeaturePython)
  n = 0.002
FEATURE [App::DocumentObjectGroupPython] P_element010  label="P_element : 0.108"  # scripted group (container) (typed FeaturePython)
  n = 0.001
FEATURE [App::DocumentObjectGroupPython] S_element021  label="S_element : 0.022"  # scripted group (container) (typed FeaturePython)
  n = 0.002
FEATURE [App::DocumentObjectGroupPython] Cl_element024  label="Cl_element : 0.002"  # scripted group (container) (typed FeaturePython)
  n = 0.002
FEATURE [App::DocumentObjectGroupPython] K_element011  label="K_element : 0.017"  # scripted group (container) (typed FeaturePython)
  n = 0.002
FEATURE [App::DocumentObjectGroupPython] G4_TESTIS_ICRP  # scripted group (container) (typed FeaturePython)
  Dunit = g/cm3
  Dvalue = 1.04
  Group = -> [H_element099,C_element108,N_element041,O_element093,Na_element018,P_element010,S_element021,Cl_element024,K_element011]
  conduct = 2
  density = 1
  expand = 3
  formula = G4_TESTIS_ICRP
  name = G4_TESTIS_ICRP
  specific = 4
FEATURE [App::DocumentObjectGroupPython] C_element109  label="C_element : 060"  # scripted group (container) (typed FeaturePython)
  n = 2
  ref = C_element
FEATURE [App::DocumentObjectGroupPython] Cl_element025  label="Cl_element : 012"  # scripted group (container) (typed FeaturePython)
  n = 4
  ref = Cl_element
FEATURE [App::DocumentObjectGroupPython] G4_TETRACHLOROETHYLENE  # scripted group (container) (typed FeaturePython)
  Dunit = g/cm3
  Dvalue = 1.625
  Group = -> [C_element109,Cl_element025]
  conduct = 2
  density = 1
  expand = 3
  formula = G4_TETRACHLOROETHYLENE
  name = G4_TETRACHLOROETHYLENE
  specific = 4
FEATURE [App::DocumentObjectGroupPython] Tl_element001  label="Tl_element : 1"  # scripted group (container) (typed FeaturePython)
  n = 1
  ref = Tl_element
FEATURE [App::DocumentObjectGroupPython] Cl_element026  label="Cl_element : 013"  # scripted group (container) (typed FeaturePython)
  n = 1
  ref = Cl_element
FEATURE [App::DocumentObjectGroupPython] G4_THALLIUM_CHLORIDE  # scripted group (container) (typed FeaturePython)
  Dunit = g/cm3
  Dvalue = 7.004
  Group = -> [Tl_element001,Cl_element026]
  conduct = 2
  density = 1
  expand = 3
  formula = G4_THALLIUM_CHLORIDE
  name = G4_THALLIUM_CHLORIDE
  specific = 4
FEATURE [App::DocumentObjectGroupPython] H_element100  label="H_element : 0.147"  # scripted group (container) (typed FeaturePython)
  n = 0.105
FEATURE [App::DocumentObjectGroupPython] C_element110  label="C_element : 0.256"  # scripted group (container) (typed FeaturePython)
  n = 0.256
FEATURE [App::DocumentObjectGroupPython] N_element042  label="N_element : 0.760"  # scripted group (container) (typed FeaturePython)
  n = 0.027
FEATURE [App::DocumentObjectGroupPython] O_element094  label="O_element : 0.602"  # scripted group (container) (typed FeaturePython)
  n = 0.602
FEATURE [App::DocumentObjectGroupPython] Na_element019  label="Na_element : 0.102"  # scripted group (container) (typed FeaturePython)
  n = 0.001
FEATURE [App::DocumentObjectGroupPython] P_element011  label="P_element : 0.109"  # scripted group (container) (typed FeaturePython)
  n = 0.002
FEATURE [App::DocumentObjectGroupPython] S_element022  label="S_element : 0.023"  # scripted group (container) (typed FeaturePython)
  n = 0.003
FEATURE [App::DocumentObjectGroupPython] Cl_element027  label="Cl_element : 0.591"  # scripted group (container) (typed FeaturePython)
  n = 0.002
FEATURE [App::DocumentObjectGroupPython] K_element012  label="K_element : 0.018"  # scripted group (container) (typed FeaturePython)
  n = 0.002
FEATURE [App::DocumentObjectGroupPython] G4_TISSUE_SOFT_ICRP  # scripted group (container) (typed FeaturePython)
  Dunit = g/cm3
  Dvalue = 1.03
  Group = -> [H_element100,C_element110,N_element042,O_element094,Na_element019,P_element011,S_element022,Cl_element027,K_element012]
  conduct = 2
  density = 1
  expand = 3
  formula = G4_TISSUE_SOFT_ICRP
  name = G4_TISSUE_SOFT_ICRP
  specific = 4
FEATURE [App::DocumentObjectGroupPython] H_element101  label="H_element : 0.148"  # scripted group (container) (typed FeaturePython)
  n = 0.101
FEATURE [App::DocumentObjectGroupPython] C_element111  label="C_element : 0.111"  # scripted group (container) (typed FeaturePython)
  n = 0.111
FEATURE [App::DocumentObjectGroupPython] N_element043  label="N_element : 0.026"  # scripted group (container) (typed FeaturePython)
  n = 0.026
FEATURE [App::DocumentObjectGroupPython] O_element095  label="O_element : 0.762"  # scripted group (container) (typed FeaturePython)
  n = 0.762
FEATURE [App::DocumentObjectGroupPython] G4_TISSUE_SOFT_ICRU_4  label="G4_TISSUE_SOFT_ICRU-4"  # scripted group (container) (typed FeaturePython)
  Dunit = g/cm3
  Dvalue = 1
  Group = -> [H_element101,C_element111,N_element043,O_element095]
  conduct = 2
  density = 1
  expand = 3
  formula = G4_TISSUE_SOFT_ICRU-4
  name = G4_TISSUE_SOFT_ICRU-4
  specific = 4
FEATURE [App::DocumentObjectGroupPython] H_element102  label="H_element : 0.149"  # scripted group (container) (typed FeaturePython)
  n = 0.101869
FEATURE [App::DocumentObjectGroupPython] C_element112  label="C_element : 0.456"  # scripted group (container) (typed FeaturePython)
  n = 0.456179
FEATURE [App::DocumentObjectGroupPython] N_element044  label="N_element : 0.761"  # scripted group (container) (typed FeaturePython)
  n = 0.035172
FEATURE [App::DocumentObjectGroupPython] O_element096  label="O_element : 0.407"  # scripted group (container) (typed FeaturePython)
  n = 0.40678
FEATURE [App::DocumentObjectGroupPython] G4_TISSUE_METHANE  label="G4_TISSUE-METHANE"  # scripted group (container) (typed FeaturePython)
  Dunit = g/cm3
  Dvalue = 0.00106409
  Group = -> [H_element102,C_element112,N_element044,O_element096]
  conduct = 2
  density = 1
  expand = 3
  formula = G4_TISSUE-METHANE
  name = G4_TISSUE-METHANE
  specific = 4
FEATURE [App::DocumentObjectGroupPython] H_element103  label="H_element : 0.103"  # scripted group (container) (typed FeaturePython)
  n = 0.102672
FEATURE [App::DocumentObjectGroupPython] C_element113  label="C_element : 0.569"  # scripted group (container) (typed FeaturePython)
  n = 0.56894
FEATURE [App::DocumentObjectGroupPython] N_element045  label="N_element : 0.762"  # scripted group (container) (typed FeaturePython)
  n = 0.035022
FEATURE [App::DocumentObjectGroupPython] O_element097  label="O_element : 0.293"  # scripted group (container) (typed FeaturePython)
  n = 0.293366
FEATURE [App::DocumentObjectGroupPython] G4_TISSUE_PROPANE  label="G4_TISSUE-PROPANE"  # scripted group (container) (typed FeaturePython)
  Dunit = g/cm3
  Dvalue = 0.00182628
  Group = -> [H_element103,C_element113,N_element045,O_element097]
  conduct = 2
  density = 1
  expand = 3
  formula = G4_TISSUE-PROPANE
  name = G4_TISSUE-PROPANE
  specific = 4
FEATURE [App::DocumentObjectGroupPython] Ti_element003  label="Ti_element : 1"  # scripted group (container) (typed FeaturePython)
  n = 1
  ref = Ti_element
FEATURE [App::DocumentObjectGroupPython] O_element098  label="O_element : 052"  # scripted group (container) (typed FeaturePython)
  n = 2
  ref = O_element
FEATURE [App::DocumentObjectGroupPython] G4_TITANIUM_DIOXIDE  # scripted group (container) (typed FeaturePython)
  Dunit = g/cm3
  Dvalue = 4.26
  Group = -> [Ti_element003,O_element098]
  conduct = 2
  density = 1
  expand = 3
  formula = G4_TITANIUM_DIOXIDE
  name = G4_TITANIUM_DIOXIDE
  specific = 4
FEATURE [App::DocumentObjectGroupPython] C_element114  label="C_element : 061"  # scripted group (container) (typed FeaturePython)
  n = 7
  ref = C_element
FEATURE [App::DocumentObjectGroupPython] H_element104  label="H_element : 055"  # scripted group (container) (typed FeaturePython)
  n = 8
  ref = H_element
FEATURE [App::DocumentObjectGroupPython] G4_TOLUENE  # scripted group (container) (typed FeaturePython)
  Dunit = g/cm3
  Dvalue = 0.8669
  Group = -> [C_element114,H_element104]
  conduct = 2
  density = 1
  expand = 3
  formula = G4_TOLUENE
  name = G4_TOLUENE
  specific = 4
FEATURE [App::DocumentObjectGroupPython] C_element115  label="C_element : 062"  # scripted group (container) (typed FeaturePython)
  n = 2
  ref = C_element
FEATURE [App::DocumentObjectGroupPython] H_element105  label="H_element : 056"  # scripted group (container) (typed FeaturePython)
  n = 1
  ref = H_element
FEATURE [App::DocumentObjectGroupPython] Cl_element028  label="Cl_element : 014"  # scripted group (container) (typed FeaturePython)
  n = 3
  ref = Cl_element
FEATURE [App::DocumentObjectGroupPython] G4_TRICHLOROETHYLENE  # scripted group (container) (typed FeaturePython)
  Dunit = g/cm3
  Dvalue = 1.46
  Group = -> [C_element115,H_element105,Cl_element028]
  conduct = 2
  density = 1
  expand = 3
  formula = G4_TRICHLOROETHYLENE
  name = G4_TRICHLOROETHYLENE
  specific = 4
FEATURE [App::DocumentObjectGroupPython] C_element116  label="C_element : 063"  # scripted group (container) (typed FeaturePython)
  n = 6
  ref = C_element
FEATURE [App::DocumentObjectGroupPython] H_element106  label="H_element : 15"  # scripted group (container) (typed FeaturePython)
  n = 15
  ref = H_element
FEATURE [App::DocumentObjectGroupPython] O_element099  label="O_element : 053"  # scripted group (container) (typed FeaturePython)
  n = 4
  ref = O_element
FEATURE [App::DocumentObjectGroupPython] P_element012  label="P_element : 1"  # scripted group (container) (typed FeaturePython)
  n = 1
  ref = P_element
FEATURE [App::DocumentObjectGroupPython] G4_TRIETHYL_PHOSPHATE  # scripted group (container) (typed FeaturePython)
  Dunit = g/cm3
  Dvalue = 1.07
  Group = -> [C_element116,H_element106,O_element099,P_element012]
  conduct = 2
  density = 1
  expand = 3
  formula = G4_TRIETHYL_PHOSPHATE
  name = G4_TRIETHYL_PHOSPHATE
  specific = 4
FEATURE [App::DocumentObjectGroupPython] W_element003  label="W_element : 003"  # scripted group (container) (typed FeaturePython)
  n = 1
  ref = W_element
FEATURE [App::DocumentObjectGroupPython] F_element017  label="F_element : 6"  # scripted group (container) (typed FeaturePython)
  n = 6
  ref = F_element
FEATURE [App::DocumentObjectGroupPython] G4_TUNGSTEN_HEXAFLUORIDE  # scripted group (container) (typed FeaturePython)
  Dunit = g/cm3
  Dvalue = 2.4
  Group = -> [W_element003,F_element017]
  conduct = 2
  density = 1
  expand = 3
  formula = G4_TUNGSTEN_HEXAFLUORIDE
  name = G4_TUNGSTEN_HEXAFLUORIDE
  specific = 4
FEATURE [App::DocumentObjectGroupPython] U_element001  label="U_element : 1"  # scripted group (container) (typed FeaturePython)
  n = 1
  ref = U_element
FEATURE [App::DocumentObjectGroupPython] C_element117  label="C_element : 064"  # scripted group (container) (typed FeaturePython)
  n = 2
  ref = C_element
FEATURE [App::DocumentObjectGroupPython] G4_URANIUM_DICARBIDE  # scripted group (container) (typed FeaturePython)
  Dunit = g/cm3
  Dvalue = 11.28
  Group = -> [U_element001,C_element117]
  conduct = 2
  density = 1
  expand = 3
  formula = G4_URANIUM_DICARBIDE
  name = G4_URANIUM_DICARBIDE
  specific = 4
FEATURE [App::DocumentObjectGroupPython] U_element002  label="U_element : 002"  # scripted group (container) (typed FeaturePython)
  n = 1
  ref = U_element
FEATURE [App::DocumentObjectGroupPython] C_element118  label="C_element : 065"  # scripted group (container) (typed FeaturePython)
  n = 1
  ref = C_element
FEATURE [App::DocumentObjectGroupPython] G4_URANIUM_MONOCARBIDE  # scripted group (container) (typed FeaturePython)
  Dunit = g/cm3
  Dvalue = 13.63
  Group = -> [U_element002,C_element118]
  conduct = 2
  density = 1
  expand = 3
  formula = G4_URANIUM_MONOCARBIDE
  name = G4_URANIUM_MONOCARBIDE
  specific = 4
FEATURE [App::DocumentObjectGroupPython] U_element003  label="U_element : 003"  # scripted group (container) (typed FeaturePython)
  n = 1
  ref = U_element
FEATURE [App::DocumentObjectGroupPython] O_element100  label="O_element : 054"  # scripted group (container) (typed FeaturePython)
  n = 2
  ref = O_element
FEATURE [App::DocumentObjectGroupPython] G4_URANIUM_OXIDE  # scripted group (container) (typed FeaturePython)
  Dunit = g/cm3
  Dvalue = 10.96
  Group = -> [U_element003,O_element100]
  conduct = 2
  density = 1
  expand = 3
  formula = G4_URANIUM_OXIDE
  name = G4_URANIUM_OXIDE
  specific = 4
FEATURE [App::DocumentObjectGroupPython] C_element119  label="C_element : 066"  # scripted group (container) (typed FeaturePython)
  n = 1
  ref = C_element
FEATURE [App::DocumentObjectGroupPython] H_element107  label="H_element : 057"  # scripted group (container) (typed FeaturePython)
  n = 4
  ref = H_element
FEATURE [App::DocumentObjectGroupPython] N_element046  label="N_element : 019"  # scripted group (container) (typed FeaturePython)
  n = 2
  ref = N_element
FEATURE [App::DocumentObjectGroupPython] O_element101  label="O_element : 055"  # scripted group (container) (typed FeaturePython)
  n = 1
  ref = O_element
FEATURE [App::DocumentObjectGroupPython] G4_UREA  # scripted group (container) (typed FeaturePython)
  Dunit = g/cm3
  Dvalue = 1.323
  Group = -> [C_element119,H_element107,N_element046,O_element101]
  conduct = 2
  density = 1
  expand = 3
  formula = G4_UREA
  name = G4_UREA
  specific = 4
FEATURE [App::DocumentObjectGroupPython] C_element120  label="C_element : 067"  # scripted group (container) (typed FeaturePython)
  n = 5
  ref = C_element
FEATURE [App::DocumentObjectGroupPython] H_element108  label="H_element : 058"  # scripted group (container) (typed FeaturePython)
  n = 11
  ref = H_element
FEATURE [App::DocumentObjectGroupPython] N_element047  label="N_element : 020"  # scripted group (container) (typed FeaturePython)
  n = 1
  ref = N_element
FEATURE [App::DocumentObjectGroupPython] O_element102  label="O_element : 056"  # scripted group (container) (typed FeaturePython)
  n = 2
  ref = O_element
FEATURE [App::DocumentObjectGroupPython] G4_VALINE  # scripted group (container) (typed FeaturePython)
  Dunit = g/cm3
  Dvalue = 1.23
  Group = -> [C_element120,H_element108,N_element047,O_element102]
  conduct = 2
  density = 1
  expand = 3
  formula = G4_VALINE
  name = G4_VALINE
  specific = 4
FEATURE [App::DocumentObjectGroupPython] H_element109  label="H_element : 0.009"  # scripted group (container) (typed FeaturePython)
  n = 0.009417
FEATURE [App::DocumentObjectGroupPython] C_element121  label="C_element : 0.281"  # scripted group (container) (typed FeaturePython)
  n = 0.280555
FEATURE [App::DocumentObjectGroupPython] F_element018  label="F_element : 0.710"  # scripted group (container) (typed FeaturePython)
  n = 0.710028
FEATURE [App::DocumentObjectGroupPython] G4_VITON  # scripted group (container) (typed FeaturePython)
  Dunit = g/cm3
  Dvalue = 1.8
  Group = -> [H_element109,C_element121,F_element018]
  conduct = 2
  density = 1
  expand = 3
  formula = G4_VITON
  name = G4_VITON
  specific = 4
FEATURE [App::DocumentObjectGroupPython] H_element110  label="H_element : 059"  # scripted group (container) (typed FeaturePython)
  n = 2
  ref = H_element
FEATURE [App::DocumentObjectGroupPython] O_element103  label="O_element : 057"  # scripted group (container) (typed FeaturePython)
  n = 1
  ref = O_element
FEATURE [App::DocumentObjectGroupPython] G4_WATER  # scripted group (container) (typed FeaturePython)
  Dunit = g/cm3
  Dvalue = 1
  Group = -> [H_element110,O_element103]
  conduct = 2
  density = 1
  expand = 3
  formula = G4_WATER
  name = G4_WATER
  specific = 4
FEATURE [App::DocumentObjectGroupPython] H_element111  label="H_element : 060"  # scripted group (container) (typed FeaturePython)
  n = 2
  ref = H_element
FEATURE [App::DocumentObjectGroupPython] O_element104  label="O_element : 058"  # scripted group (container) (typed FeaturePython)
  n = 1
  ref = O_element
FEATURE [App::DocumentObjectGroupPython] G4_WATER_VAPOR  # scripted group (container) (typed FeaturePython)
  Dunit = g/cm3
  Dvalue = 0.000756182
  Group = -> [H_element111,O_element104]
  conduct = 2
  density = 1
  expand = 3
  formula = G4_WATER_VAPOR
  name = G4_WATER_VAPOR
  specific = 4
FEATURE [App::DocumentObjectGroupPython] C_element122  label="C_element : 068"  # scripted group (container) (typed FeaturePython)
  n = 8
  ref = C_element
FEATURE [App::DocumentObjectGroupPython] H_element112  label="H_element : 061"  # scripted group (container) (typed FeaturePython)
  n = 10
  ref = H_element
FEATURE [App::DocumentObjectGroupPython] G4_XYLENE  # scripted group (container) (typed FeaturePython)
  Dunit = g/cm3
  Dvalue = 0.87
  Group = -> [C_element122,H_element112]
  conduct = 2
  density = 1
  expand = 3
  formula = G4_XYLENE
  name = G4_XYLENE
  specific = 4
FEATURE [App::DocumentObjectGroupPython] C_element123  label="C_element : 069"  # scripted group (container) (typed FeaturePython)
  n = 1
  ref = C_element
FEATURE [App::DocumentObjectGroupPython] G4_GRAPHITE  # scripted group (container) (typed FeaturePython)
  Dunit = g/cm3
  Dvalue = 2.21
  Group = -> [C_element123]
  conduct = 2
  density = 1
  expand = 3
  formula = G4_GRAPHITE
  name = G4_GRAPHITE
  specific = 4
FEATURE [App::DocumentObjectGroupPython] NIST  # scripted group (container) (typed FeaturePython)
  Group = -> [G4_A_150_TISSUE,G4_ACETONE,G4_ACETYLENE,G4_ADENINE,G4_ADIPOSE_TISSUE_ICRP,G4_AIR,G4_ALANINE,G4_ALUMINUM_OXIDE,G4_AMBER,G4_AMMONIA,G4_ANILINE,G4_ANTHRACENE,G4_B_100_BONE,G4_BAKELITE,G4_BARIUM_FLUORIDE,G4_BARIUM_SULFATE,G4_BENZENE,G4_BERYLLIUM_OXIDE,G4_BGO,G4_BLOOD_ICRP,G4_BONE_COMPACT_ICRU,G4_BONE_CORTICAL_ICRP,G4_BORON_CARBIDE,G4_BORON_OXIDE,G4_BRAIN_ICRP,G4_BUTANE,G4_N_BUTYL_ALCOHOL,G4_C_552,+152 more]
FEATURE [App::DocumentObjectGroupPython] H_element113  label="H_element : 062"  # scripted group (container) (typed FeaturePython)
  n = 1
  ref = H_element
FEATURE [App::DocumentObjectGroupPython] G4_H  # scripted group (container) (typed FeaturePython)
  Dunit = g/cm3
  Dvalue = 8.3748e-05
  Group = -> [H_element113]
  conduct = 2
  density = 1
  expand = 3
  formula = H
  name = G4_H
  specific = 4
FEATURE [App::DocumentObjectGroupPython] He_element001  label="He_element : 1"  # scripted group (container) (typed FeaturePython)
  n = 1
  ref = He_element
FEATURE [App::DocumentObjectGroupPython] G4_He  # scripted group (container) (typed FeaturePython)
  Dunit = g/cm3
  Dvalue = 0.000166322
  Group = -> [He_element001]
  conduct = 2
  density = 1
  expand = 3
  formula = He
  name = G4_He
  specific = 4
FEATURE [App::DocumentObjectGroupPython] Li_element008  label="Li_element : 008"  # scripted group (container) (typed FeaturePython)
  n = 1
  ref = Li_element
FEATURE [App::DocumentObjectGroupPython] G4_Li  # scripted group (container) (typed FeaturePython)
  Dunit = g/cm3
  Dvalue = 0.534
  Group = -> [Li_element008]
  conduct = 2
  density = 1
  expand = 3
  formula = Li
  name = G4_Li
  specific = 4
FEATURE [App::DocumentObjectGroupPython] Be_element002  label="Be_element : 002"  # scripted group (container) (typed FeaturePython)
  n = 1
  ref = Be_element
FEATURE [App::DocumentObjectGroupPython] G4_Be  # scripted group (container) (typed FeaturePython)
  Dunit = g/cm3
  Dvalue = 1.848
  Group = -> [Be_element002]
  conduct = 2
  density = 1
  expand = 3
  formula = Be
  name = G4_Be
  specific = 4
FEATURE [App::DocumentObjectGroupPython] B_element007  label="B_element : 007"  # scripted group (container) (typed FeaturePython)
  n = 1
  ref = B_element
FEATURE [App::DocumentObjectGroupPython] G4_B  # scripted group (container) (typed FeaturePython)
  Dunit = g/cm3
  Dvalue = 2.37
  Group = -> [B_element007]
  conduct = 2
  density = 1
  expand = 3
  formula = B
  name = G4_B
  specific = 4
FEATURE [App::DocumentObjectGroupPython] C_element124  label="C_element : 070"  # scripted group (container) (typed FeaturePython)
  n = 1
  ref = C_element
FEATURE [App::DocumentObjectGroupPython] G4_C  # scripted group (container) (typed FeaturePython)
  Dunit = g/cm3
  Dvalue = 2
  Group = -> [C_element124]
  conduct = 2
  density = 1
  expand = 3
  formula = C
  name = G4_C
  specific = 4
FEATURE [App::DocumentObjectGroupPython] N_element048  label="N_element : 021"  # scripted group (container) (typed FeaturePython)
  n = 1
  ref = N_element
FEATURE [App::DocumentObjectGroupPython] G4_N  # scripted group (container) (typed FeaturePython)
  Dunit = g/cm3
  Dvalue = 0.0011652
  Group = -> [N_element048]
  conduct = 2
  density = 1
  expand = 3
  formula = N
  name = G4_N
  specific = 4
FEATURE [App::DocumentObjectGroupPython] O_element105  label="O_element : 059"  # scripted group (container) (typed FeaturePython)
  n = 1
  ref = O_element
FEATURE [App::DocumentObjectGroupPython] G4_O  # scripted group (container) (typed FeaturePython)
  Dunit = g/cm3
  Dvalue = 0.00133151
  Group = -> [O_element105]
  conduct = 2
  density = 1
  expand = 3
  formula = O
  name = G4_O
  specific = 4
FEATURE [App::DocumentObjectGroupPython] F_element019  label="F_element : 008"  # scripted group (container) (typed FeaturePython)
  n = 1
  ref = F_element
FEATURE [App::DocumentObjectGroupPython] G4_F  # scripted group (container) (typed FeaturePython)
  Dunit = g/cm3
  Dvalue = 0.00158029
  Group = -> [F_element019]
  conduct = 2
  density = 1
  expand = 3
  formula = F
  name = G4_F
  specific = 4
FEATURE [App::DocumentObjectGroupPython] Ne_element001  label="Ne_element : 1"  # scripted group (container) (typed FeaturePython)
  n = 1
  ref = Ne_element
FEATURE [App::DocumentObjectGroupPython] G4_Ne  # scripted group (container) (typed FeaturePython)
  Dunit = g/cm3
  Dvalue = 0.000838505
  Group = -> [Ne_element001]
  conduct = 2
  density = 1
  expand = 3
  formula = Ne
  name = G4_Ne
  specific = 4
FEATURE [App::DocumentObjectGroupPython] Na_element020  label="Na_element : 005"  # scripted group (container) (typed FeaturePython)
  n = 1
  ref = Na_element
FEATURE [App::DocumentObjectGroupPython] G4_Na  # scripted group (container) (typed FeaturePython)
  Dunit = g/cm3
  Dvalue = 0.971
  Group = -> [Na_element020]
  conduct = 2
  density = 1
  expand = 3
  formula = Na
  name = G4_Na
  specific = 4
FEATURE [App::DocumentObjectGroupPython] Mg_element011  label="Mg_element : 005"  # scripted group (container) (typed FeaturePython)
  n = 1
  ref = Mg_element
FEATURE [App::DocumentObjectGroupPython] G4_Mg  # scripted group (container) (typed FeaturePython)
  Dunit = g/cm3
  Dvalue = 1.74
  Group = -> [Mg_element011]
  conduct = 2
  density = 1
  expand = 3
  formula = Mg
  name = G4_Mg
  specific = 4
FEATURE [App::DocumentObjectGroupPython] Al_element004  label="Al_element : 1"  # scripted group (container) (typed FeaturePython)
  n = 1
  ref = Al_element
FEATURE [App::DocumentObjectGroupPython] G4_Al  # scripted group (container) (typed FeaturePython)
  Dunit = g/cm3
  Dvalue = 2.699
  Group = -> [Al_element004]
  conduct = 2
  density = 1
  expand = 3
  formula = Al
  name = G4_Al
  specific = 4
FEATURE [App::DocumentObjectGroupPython] Si_element007  label="Si_element : 002"  # scripted group (container) (typed FeaturePython)
  n = 1
  ref = Si_element
FEATURE [App::DocumentObjectGroupPython] G4_Si  # scripted group (container) (typed FeaturePython)
  Dunit = g/cm3
  Dvalue = 2.33
  Group = -> [Si_element007]
  conduct = 2
  density = 1
  expand = 3
  formula = Si
  name = G4_Si
  specific = 4
FEATURE [App::DocumentObjectGroupPython] P_element013  label="P_element : 002"  # scripted group (container) (typed FeaturePython)
  n = 1
  ref = P_element
FEATURE [App::DocumentObjectGroupPython] G4_P  # scripted group (container) (typed FeaturePython)
  Dunit = g/cm3
  Dvalue = 2.2
  Group = -> [P_element013]
  conduct = 2
  density = 1
  expand = 3
  formula = P
  name = G4_P
  specific = 4
FEATURE [App::DocumentObjectGroupPython] S_element023  label="S_element : 007"  # scripted group (container) (typed FeaturePython)
  n = 1
  ref = S_element
FEATURE [App::DocumentObjectGroupPython] G4_S  # scripted group (container) (typed FeaturePython)
  Dunit = g/cm3
  Dvalue = 2
  Group = -> [S_element023]
  conduct = 2
  density = 1
  expand = 3
  formula = S
  name = G4_S
  specific = 4
FEATURE [App::DocumentObjectGroupPython] Cl_element029  label="Cl_element : 015"  # scripted group (container) (typed FeaturePython)
  n = 1
  ref = Cl_element
FEATURE [App::DocumentObjectGroupPython] G4_Cl  # scripted group (container) (typed FeaturePython)
  Dunit = g/cm3
  Dvalue = 0.00299473
  Group = -> [Cl_element029]
  conduct = 2
  density = 1
  expand = 3
  formula = Cl
  name = G4_Cl
  specific = 4
FEATURE [App::DocumentObjectGroupPython] Ar_element002  label="Ar_element : 1"  # scripted group (container) (typed FeaturePython)
  n = 1
  ref = Ar_element
FEATURE [App::DocumentObjectGroupPython] G4_Ar  # scripted group (container) (typed FeaturePython)
  Dunit = g/cm3
  Dvalue = 0.00166201
  Group = -> [Ar_element002]
  conduct = 2
  density = 1
  expand = 3
  formula = Ar
  name = G4_Ar
  specific = 4
FEATURE [App::DocumentObjectGroupPython] K_element013  label="K_element : 003"  # scripted group (container) (typed FeaturePython)
  n = 1
  ref = K_element
FEATURE [App::DocumentObjectGroupPython] G4_K  # scripted group (container) (typed FeaturePython)
  Dunit = g/cm3
  Dvalue = 0.862
  Group = -> [K_element013]
  conduct = 2
  density = 1
  expand = 3
  formula = K
  name = G4_K
  specific = 4
FEATURE [App::DocumentObjectGroupPython] Ca_element014  label="Ca_element : 007"  # scripted group (container) (typed FeaturePython)
  n = 1
  ref = Ca_element
FEATURE [App::DocumentObjectGroupPython] G4_Ca  # scripted group (container) (typed FeaturePython)
  Dunit = g/cm3
  Dvalue = 1.55
  Group = -> [Ca_element014]
  conduct = 2
  density = 1
  expand = 3
  formula = Ca
  name = G4_Ca
  specific = 4
FEATURE [App::DocumentObjectGroupPython] Sc_element001  label="Sc_element : 1"  # scripted group (container) (typed FeaturePython)
  n = 1
  ref = Sc_element
FEATURE [App::DocumentObjectGroupPython] G4_Sc  # scripted group (container) (typed FeaturePython)
  Dunit = g/cm3
  Dvalue = 2.989
  Group = -> [Sc_element001]
  conduct = 2
  density = 1
  expand = 3
  formula = Sc
  name = G4_Sc
  specific = 4
FEATURE [App::DocumentObjectGroupPython] Ti_element004  label="Ti_element : 002"  # scripted group (container) (typed FeaturePython)
  n = 1
  ref = Ti_element
FEATURE [App::DocumentObjectGroupPython] G4_Ti  # scripted group (container) (typed FeaturePython)
  Dunit = g/cm3
  Dvalue = 4.54
  Group = -> [Ti_element004]
  conduct = 2
  density = 1
  expand = 3
  formula = Ti
  name = G4_Ti
  specific = 4
FEATURE [App::DocumentObjectGroupPython] V_element001  label="V_element : 1"  # scripted group (container) (typed FeaturePython)
  n = 1
  ref = V_element
FEATURE [App::DocumentObjectGroupPython] G4_V  # scripted group (container) (typed FeaturePython)
  Dunit = g/cm3
  Dvalue = 6.11
  Group = -> [V_element001]
  conduct = 2
  density = 1
  expand = 3
  formula = V
  name = G4_V
  specific = 4
FEATURE [App::DocumentObjectGroupPython] Cr_element001  label="Cr_element : 1"  # scripted group (container) (typed FeaturePython)
  n = 1
  ref = Cr_element
FEATURE [App::DocumentObjectGroupPython] G4_Cr  # scripted group (container) (typed FeaturePython)
  Dunit = g/cm3
  Dvalue = 7.18
  Group = -> [Cr_element001]
  conduct = 2
  density = 1
  expand = 3
  formula = Cr
  name = G4_Cr
  specific = 4
FEATURE [App::DocumentObjectGroupPython] Mn_element001  label="Mn_element : 1"  # scripted group (container) (typed FeaturePython)
  n = 1
  ref = Mn_element
FEATURE [App::DocumentObjectGroupPython] G4_Mn  # scripted group (container) (typed FeaturePython)
  Dunit = g/cm3
  Dvalue = 7.44
  Group = -> [Mn_element001]
  conduct = 2
  density = 1
  expand = 3
  formula = Mn
  name = G4_Mn
  specific = 4
FEATURE [App::DocumentObjectGroupPython] Fe_element007  label="Fe_element : 004"  # scripted group (container) (typed FeaturePython)
  n = 1
  ref = Fe_element
FEATURE [App::DocumentObjectGroupPython] G4_Fe  # scripted group (container) (typed FeaturePython)
  Dunit = g/cm3
  Dvalue = 7.874
  Group = -> [Fe_element007]
  conduct = 2
  density = 1
  expand = 3
  formula = Fe
  name = G4_Fe
  specific = 4
FEATURE [App::DocumentObjectGroupPython] Co_element001  label="Co_element : 1"  # scripted group (container) (typed FeaturePython)
  n = 1
  ref = Co_element
FEATURE [App::DocumentObjectGroupPython] G4_Co  # scripted group (container) (typed FeaturePython)
  Dunit = g/cm3
  Dvalue = 8.9
  Group = -> [Co_element001]
  conduct = 2
  density = 1
  expand = 3
  formula = Co
  name = G4_Co
  specific = 4
FEATURE [App::DocumentObjectGroupPython] Ni_element001  label="Ni_element : 1"  # scripted group (container) (typed FeaturePython)
  n = 1
  ref = Ni_element
FEATURE [App::DocumentObjectGroupPython] G4_Ni  # scripted group (container) (typed FeaturePython)
  Dunit = g/cm3
  Dvalue = 8.902
  Group = -> [Ni_element001]
  conduct = 2
  density = 1
  expand = 3
  formula = Ni
  name = G4_Ni
  specific = 4
FEATURE [App::DocumentObjectGroupPython] Cu_element001  label="Cu_element : 1"  # scripted group (container) (typed FeaturePython)
  n = 1
  ref = Cu_element
FEATURE [App::DocumentObjectGroupPython] G4_Cu  # scripted group (container) (typed FeaturePython)
  Dunit = g/cm3
  Dvalue = 8.96
  Group = -> [Cu_element001]
  conduct = 2
  density = 1
  expand = 3
  formula = Cu
  name = G4_Cu
  specific = 4
FEATURE [App::DocumentObjectGroupPython] Zn_element001  label="Zn_element : 1"  # scripted group (container) (typed FeaturePython)
  n = 1
  ref = Zn_element
FEATURE [App::DocumentObjectGroupPython] G4_Zn  # scripted group (container) (typed FeaturePython)
  Dunit = g/cm3
  Dvalue = 7.133
  Group = -> [Zn_element001]
  conduct = 2
  density = 1
  expand = 3
  formula = Zn
  name = G4_Zn
  specific = 4
FEATURE [App::DocumentObjectGroupPython] Ga_element002  label="Ga_element : 002"  # scripted group (container) (typed FeaturePython)
  n = 1
  ref = Ga_element
FEATURE [App::DocumentObjectGroupPython] G4_Ga  # scripted group (container) (typed FeaturePython)
  Dunit = g/cm3
  Dvalue = 5.904
  Group = -> [Ga_element002]
  conduct = 2
  density = 1
  expand = 3
  formula = Ga
  name = G4_Ga
  specific = 4
FEATURE [App::DocumentObjectGroupPython] Ge_element002  label="Ge_element : 1"  # scripted group (container) (typed FeaturePython)
  n = 1
  ref = Ge_element
FEATURE [App::DocumentObjectGroupPython] G4_Ge  # scripted group (container) (typed FeaturePython)
  Dunit = g/cm3
  Dvalue = 5.323
  Group = -> [Ge_element002]
  conduct = 2
  density = 1
  expand = 3
  formula = Ge
  name = G4_Ge
  specific = 4
FEATURE [App::DocumentObjectGroupPython] As_element003  label="As_element : 002"  # scripted group (container) (typed FeaturePython)
  n = 1
  ref = As_element
FEATURE [App::DocumentObjectGroupPython] G4_As  # scripted group (container) (typed FeaturePython)
  Dunit = g/cm3
  Dvalue = 5.73
  Group = -> [As_element003]
  conduct = 2
  density = 1
  expand = 3
  formula = As
  name = G4_As
  specific = 4
FEATURE [App::DocumentObjectGroupPython] Se_element001  label="Se_element : 1"  # scripted group (container) (typed FeaturePython)
  n = 1
  ref = Se_element
FEATURE [App::DocumentObjectGroupPython] G4_Se  # scripted group (container) (typed FeaturePython)
  Dunit = g/cm3
  Dvalue = 4.5
  Group = -> [Se_element001]
  conduct = 2
  density = 1
  expand = 3
  formula = Se
  name = G4_Se
  specific = 4
FEATURE [App::DocumentObjectGroupPython] Br_element007  label="Br_element : 004"  # scripted group (container) (typed FeaturePython)
  n = 1
  ref = Br_element
FEATURE [App::DocumentObjectGroupPython] G4_Br  # scripted group (container) (typed FeaturePython)
  Dunit = g/cm3
  Dvalue = 0.0070721
  Group = -> [Br_element007]
  conduct = 2
  density = 1
  expand = 3
  formula = Br
  name = G4_Br
  specific = 4
FEATURE [App::DocumentObjectGroupPython] Kr_element001  label="Kr_element : 1"  # scripted group (container) (typed FeaturePython)
  n = 1
  ref = Kr_element
FEATURE [App::DocumentObjectGroupPython] G4_Kr  # scripted group (container) (typed FeaturePython)
  Dunit = g/cm3
  Dvalue = 0.00347832
  Group = -> [Kr_element001]
  conduct = 2
  density = 1
  expand = 3
  formula = Kr
  name = G4_Kr
  specific = 4
FEATURE [App::DocumentObjectGroupPython] Rb_element001  label="Rb_element : 1"  # scripted group (container) (typed FeaturePython)
  n = 1
  ref = Rb_element
FEATURE [App::DocumentObjectGroupPython] G4_Rb  # scripted group (container) (typed FeaturePython)
  Dunit = g/cm3
  Dvalue = 1.532
  Group = -> [Rb_element001]
  conduct = 2
  density = 1
  expand = 3
  formula = Rb
  name = G4_Rb
  specific = 4
FEATURE [App::DocumentObjectGroupPython] Sr_element001  label="Sr_element : 1"  # scripted group (container) (typed FeaturePython)
  n = 1
  ref = Sr_element
FEATURE [App::DocumentObjectGroupPython] G4_Sr  # scripted group (container) (typed FeaturePython)
  Dunit = g/cm3
  Dvalue = 2.54
  Group = -> [Sr_element001]
  conduct = 2
  density = 1
  expand = 3
  formula = Sr
  name = G4_Sr
  specific = 4
FEATURE [App::DocumentObjectGroupPython] Y_element001  label="Y_element : 1"  # scripted group (container) (typed FeaturePython)
  n = 1
  ref = Y_element
FEATURE [App::DocumentObjectGroupPython] G4_Y  # scripted group (container) (typed FeaturePython)
  Dunit = g/cm3
  Dvalue = 4.469
  Group = -> [Y_element001]
  conduct = 2
  density = 1
  expand = 3
  formula = Y
  name = G4_Y
  specific = 4
FEATURE [App::DocumentObjectGroupPython] Zr_element001  label="Zr_element : 1"  # scripted group (container) (typed FeaturePython)
  n = 1
  ref = Zr_element
FEATURE [App::DocumentObjectGroupPython] G4_Zr  # scripted group (container) (typed FeaturePython)
  Dunit = g/cm3
  Dvalue = 6.506
  Group = -> [Zr_element001]
  conduct = 2
  density = 1
  expand = 3
  formula = Zr
  name = G4_Zr
  specific = 4
FEATURE [App::DocumentObjectGroupPython] Nb_element001  label="Nb_element : 1"  # scripted group (container) (typed FeaturePython)
  n = 1
  ref = Nb_element
FEATURE [App::DocumentObjectGroupPython] G4_Nb  # scripted group (container) (typed FeaturePython)
  Dunit = g/cm3
  Dvalue = 8.57
  Group = -> [Nb_element001]
  conduct = 2
  density = 1
  expand = 3
  formula = Nb
  name = G4_Nb
  specific = 4
FEATURE [App::DocumentObjectGroupPython] Mo_element001  label="Mo_element : 1"  # scripted group (container) (typed FeaturePython)
  n = 1
  ref = Mo_element
FEATURE [App::DocumentObjectGroupPython] G4_Mo  # scripted group (container) (typed FeaturePython)
  Dunit = g/cm3
  Dvalue = 10.22
  Group = -> [Mo_element001]
  conduct = 2
  density = 1
  expand = 3
  formula = Mo
  name = G4_Mo
  specific = 4
FEATURE [App::DocumentObjectGroupPython] Tc_element001  label="Tc_element : 1"  # scripted group (container) (typed FeaturePython)
  n = 1
  ref = Tc_element
FEATURE [App::DocumentObjectGroupPython] G4_Tc  # scripted group (container) (typed FeaturePython)
  Dunit = g/cm3
  Dvalue = 11.5
  Group = -> [Tc_element001]
  conduct = 2
  density = 1
  expand = 3
  formula = Tc
  name = G4_Tc
  specific = 4
FEATURE [App::DocumentObjectGroupPython] Ru_element001  label="Ru_element : 1"  # scripted group (container) (typed FeaturePython)
  n = 1
  ref = Ru_element
FEATURE [App::DocumentObjectGroupPython] G4_Ru  # scripted group (container) (typed FeaturePython)
  Dunit = g/cm3
  Dvalue = 12.41
  Group = -> [Ru_element001]
  conduct = 2
  density = 1
  expand = 3
  formula = Ru
  name = G4_Ru
  specific = 4
FEATURE [App::DocumentObjectGroupPython] Rh_element001  label="Rh_element : 1"  # scripted group (container) (typed FeaturePython)
  n = 1
  ref = Rh_element
FEATURE [App::DocumentObjectGroupPython] G4_Rh  # scripted group (container) (typed FeaturePython)
  Dunit = g/cm3
  Dvalue = 12.41
  Group = -> [Rh_element001]
  conduct = 2
  density = 1
  expand = 3
  formula = Rh
  name = G4_Rh
  specific = 4
FEATURE [App::DocumentObjectGroupPython] Pd_element001  label="Pd_element : 1"  # scripted group (container) (typed FeaturePython)
  n = 1
  ref = Pd_element
FEATURE [App::DocumentObjectGroupPython] G4_Pd  # scripted group (container) (typed FeaturePython)
  Dunit = g/cm3
  Dvalue = 12.02
  Group = -> [Pd_element001]
  conduct = 2
  density = 1
  expand = 3
  formula = Pd
  name = G4_Pd
  specific = 4
FEATURE [App::DocumentObjectGroupPython] Ag_element006  label="Ag_element : 004"  # scripted group (container) (typed FeaturePython)
  n = 1
  ref = Ag_element
FEATURE [App::DocumentObjectGroupPython] G4_Ag  # scripted group (container) (typed FeaturePython)
  Dunit = g/cm3
  Dvalue = 10.5
  Group = -> [Ag_element006]
  conduct = 2
  density = 1
  expand = 3
  formula = Ag
  name = G4_Ag
  specific = 4
FEATURE [App::DocumentObjectGroupPython] Cd_element003  label="Cd_element : 003"  # scripted group (container) (typed FeaturePython)
  n = 1
  ref = Cd_element
FEATURE [App::DocumentObjectGroupPython] G4_Cd  # scripted group (container) (typed FeaturePython)
  Dunit = g/cm3
  Dvalue = 8.65
  Group = -> [Cd_element003]
  conduct = 2
  density = 1
  expand = 3
  formula = Cd
  name = G4_Cd
  specific = 4
FEATURE [App::DocumentObjectGroupPython] In_element001  label="In_element : 1"  # scripted group (container) (typed FeaturePython)
  n = 1
  ref = In_element
FEATURE [App::DocumentObjectGroupPython] G4_In  # scripted group (container) (typed FeaturePython)
  Dunit = g/cm3
  Dvalue = 7.31
  Group = -> [In_element001]
  conduct = 2
  density = 1
  expand = 3
  formula = In
  name = G4_In
  specific = 4
FEATURE [App::DocumentObjectGroupPython] Sn_element001  label="Sn_element : 1"  # scripted group (container) (typed FeaturePython)
  n = 1
  ref = Sn_element
FEATURE [App::DocumentObjectGroupPython] G4_Sn  # scripted group (container) (typed FeaturePython)
  Dunit = g/cm3
  Dvalue = 7.31
  Group = -> [Sn_element001]
  conduct = 2
  density = 1
  expand = 3
  formula = Sn
  name = G4_Sn
  specific = 4
FEATURE [App::DocumentObjectGroupPython] Sb_element001  label="Sb_element : 1"  # scripted group (container) (typed FeaturePython)
  n = 1
  ref = Sb_element
FEATURE [App::DocumentObjectGroupPython] G4_Sb  # scripted group (container) (typed FeaturePython)
  Dunit = g/cm3
  Dvalue = 6.691
  Group = -> [Sb_element001]
  conduct = 2
  density = 1
  expand = 3
  formula = Sb
  name = G4_Sb
  specific = 4
FEATURE [App::DocumentObjectGroupPython] Te_element002  label="Te_element : 002"  # scripted group (container) (typed FeaturePython)
  n = 1
  ref = Te_element
FEATURE [App::DocumentObjectGroupPython] G4_Te  # scripted group (container) (typed FeaturePython)
  Dunit = g/cm3
  Dvalue = 6.24
  Group = -> [Te_element002]
  conduct = 2
  density = 1
  expand = 3
  formula = Te
  name = G4_Te
  specific = 4
FEATURE [App::DocumentObjectGroupPython] I_element010  label="I_element : 006"  # scripted group (container) (typed FeaturePython)
  n = 1
  ref = I_element
FEATURE [App::DocumentObjectGroupPython] G4_I  # scripted group (container) (typed FeaturePython)
  Dunit = g/cm3
  Dvalue = 4.93
  Group = -> [I_element010]
  conduct = 2
  density = 1
  expand = 3
  formula = I
  name = G4_I
  specific = 4
FEATURE [App::DocumentObjectGroupPython] Xe_element001  label="Xe_element : 1"  # scripted group (container) (typed FeaturePython)
  n = 1
  ref = Xe_element
FEATURE [App::DocumentObjectGroupPython] G4_Xe  # scripted group (container) (typed FeaturePython)
  Dunit = g/cm3
  Dvalue = 0.00548536
  Group = -> [Xe_element001]
  conduct = 2
  density = 1
  expand = 3
  formula = Xe
  name = G4_Xe
  specific = 4
FEATURE [App::DocumentObjectGroupPython] Cs_element003  label="Cs_element : 003"  # scripted group (container) (typed FeaturePython)
  n = 1
  ref = Cs_element
FEATURE [App::DocumentObjectGroupPython] G4_Cs  # scripted group (container) (typed FeaturePython)
  Dunit = g/cm3
  Dvalue = 1.873
  Group = -> [Cs_element003]
  conduct = 2
  density = 1
  expand = 3
  formula = Cs
  name = G4_Cs
  specific = 4
FEATURE [App::DocumentObjectGroupPython] Ba_element003  label="Ba_element : 003"  # scripted group (container) (typed FeaturePython)
  n = 1
  ref = Ba_element
FEATURE [App::DocumentObjectGroupPython] G4_Ba  # scripted group (container) (typed FeaturePython)
  Dunit = g/cm3
  Dvalue = 3.5
  Group = -> [Ba_element003]
  conduct = 2
  density = 1
  expand = 3
  formula = Ba
  name = G4_Ba
  specific = 4
FEATURE [App::DocumentObjectGroupPython] La_element003  label="La_element : 003"  # scripted group (container) (typed FeaturePython)
  n = 1
  ref = La_element
FEATURE [App::DocumentObjectGroupPython] G4_La  # scripted group (container) (typed FeaturePython)
  Dunit = g/cm3
  Dvalue = 6.154
  Group = -> [La_element003]
  conduct = 2
  density = 1
  expand = 3
  formula = La
  name = G4_La
  specific = 4
FEATURE [App::DocumentObjectGroupPython] Ce_element002  label="Ce_element : 1"  # scripted group (container) (typed FeaturePython)
  n = 1
  ref = Ce_element
FEATURE [App::DocumentObjectGroupPython] G4_Ce  # scripted group (container) (typed FeaturePython)
  Dunit = g/cm3
  Dvalue = 6.657
  Group = -> [Ce_element002]
  conduct = 2
  density = 1
  expand = 3
  formula = Ce
  name = G4_Ce
  specific = 4
FEATURE [App::DocumentObjectGroupPython] Pr_element001  label="Pr_element : 1"  # scripted group (container) (typed FeaturePython)
  n = 1
  ref = Pr_element
FEATURE [App::DocumentObjectGroupPython] G4_Pr  # scripted group (container) (typed FeaturePython)
  Dunit = g/cm3
  Dvalue = 6.71
  Group = -> [Pr_element001]
  conduct = 2
  density = 1
  expand = 3
  formula = Pr
  name = G4_Pr
  specific = 4
FEATURE [App::DocumentObjectGroupPython] Nd_element001  label="Nd_element : 1"  # scripted group (container) (typed FeaturePython)
  n = 1
  ref = Nd_element
FEATURE [App::DocumentObjectGroupPython] G4_Nd  # scripted group (container) (typed FeaturePython)
  Dunit = g/cm3
  Dvalue = 6.9
  Group = -> [Nd_element001]
  conduct = 2
  density = 1
  expand = 3
  formula = Nd
  name = G4_Nd
  specific = 4
FEATURE [App::DocumentObjectGroupPython] Pm_element001  label="Pm_element : 1"  # scripted group (container) (typed FeaturePython)
  n = 1
  ref = Pm_element
FEATURE [App::DocumentObjectGroupPython] G4_Pm  # scripted group (container) (typed FeaturePython)
  Dunit = g/cm3
  Dvalue = 7.22
  Group = -> [Pm_element001]
  conduct = 2
  density = 1
  expand = 3
  formula = Pm
  name = G4_Pm
  specific = 4
FEATURE [App::DocumentObjectGroupPython] Sm_element001  label="Sm_element : 1"  # scripted group (container) (typed FeaturePython)
  n = 1
  ref = Sm_element
FEATURE [App::DocumentObjectGroupPython] G4_Sm  # scripted group (container) (typed FeaturePython)
  Dunit = g/cm3
  Dvalue = 7.46
  Group = -> [Sm_element001]
  conduct = 2
  density = 1
  expand = 3
  formula = Sm
  name = G4_Sm
  specific = 4
FEATURE [App::DocumentObjectGroupPython] Eu_element001  label="Eu_element : 1"  # scripted group (container) (typed FeaturePython)
  n = 1
  ref = Eu_element
FEATURE [App::DocumentObjectGroupPython] G4_Eu  # scripted group (container) (typed FeaturePython)
  Dunit = g/cm3
  Dvalue = 5.243
  Group = -> [Eu_element001]
  conduct = 2
  density = 1
  expand = 3
  formula = Eu
  name = G4_Eu
  specific = 4
FEATURE [App::DocumentObjectGroupPython] Gd_element002  label="Gd_element : 1"  # scripted group (container) (typed FeaturePython)
  n = 1
  ref = Gd_element
FEATURE [App::DocumentObjectGroupPython] G4_Gd  # scripted group (container) (typed FeaturePython)
  Dunit = g/cm3
  Dvalue = 7.9004
  Group = -> [Gd_element002]
  conduct = 2
  density = 1
  expand = 3
  formula = Gd
  name = G4_Gd
  specific = 4
FEATURE [App::DocumentObjectGroupPython] Tb_element001  label="Tb_element : 1"  # scripted group (container) (typed FeaturePython)
  n = 1
  ref = Tb_element
FEATURE [App::DocumentObjectGroupPython] G4_Tb  # scripted group (container) (typed FeaturePython)
  Dunit = g/cm3
  Dvalue = 8.229
  Group = -> [Tb_element001]
  conduct = 2
  density = 1
  expand = 3
  formula = Tb
  name = G4_Tb
  specific = 4
FEATURE [App::DocumentObjectGroupPython] Dy_element001  label="Dy_element : 1"  # scripted group (container) (typed FeaturePython)
  n = 1
  ref = Dy_element
FEATURE [App::DocumentObjectGroupPython] G4_Dy  # scripted group (container) (typed FeaturePython)
  Dunit = g/cm3
  Dvalue = 8.55
  Group = -> [Dy_element001]
  conduct = 2
  density = 1
  expand = 3
  formula = Dy
  name = G4_Dy
  specific = 4
FEATURE [App::DocumentObjectGroupPython] Ho_element001  label="Ho_element : 1"  # scripted group (container) (typed FeaturePython)
  n = 1
  ref = Ho_element
FEATURE [App::DocumentObjectGroupPython] G4_Ho  # scripted group (container) (typed FeaturePython)
  Dunit = g/cm3
  Dvalue = 8.795
  Group = -> [Ho_element001]
  conduct = 2
  density = 1
  expand = 3
  formula = Ho
  name = G4_Ho
  specific = 4
FEATURE [App::DocumentObjectGroupPython] Er_element001  label="Er_element : 1"  # scripted group (container) (typed FeaturePython)
  n = 1
  ref = Er_element
FEATURE [App::DocumentObjectGroupPython] G4_Er  # scripted group (container) (typed FeaturePython)
  Dunit = g/cm3
  Dvalue = 9.066
  Group = -> [Er_element001]
  conduct = 2
  density = 1
  expand = 3
  formula = Er
  name = G4_Er
  specific = 4
FEATURE [App::DocumentObjectGroupPython] Tm_element001  label="Tm_element : 1"  # scripted group (container) (typed FeaturePython)
  n = 1
  ref = Tm_element
FEATURE [App::DocumentObjectGroupPython] G4_Tm  # scripted group (container) (typed FeaturePython)
  Dunit = g/cm3
  Dvalue = 9.321
  Group = -> [Tm_element001]
  conduct = 2
  density = 1
  expand = 3
  formula = Tm
  name = G4_Tm
  specific = 4
FEATURE [App::DocumentObjectGroupPython] Yb_element001  label="Yb_element : 1"  # scripted group (container) (typed FeaturePython)
  n = 1
  ref = Yb_element
FEATURE [App::DocumentObjectGroupPython] G4_Yb  # scripted group (container) (typed FeaturePython)
  Dunit = g/cm3
  Dvalue = 6.73
  Group = -> [Yb_element001]
  conduct = 2
  density = 1
  expand = 3
  formula = Yb
  name = G4_Yb
  specific = 4
FEATURE [App::DocumentObjectGroupPython] Lu_element001  label="Lu_element : 1"  # scripted group (container) (typed FeaturePython)
  n = 1
  ref = Lu_element
FEATURE [App::DocumentObjectGroupPython] G4_Lu  # scripted group (container) (typed FeaturePython)
  Dunit = g/cm3
  Dvalue = 9.84
  Group = -> [Lu_element001]
  conduct = 2
  density = 1
  expand = 3
  formula = Lu
  name = G4_Lu
  specific = 4
FEATURE [App::DocumentObjectGroupPython] Hf_element001  label="Hf_element : 1"  # scripted group (container) (typed FeaturePython)
  n = 1
  ref = Hf_element
FEATURE [App::DocumentObjectGroupPython] G4_Hf  # scripted group (container) (typed FeaturePython)
  Dunit = g/cm3
  Dvalue = 13.31
  Group = -> [Hf_element001]
  conduct = 2
  density = 1
  expand = 3
  formula = Hf
  name = G4_Hf
  specific = 4
FEATURE [App::DocumentObjectGroupPython] Ta_element001  label="Ta_element : 1"  # scripted group (container) (typed FeaturePython)
  n = 1
  ref = Ta_element
FEATURE [App::DocumentObjectGroupPython] G4_Ta  # scripted group (container) (typed FeaturePython)
  Dunit = g/cm3
  Dvalue = 16.654
  Group = -> [Ta_element001]
  conduct = 2
  density = 1
  expand = 3
  formula = Ta
  name = G4_Ta
  specific = 4
FEATURE [App::DocumentObjectGroupPython] W_element004  label="W_element : 004"  # scripted group (container) (typed FeaturePython)
  n = 1
  ref = W_element
FEATURE [App::DocumentObjectGroupPython] G4_W  # scripted group (container) (typed FeaturePython)
  Dunit = g/cm3
  Dvalue = 19.3
  Group = -> [W_element004]
  conduct = 2
  density = 1
  expand = 3
  formula = W
  name = G4_W
  specific = 4
FEATURE [App::DocumentObjectGroupPython] Re_element001  label="Re_element : 1"  # scripted group (container) (typed FeaturePython)
  n = 1
  ref = Re_element
FEATURE [App::DocumentObjectGroupPython] G4_Re  # scripted group (container) (typed FeaturePython)
  Dunit = g/cm3
  Dvalue = 21.02
  Group = -> [Re_element001]
  conduct = 2
  density = 1
  expand = 3
  formula = Re
  name = G4_Re
  specific = 4
FEATURE [App::DocumentObjectGroupPython] Os_element001  label="Os_element : 1"  # scripted group (container) (typed FeaturePython)
  n = 1
  ref = Os_element
FEATURE [App::DocumentObjectGroupPython] G4_Os  # scripted group (container) (typed FeaturePython)
  Dunit = g/cm3
  Dvalue = 22.57
  Group = -> [Os_element001]
  conduct = 2
  density = 1
  expand = 3
  formula = Os
  name = G4_Os
  specific = 4
FEATURE [App::DocumentObjectGroupPython] Ir_element001  label="Ir_element : 1"  # scripted group (container) (typed FeaturePython)
  n = 1
  ref = Ir_element
FEATURE [App::DocumentObjectGroupPython] G4_Ir  # scripted group (container) (typed FeaturePython)
  Dunit = g/cm3
  Dvalue = 22.42
  Group = -> [Ir_element001]
  conduct = 2
  density = 1
  expand = 3
  formula = Ir
  name = G4_Ir
  specific = 4
FEATURE [App::DocumentObjectGroupPython] Pt_element001  label="Pt_element : 1"  # scripted group (container) (typed FeaturePython)
  n = 1
  ref = Pt_element
FEATURE [App::DocumentObjectGroupPython] G4_Pt  # scripted group (container) (typed FeaturePython)
  Dunit = g/cm3
  Dvalue = 21.45
  Group = -> [Pt_element001]
  conduct = 2
  density = 1
  expand = 3
  formula = Pt
  name = G4_Pt
  specific = 4
FEATURE [App::DocumentObjectGroupPython] Au_element001  label="Au_element : 1"  # scripted group (container) (typed FeaturePython)
  n = 1
  ref = Au_element
FEATURE [App::DocumentObjectGroupPython] G4_Au  # scripted group (container) (typed FeaturePython)
  Dunit = g/cm3
  Dvalue = 19.32
  Group = -> [Au_element001]
  conduct = 2
  density = 1
  expand = 3
  formula = Au
  name = G4_Au
  specific = 4
FEATURE [App::DocumentObjectGroupPython] Hg_element002  label="Hg_element : 002"  # scripted group (container) (typed FeaturePython)
  n = 1
  ref = Hg_element
FEATURE [App::DocumentObjectGroupPython] G4_Hg  # scripted group (container) (typed FeaturePython)
  Dunit = g/cm3
  Dvalue = 13.546
  Group = -> [Hg_element002]
  conduct = 2
  density = 1
  expand = 3
  formula = Hg
  name = G4_Hg
  specific = 4
FEATURE [App::DocumentObjectGroupPython] Tl_element002  label="Tl_element : 002"  # scripted group (container) (typed FeaturePython)
  n = 1
  ref = Tl_element
FEATURE [App::DocumentObjectGroupPython] G4_Tl  # scripted group (container) (typed FeaturePython)
  Dunit = g/cm3
  Dvalue = 11.72
  Group = -> [Tl_element002]
  conduct = 2
  density = 1
  expand = 3
  formula = Tl
  name = G4_Tl
  specific = 4
FEATURE [App::DocumentObjectGroupPython] Pb_element003  label="Pb_element : 1"  # scripted group (container) (typed FeaturePython)
  n = 1
  ref = Pb_element
FEATURE [App::DocumentObjectGroupPython] G4_Pb  # scripted group (container) (typed FeaturePython)
  Dunit = g/cm3
  Dvalue = 11.35
  Group = -> [Pb_element003]
  conduct = 2
  density = 1
  expand = 3
  formula = Pb
  name = G4_Pb
  specific = 4
FEATURE [App::DocumentObjectGroupPython] Bi_element002  label="Bi_element : 1"  # scripted group (container) (typed FeaturePython)
  n = 1
  ref = Bi_element
FEATURE [App::DocumentObjectGroupPython] G4_Bi  # scripted group (container) (typed FeaturePython)
  Dunit = g/cm3
  Dvalue = 9.747
  Group = -> [Bi_element002]
  conduct = 2
  density = 1
  expand = 3
  formula = Bi
  name = G4_Bi
  specific = 4
FEATURE [App::DocumentObjectGroupPython] Po_element001  label="Po_element : 1"  # scripted group (container) (typed FeaturePython)
  n = 1
  ref = Po_element
FEATURE [App::DocumentObjectGroupPython] G4_Po  # scripted group (container) (typed FeaturePython)
  Dunit = g/cm3
  Dvalue = 9.32
  Group = -> [Po_element001]
  conduct = 2
  density = 1
  expand = 3
  formula = Po
  name = G4_Po
  specific = 4
FEATURE [App::DocumentObjectGroupPython] At_element001  label="At_element : 1"  # scripted group (container) (typed FeaturePython)
  n = 1
  ref = At_element
FEATURE [App::DocumentObjectGroupPython] G4_At  # scripted group (container) (typed FeaturePython)
  Dunit = g/cm3
  Dvalue = 9.32
  Group = -> [At_element001]
  conduct = 2
  density = 1
  expand = 3
  formula = At
  name = G4_At
  specific = 4
FEATURE [App::DocumentObjectGroupPython] Rn_element001  label="Rn_element : 1"  # scripted group (container) (typed FeaturePython)
  n = 1
  ref = Rn_element
FEATURE [App::DocumentObjectGroupPython] G4_Rn  # scripted group (container) (typed FeaturePython)
  Dunit = g/cm3
  Dvalue = 0.00900662
  Group = -> [Rn_element001]
  conduct = 2
  density = 1
  expand = 3
  formula = Rn
  name = G4_Rn
  specific = 4
FEATURE [App::DocumentObjectGroupPython] Fr_element001  label="Fr_element : 1"  # scripted group (container) (typed FeaturePython)
  n = 1
  ref = Fr_element
FEATURE [App::DocumentObjectGroupPython] G4_Fr  # scripted group (container) (typed FeaturePython)
  Dunit = g/cm3
  Dvalue = 1
  Group = -> [Fr_element001]
  conduct = 2
  density = 1
  expand = 3
  formula = Fr
  name = G4_Fr
  specific = 4
FEATURE [App::DocumentObjectGroupPython] Ra_element001  label="Ra_element : 1"  # scripted group (container) (typed FeaturePython)
  n = 1
  ref = Ra_element
FEATURE [App::DocumentObjectGroupPython] G4_Ra  # scripted group (container) (typed FeaturePython)
  Dunit = g/cm3
  Dvalue = 5
  Group = -> [Ra_element001]
  conduct = 2
  density = 1
  expand = 3
  formula = Ra
  name = G4_Ra
  specific = 4
FEATURE [App::DocumentObjectGroupPython] Ac_element001  label="Ac_element : 1"  # scripted group (container) (typed FeaturePython)
  n = 1
  ref = Ac_element
FEATURE [App::DocumentObjectGroupPython] G4_Ac  # scripted group (container) (typed FeaturePython)
  Dunit = g/cm3
  Dvalue = 10.07
  Group = -> [Ac_element001]
  conduct = 2
  density = 1
  expand = 3
  formula = Ac
  name = G4_Ac
  specific = 4
FEATURE [App::DocumentObjectGroupPython] Th_element001  label="Th_element : 1"  # scripted group (container) (typed FeaturePython)
  n = 1
  ref = Th_element
FEATURE [App::DocumentObjectGroupPython] G4_Th  # scripted group (container) (typed FeaturePython)
  Dunit = g/cm3
  Dvalue = 11.72
  Group = -> [Th_element001]
  conduct = 2
  density = 1
  expand = 3
  formula = Th
  name = G4_Th
  specific = 4
FEATURE [App::DocumentObjectGroupPython] Pa_element001  label="Pa_element : 1"  # scripted group (container) (typed FeaturePython)
  n = 1
  ref = Pa_element
FEATURE [App::DocumentObjectGroupPython] G4_Pa  # scripted group (container) (typed FeaturePython)
  Dunit = g/cm3
  Dvalue = 15.37
  Group = -> [Pa_element001]
  conduct = 2
  density = 1
  expand = 3
  formula = Pa
  name = G4_Pa
  specific = 4
FEATURE [App::DocumentObjectGroupPython] U_element004  label="U_element : 004"  # scripted group (container) (typed FeaturePython)
  n = 1
  ref = U_element
FEATURE [App::DocumentObjectGroupPython] G4_U  # scripted group (container) (typed FeaturePython)
  Dunit = g/cm3
  Dvalue = 18.95
  Group = -> [U_element004]
  conduct = 2
  density = 1
  expand = 3
  formula = U
  name = G4_U
  specific = 4
FEATURE [App::DocumentObjectGroupPython] Np_element001  label="Np_element : 1"  # scripted group (container) (typed FeaturePython)
  n = 1
  ref = Np_element
FEATURE [App::DocumentObjectGroupPython] G4_Np  # scripted group (container) (typed FeaturePython)
  Dunit = g/cm3
  Dvalue = 20.25
  Group = -> [Np_element001]
  conduct = 2
  density = 1
  expand = 3
  formula = Np
  name = G4_Np
  specific = 4
FEATURE [App::DocumentObjectGroupPython] Pu_element002  label="Pu_element : 002"  # scripted group (container) (typed FeaturePython)
  n = 1
  ref = Pu_element
FEATURE [App::DocumentObjectGroupPython] G4_Pu  # scripted group (container) (typed FeaturePython)
  Dunit = g/cm3
  Dvalue = 19.84
  Group = -> [Pu_element002]
  conduct = 2
  density = 1
  expand = 3
  formula = Pu
  name = G4_Pu
  specific = 4
FEATURE [App::DocumentObjectGroupPython] Am_element001  label="Am_element : 1"  # scripted group (container) (typed FeaturePython)
  n = 1
  ref = Am_element
FEATURE [App::DocumentObjectGroupPython] G4_Am  # scripted group (container) (typed FeaturePython)
  Dunit = g/cm3
  Dvalue = 13.67
  Group = -> [Am_element001]
  conduct = 2
  density = 1
  expand = 3
  formula = Am
  name = G4_Am
  specific = 4
FEATURE [App::DocumentObjectGroupPython] Cm_element001  label="Cm_element : 1"  # scripted group (container) (typed FeaturePython)
  n = 1
  ref = Cm_element
FEATURE [App::DocumentObjectGroupPython] G4_Cm  # scripted group (container) (typed FeaturePython)
  Dunit = g/cm3
  Dvalue = 13.51
  Group = -> [Cm_element001]
  conduct = 2
  density = 1
  expand = 3
  formula = Cm
  name = G4_Cm
  specific = 4
FEATURE [App::DocumentObjectGroupPython] Bk_element001  label="Bk_element : 1"  # scripted group (container) (typed FeaturePython)
  n = 1
  ref = Bk_element
FEATURE [App::DocumentObjectGroupPython] G4_Bk  # scripted group (container) (typed FeaturePython)
  Dunit = g/cm3
  Dvalue = 14
  Group = -> [Bk_element001]
  conduct = 2
  density = 1
  expand = 3
  formula = Bk
  name = G4_Bk
  specific = 4
FEATURE [App::DocumentObjectGroupPython] Cf_element001  label="Cf_element : 1"  # scripted group (container) (typed FeaturePython)
  n = 1
  ref = Cf_element
FEATURE [App::DocumentObjectGroupPython] G4_Cf  # scripted group (container) (typed FeaturePython)
  Dunit = g/cm3
  Dvalue = 10
  Group = -> [Cf_element001]
  conduct = 2
  density = 1
  expand = 3
  formula = Cf
  name = G4_Cf
  specific = 4
FEATURE [App::DocumentObjectGroupPython] Element  # scripted group (container) (typed FeaturePython)
  Group = -> [G4_H,G4_He,G4_Li,G4_Be,G4_B,G4_C,G4_N,G4_O,G4_F,G4_Ne,G4_Na,G4_Mg,G4_Al,G4_Si,G4_P,G4_S,G4_Cl,G4_Ar,G4_K,G4_Ca,G4_Sc,G4_Ti,G4_V,G4_Cr,G4_Mn,G4_Fe,G4_Co,G4_Ni,G4_Cu,G4_Zn,G4_Ga,G4_Ge,G4_As,G4_Se,G4_Br,G4_Kr,G4_Rb,G4_Sr,G4_Y,G4_Zr,G4_Nb,G4_Mo,G4_Tc,G4_Ru,G4_Rh,G4_Pd,G4_Ag,G4_Cd,G4_In,G4_Sn,G4_Sb,G4_Te,G4_I,G4_Xe,G4_Cs,G4_Ba,G4_La,G4_Ce,G4_Pr,G4_Nd,G4_Pm,G4_Sm,G4_Eu,G4_Gd,G4_Tb,G4_Dy,G4_Ho,G4_Er,+30 more]
FEATURE [App::DocumentObjectGroupPython] H_element114  label="H_element : 063"  # scripted group (container) (typed FeaturePython)
  n = 2
  ref = H_element
FEATURE [App::DocumentObjectGroupPython] G4_lH2  # scripted group (container) (typed FeaturePython)
  Dunit = g/cm3
  Dvalue = 0.0708
  Group = -> [H_element114]
  conduct = 2
  density = 1
  expand = 3
  formula = G4_lH2
  name = G4_lH2
  specific = 4
FEATURE [App::DocumentObjectGroupPython] N_element049  label="N_element : 022"  # scripted group (container) (typed FeaturePython)
  n = 2
  ref = N_element
FEATURE [App::DocumentObjectGroupPython] G4_lN2  # scripted group (container) (typed FeaturePython)
  Dunit = g/cm3
  Dvalue = 0.807
  Group = -> [N_element049]
  conduct = 2
  density = 1
  expand = 3
  formula = G4_lN2
  name = G4_lN2
  specific = 4
FEATURE [App::DocumentObjectGroupPython] O_element106  label="O_element : 060"  # scripted group (container) (typed FeaturePython)
  n = 2
  ref = O_element
FEATURE [App::DocumentObjectGroupPython] G4_lO2  # scripted group (container) (typed FeaturePython)
  Dunit = g/cm3
  Dvalue = 1.141
  Group = -> [O_element106]
  conduct = 2
  density = 1
  expand = 3
  formula = G4_lO2
  name = G4_lO2
  specific = 4
FEATURE [App::DocumentObjectGroupPython] Ar  label="Ar : 1"  # scripted group (container) (typed FeaturePython)
  n = 1
  ref = Ar
FEATURE [App::DocumentObjectGroupPython] G4_lAr  # scripted group (container) (typed FeaturePython)
  Dunit = g/cm3
  Dvalue = 1.396
  Group = -> [Ar]
  conduct = 2
  density = 1
  expand = 3
  formula = G4_lAr
  name = G4_lAr
  specific = 4
FEATURE [App::DocumentObjectGroupPython] Br  label="Br : 1"  # scripted group (container) (typed FeaturePython)
  n = 1
  ref = Br
FEATURE [App::DocumentObjectGroupPython] G4_lBr  # scripted group (container) (typed FeaturePython)
  Dunit = g/cm3
  Dvalue = 3.1028
  Group = -> [Br]
  conduct = 2
  density = 1
  expand = 3
  formula = G4_lBr
  name = G4_lBr
  specific = 4
FEATURE [App::DocumentObjectGroupPython] Kr  label="Kr : 1"  # scripted group (container) (typed FeaturePython)
  n = 1
  ref = Kr
FEATURE [App::DocumentObjectGroupPython] G4_lKr  # scripted group (container) (typed FeaturePython)
  Dunit = g/cm3
  Dvalue = 2.418
  Group = -> [Kr]
  conduct = 2
  density = 1
  expand = 3
  formula = G4_lKr
  name = G4_lKr
  specific = 4
FEATURE [App::DocumentObjectGroupPython] Xe  label="Xe : 1"  # scripted group (container) (typed FeaturePython)
  n = 1
  ref = Xe
FEATURE [App::DocumentObjectGroupPython] G4_lXe  # scripted group (container) (typed FeaturePython)
  Dunit = g/cm3
  Dvalue = 2.953
  Group = -> [Xe]
  conduct = 2
  density = 1
  expand = 3
  formula = G4_lXe
  name = G4_lXe
  specific = 4
FEATURE [App::DocumentObjectGroupPython] O_element107  label="O_element : 061"  # scripted group (container) (typed FeaturePython)
  n = 4
  ref = O_element
FEATURE [App::DocumentObjectGroupPython] Pb_element004  label="Pb_element : 002"  # scripted group (container) (typed FeaturePython)
  n = 1
  ref = Pb_element
FEATURE [App::DocumentObjectGroupPython] W_element005  label="W_element : 005"  # scripted group (container) (typed FeaturePython)
  n = 1
  ref = W_element
FEATURE [App::DocumentObjectGroupPython] G4_PbWO4  # scripted group (container) (typed FeaturePython)
  Dunit = g/cm3
  Dvalue = 8.28
  Group = -> [O_element107,Pb_element004,W_element005]
  conduct = 2
  density = 1
  expand = 3
  formula = G4_PbWO4
  name = G4_PbWO4
  specific = 4
FEATURE [App::DocumentObjectGroupPython] alactic  label="alactic : 1"  # scripted group (container) (typed FeaturePython)
  n = 1
  ref = alactic
FEATURE [App::DocumentObjectGroupPython] G4_Galactic  # scripted group (container) (typed FeaturePython)
  Dunit = g/cm3
  Dvalue = 0
  Group = -> [alactic]
  conduct = 2
  density = 1
  expand = 3
  formula = G4_Galactic
  name = G4_Galactic
  specific = 4
FEATURE [App::DocumentObjectGroupPython] RAPHITE_POROUS  label="RAPHITE_POROUS : 1"  # scripted group (container) (typed FeaturePython)
  n = 1
  ref = RAPHITE_POROUS
FEATURE [App::DocumentObjectGroupPython] G4_GRAPHITE_POROUS  # scripted group (container) (typed FeaturePython)
  Dunit = g/cm3
  Dvalue = 1.7
  Group = -> [RAPHITE_POROUS]
  conduct = 2
  density = 1
  expand = 3
  formula = G4_GRAPHITE_POROUS
  name = G4_GRAPHITE_POROUS
  specific = 4
FEATURE [App::DocumentObjectGroupPython] H_element115  label="H_element : 0.150"  # scripted group (container) (typed FeaturePython)
  n = 0.080538
FEATURE [App::DocumentObjectGroupPython] C_element125  label="C_element : 0.600"  # scripted group (container) (typed FeaturePython)
  n = 0.599848
FEATURE [App::DocumentObjectGroupPython] O_element108  label="O_element : 0.320"  # scripted group (container) (typed FeaturePython)
  n = 0.319614
FEATURE [App::DocumentObjectGroupPython] G4_LUCITE  # scripted group (container) (typed FeaturePython)
  Dunit = g/cm3
  Dvalue = 1.19
  Group = -> [H_element115,C_element125,O_element108]
  conduct = 2
  density = 1
  expand = 3
  formula = G4_LUCITE
  name = G4_LUCITE
  specific = 4
FEATURE [App::DocumentObjectGroupPython] Cu_element002  label="Cu_element : 62"  # scripted group (container) (typed FeaturePython)
  n = 62
  ref = Cu_element
FEATURE [App::DocumentObjectGroupPython] Zn_element002  label="Zn_element : 35"  # scripted group (container) (typed FeaturePython)
  n = 35
  ref = Zn_element
FEATURE [App::DocumentObjectGroupPython] Pb_element005  label="Pb_element : 3"  # scripted group (container) (typed FeaturePython)
  n = 3
  ref = Pb_element
FEATURE [App::DocumentObjectGroupPython] G4_BRASS  # scripted group (container) (typed FeaturePython)
  Dunit = g/cm3
  Dvalue = 8.52
  Group = -> [Cu_element002,Zn_element002,Pb_element005]
  conduct = 2
  density = 1
  expand = 3
  formula = G4_BRASS
  name = G4_BRASS
  specific = 4
FEATURE [App::DocumentObjectGroupPython] Cu_element003  label="Cu_element : 89"  # scripted group (container) (typed FeaturePython)
  n = 89
  ref = Cu_element
FEATURE [App::DocumentObjectGroupPython] Zn_element003  label="Zn_element : 9"  # scripted group (container) (typed FeaturePython)
  n = 9
  ref = Zn_element
FEATURE [App::DocumentObjectGroupPython] Pb_element006  label="Pb_element : 2"  # scripted group (container) (typed FeaturePython)
  n = 2
  ref = Pb_element
FEATURE [App::DocumentObjectGroupPython] G4_BRONZE  # scripted group (container) (typed FeaturePython)
  Dunit = g/cm3
  Dvalue = 8.82
  Group = -> [Cu_element003,Zn_element003,Pb_element006]
  conduct = 2
  density = 1
  expand = 3
  formula = G4_BRONZE
  name = G4_BRONZE
  specific = 4
FEATURE [App::DocumentObjectGroupPython] Fe_element008  label="Fe_element : 74"  # scripted group (container) (typed FeaturePython)
  n = 74
  ref = Fe_element
FEATURE [App::DocumentObjectGroupPython] Cr_element002  label="Cr_element : 18"  # scripted group (container) (typed FeaturePython)
  n = 18
  ref = Cr_element
FEATURE [App::DocumentObjectGroupPython] Ni_element002  label="Ni_element : 8"  # scripted group (container) (typed FeaturePython)
  n = 8
  ref = Ni_element
FEATURE [App::DocumentObjectGroupPython] G4_STAINLESS_STEEL  label="G4_STAINLESS-STEEL"  # scripted group (container) (typed FeaturePython)
  Dunit = g/cm3
  Dvalue = 8
  Group = -> [Fe_element008,Cr_element002,Ni_element002]
  conduct = 2
  density = 1
  expand = 3
  formula = G4_STAINLESS-STEEL
  name = G4_STAINLESS-STEEL
  specific = 4
FEATURE [App::DocumentObjectGroupPython] H_element116  label="H_element : 064"  # scripted group (container) (typed FeaturePython)
  n = 18
  ref = H_element
FEATURE [App::DocumentObjectGroupPython] C_element126  label="C_element : 071"  # scripted group (container) (typed FeaturePython)
  n = 12
  ref = C_element
FEATURE [App::DocumentObjectGroupPython] O_element109  label="O_element : 062"  # scripted group (container) (typed FeaturePython)
  n = 7
  ref = O_element
FEATURE [App::DocumentObjectGroupPython] G4_CR39  # scripted group (container) (typed FeaturePython)
  Dunit = g/cm3
  Dvalue = 1.32
  Group = -> [H_element116,C_element126,O_element109]
  conduct = 2
  density = 1
  expand = 3
  formula = G4_CR39
  name = G4_CR39
  specific = 4
FEATURE [App::DocumentObjectGroupPython] H_element117  label="H_element : 38"  # scripted group (container) (typed FeaturePython)
  n = 38
  ref = H_element
FEATURE [App::DocumentObjectGroupPython] C_element127  label="C_element : 072"  # scripted group (container) (typed FeaturePython)
  n = 18
  ref = C_element
FEATURE [App::DocumentObjectGroupPython] O_element110  label="O_element : 063"  # scripted group (container) (typed FeaturePython)
  n = 1
  ref = O_element
FEATURE [App::DocumentObjectGroupPython] G4_OCTADECANOL  # scripted group (container) (typed FeaturePython)
  Dunit = g/cm3
  Dvalue = 0.812
  Group = -> [H_element117,C_element127,O_element110]
  conduct = 2
  density = 1
  expand = 3
  formula = G4_OCTADECANOL
  name = G4_OCTADECANOL
  specific = 4
FEATURE [App::DocumentObjectGroupPython] HEP  # scripted group (container) (typed FeaturePython)
  Group = -> [G4_lH2,G4_lN2,G4_lO2,G4_lAr,G4_lBr,G4_lKr,G4_lXe,G4_PbWO4,G4_Galactic,G4_GRAPHITE_POROUS,G4_LUCITE,G4_BRASS,G4_BRONZE,G4_STAINLESS_STEEL,G4_CR39,G4_OCTADECANOL]
FEATURE [App::DocumentObjectGroupPython] C_element128  label="C_element : 073"  # scripted group (container) (typed FeaturePython)
  n = 14
  ref = C_element
FEATURE [App::DocumentObjectGroupPython] H_element118  label="H_element : 065"  # scripted group (container) (typed FeaturePython)
  n = 10
  ref = H_element
FEATURE [App::DocumentObjectGroupPython] O_element111  label="O_element : 064"  # scripted group (container) (typed FeaturePython)
  n = 2
  ref = O_element
FEATURE [App::DocumentObjectGroupPython] N_element050  label="N_element : 023"  # scripted group (container) (typed FeaturePython)
  n = 2
  ref = N_element
FEATURE [App::DocumentObjectGroupPython] G4_KEVLAR  # scripted group (container) (typed FeaturePython)
  Dunit = g/cm3
  Dvalue = 1.44
  Group = -> [C_element128,H_element118,O_element111,N_element050]
  conduct = 2
  density = 1
  expand = 3
  formula = G4_KEVLAR
  name = G4_KEVLAR
  specific = 4
FEATURE [App::DocumentObjectGroupPython] C_element129  label="C_element : 074"  # scripted group (container) (typed FeaturePython)
  n = 10
  ref = C_element
FEATURE [App::DocumentObjectGroupPython] H_element119  label="H_element : 066"  # scripted group (container) (typed FeaturePython)
  n = 8
  ref = H_element
FEATURE [App::DocumentObjectGroupPython] O_element112  label="O_element : 065"  # scripted group (container) (typed FeaturePython)
  n = 4
  ref = O_element
FEATURE [App::DocumentObjectGroupPython] G4_DACRON  # scripted group (container) (typed FeaturePython)
  Dunit = g/cm3
  Dvalue = 1.4
  Group = -> [C_element129,H_element119,O_element112]
  conduct = 2
  density = 1
  expand = 3
  formula = G4_DACRON
  name = G4_DACRON
  specific = 4
FEATURE [App::DocumentObjectGroupPython] C_element130  label="C_element : 075"  # scripted group (container) (typed FeaturePython)
  n = 4
  ref = C_element
FEATURE [App::DocumentObjectGroupPython] H_element120  label="H_element : 067"  # scripted group (container) (typed FeaturePython)
  n = 5
  ref = H_element
FEATURE [App::DocumentObjectGroupPython] Cl_element030  label="Cl_element : 016"  # scripted group (container) (typed FeaturePython)
  n = 1
  ref = Cl_element
FEATURE [App::DocumentObjectGroupPython] G4_NEOPRENE  # scripted group (container) (typed FeaturePython)
  Dunit = g/cm3
  Dvalue = 1.23
  Group = -> [C_element130,H_element120,Cl_element030]
  conduct = 2
  density = 1
  expand = 3
  formula = G4_NEOPRENE
  name = G4_NEOPRENE
  specific = 4
FEATURE [App::DocumentObjectGroupPython] Space  # scripted group (container) (typed FeaturePython)
  Group = -> [G4_KEVLAR,G4_DACRON,G4_NEOPRENE]
FEATURE [App::DocumentObjectGroupPython] H_element121  label="H_element : 068"  # scripted group (container) (typed FeaturePython)
  n = 5
  ref = H_element
FEATURE [App::DocumentObjectGroupPython] C_element131  label="C_element : 076"  # scripted group (container) (typed FeaturePython)
  n = 4
  ref = C_element
FEATURE [App::DocumentObjectGroupPython] N_element051  label="N_element : 3"  # scripted group (container) (typed FeaturePython)
  n = 3
  ref = N_element
FEATURE [App::DocumentObjectGroupPython] O_element113  label="O_element : 066"  # scripted group (container) (typed FeaturePython)
  n = 1
  ref = O_element
FEATURE [App::DocumentObjectGroupPython] G4_CYTOSINE  # scripted group (container) (typed FeaturePython)
  Dunit = g/cm3
  Dvalue = 1.55
  Group = -> [H_element121,C_element131,N_element051,O_element113]
  conduct = 2
  density = 1
  expand = 3
  formula = G4_CYTOSINE
  name = G4_CYTOSINE
  specific = 4
FEATURE [App::DocumentObjectGroupPython] H_element122  label="H_element : 069"  # scripted group (container) (typed FeaturePython)
  n = 6
  ref = H_element
FEATURE [App::DocumentObjectGroupPython] C_element132  label="C_element : 077"  # scripted group (container) (typed FeaturePython)
  n = 5
  ref = C_element
FEATURE [App::DocumentObjectGroupPython] N_element052  label="N_element : 024"  # scripted group (container) (typed FeaturePython)
  n = 2
  ref = N_element
FEATURE [App::DocumentObjectGroupPython] O_element114  label="O_element : 067"  # scripted group (container) (typed FeaturePython)
  n = 2
  ref = O_element
FEATURE [App::DocumentObjectGroupPython] G4_THYMINE  # scripted group (container) (typed FeaturePython)
  Dunit = g/cm3
  Dvalue = 1.23
  Group = -> [H_element122,C_element132,N_element052,O_element114]
  conduct = 2
  density = 1
  expand = 3
  formula = G4_THYMINE
  name = G4_THYMINE
  specific = 4
FEATURE [App::DocumentObjectGroupPython] H_element123  label="H_element : 070"  # scripted group (container) (typed FeaturePython)
  n = 4
  ref = H_element
FEATURE [App::DocumentObjectGroupPython] C_element133  label="C_element : 078"  # scripted group (container) (typed FeaturePython)
  n = 4
  ref = C_element
FEATURE [App::DocumentObjectGroupPython] N_element053  label="N_element : 025"  # scripted group (container) (typed FeaturePython)
  n = 2
  ref = N_element
FEATURE [App::DocumentObjectGroupPython] O_element115  label="O_element : 068"  # scripted group (container) (typed FeaturePython)
  n = 2
  ref = O_element
FEATURE [App::DocumentObjectGroupPython] G4_URACIL  # scripted group (container) (typed FeaturePython)
  Dunit = g/cm3
  Dvalue = 1.32
  Group = -> [H_element123,C_element133,N_element053,O_element115]
  conduct = 2
  density = 1
  expand = 3
  formula = G4_URACIL
  name = G4_URACIL
  specific = 4
FEATURE [App::DocumentObjectGroupPython] H_element124  label="H_element : 071"  # scripted group (container) (typed FeaturePython)
  n = 4
  ref = H_element
FEATURE [App::DocumentObjectGroupPython] C_element134  label="C_element : 079"  # scripted group (container) (typed FeaturePython)
  n = 5
  ref = C_element
FEATURE [App::DocumentObjectGroupPython] N_element054  label="N_element : 026"  # scripted group (container) (typed FeaturePython)
  n = 5
  ref = N_element
FEATURE [App::DocumentObjectGroupPython] G4_DNA_ADENINE  # scripted group (container) (typed FeaturePython)
  Dunit = g/cm3
  Dvalue = 1
  Group = -> [H_element124,C_element134,N_element054]
  conduct = 2
  density = 1
  expand = 3
  formula = G4_DNA_ADENINE
  name = G4_DNA_ADENINE
  specific = 4
FEATURE [App::DocumentObjectGroupPython] H_element125  label="H_element : 072"  # scripted group (container) (typed FeaturePython)
  n = 4
  ref = H_element
FEATURE [App::DocumentObjectGroupPython] C_element135  label="C_element : 080"  # scripted group (container) (typed FeaturePython)
  n = 5
  ref = C_element
FEATURE [App::DocumentObjectGroupPython] N_element055  label="N_element : 027"  # scripted group (container) (typed FeaturePython)
  n = 5
  ref = N_element
FEATURE [App::DocumentObjectGroupPython] O_element116  label="O_element : 069"  # scripted group (container) (typed FeaturePython)
  n = 1
  ref = O_element
FEATURE [App::DocumentObjectGroupPython] G4_DNA_GUANINE  # scripted group (container) (typed FeaturePython)
  Dunit = g/cm3
  Dvalue = 1
  Group = -> [H_element125,C_element135,N_element055,O_element116]
  conduct = 2
  density = 1
  expand = 3
  formula = G4_DNA_GUANINE
  name = G4_DNA_GUANINE
  specific = 4
FEATURE [App::DocumentObjectGroupPython] H_element126  label="H_element : 073"  # scripted group (container) (typed FeaturePython)
  n = 4
  ref = H_element
FEATURE [App::DocumentObjectGroupPython] C_element136  label="C_element : 081"  # scripted group (container) (typed FeaturePython)
  n = 4
  ref = C_element
FEATURE [App::DocumentObjectGroupPython] N_element056  label="N_element : 028"  # scripted group (container) (typed FeaturePython)
  n = 3
  ref = N_element
FEATURE [App::DocumentObjectGroupPython] O_element117  label="O_element : 070"  # scripted group (container) (typed FeaturePython)
  n = 1
  ref = O_element
FEATURE [App::DocumentObjectGroupPython] G4_DNA_CYTOSINE  # scripted group (container) (typed FeaturePython)
  Dunit = g/cm3
  Dvalue = 1
  Group = -> [H_element126,C_element136,N_element056,O_element117]
  conduct = 2
  density = 1
  expand = 3
  formula = G4_DNA_CYTOSINE
  name = G4_DNA_CYTOSINE
  specific = 4
FEATURE [App::DocumentObjectGroupPython] H_element127  label="H_element : 074"  # scripted group (container) (typed FeaturePython)
  n = 5
  ref = H_element
FEATURE [App::DocumentObjectGroupPython] C_element137  label="C_element : 082"  # scripted group (container) (typed FeaturePython)
  n = 5
  ref = C_element
FEATURE [App::DocumentObjectGroupPython] N_element057  label="N_element : 029"  # scripted group (container) (typed FeaturePython)
  n = 2
  ref = N_element
FEATURE [App::DocumentObjectGroupPython] O_element118  label="O_element : 071"  # scripted group (container) (typed FeaturePython)
  n = 2
  ref = O_element
FEATURE [App::DocumentObjectGroupPython] G4_DNA_THYMINE  # scripted group (container) (typed FeaturePython)
  Dunit = g/cm3
  Dvalue = 1
  Group = -> [H_element127,C_element137,N_element057,O_element118]
  conduct = 2
  density = 1
  expand = 3
  formula = G4_DNA_THYMINE
  name = G4_DNA_THYMINE
  specific = 4
FEATURE [App::DocumentObjectGroupPython] H_element128  label="H_element : 075"  # scripted group (container) (typed FeaturePython)
  n = 3
  ref = H_element
FEATURE [App::DocumentObjectGroupPython] C_element138  label="C_element : 083"  # scripted group (container) (typed FeaturePython)
  n = 4
  ref = C_element
FEATURE [App::DocumentObjectGroupPython] N_element058  label="N_element : 030"  # scripted group (container) (typed FeaturePython)
  n = 2
  ref = N_element
FEATURE [App::DocumentObjectGroupPython] O_element119  label="O_element : 072"  # scripted group (container) (typed FeaturePython)
  n = 2
  ref = O_element
FEATURE [App::DocumentObjectGroupPython] G4_DNA_URACIL  # scripted group (container) (typed FeaturePython)
  Dunit = g/cm3
  Dvalue = 1
  Group = -> [H_element128,C_element138,N_element058,O_element119]
  conduct = 2
  density = 1
  expand = 3
  formula = G4_DNA_URACIL
  name = G4_DNA_URACIL
  specific = 4
FEATURE [App::DocumentObjectGroupPython] H_element129  label="H_element : 076"  # scripted group (container) (typed FeaturePython)
  n = 10
  ref = H_element
FEATURE [App::DocumentObjectGroupPython] C_element139  label="C_element : 084"  # scripted group (container) (typed FeaturePython)
  n = 10
  ref = C_element
FEATURE [App::DocumentObjectGroupPython] N_element059  label="N_element : 031"  # scripted group (container) (typed FeaturePython)
  n = 5
  ref = N_element
FEATURE [App::DocumentObjectGroupPython] O_element120  label="O_element : 073"  # scripted group (container) (typed FeaturePython)
  n = 4
  ref = O_element
FEATURE [App::DocumentObjectGroupPython] G4_DNA_ADENOSINE  # scripted group (container) (typed FeaturePython)
  Dunit = g/cm3
  Dvalue = 1
  Group = -> [H_element129,C_element139,N_element059,O_element120]
  conduct = 2
  density = 1
  expand = 3
  formula = G4_DNA_ADENOSINE
  name = G4_DNA_ADENOSINE
  specific = 4
FEATURE [App::DocumentObjectGroupPython] H_element130  label="H_element : 077"  # scripted group (container) (typed FeaturePython)
  n = 10
  ref = H_element
FEATURE [App::DocumentObjectGroupPython] C_element140  label="C_element : 085"  # scripted group (container) (typed FeaturePython)
  n = 10
  ref = C_element
FEATURE [App::DocumentObjectGroupPython] N_element060  label="N_element : 032"  # scripted group (container) (typed FeaturePython)
  n = 5
  ref = N_element
FEATURE [App::DocumentObjectGroupPython] O_element121  label="O_element : 074"  # scripted group (container) (typed FeaturePython)
  n = 5
  ref = O_element
FEATURE [App::DocumentObjectGroupPython] G4_DNA_GUANOSINE  # scripted group (container) (typed FeaturePython)
  Dunit = g/cm3
  Dvalue = 1
  Group = -> [H_element130,C_element140,N_element060,O_element121]
  conduct = 2
  density = 1
  expand = 3
  formula = G4_DNA_GUANOSINE
  name = G4_DNA_GUANOSINE
  specific = 4
FEATURE [App::DocumentObjectGroupPython] H_element131  label="H_element : 078"  # scripted group (container) (typed FeaturePython)
  n = 10
  ref = H_element
FEATURE [App::DocumentObjectGroupPython] C_element141  label="C_element : 086"  # scripted group (container) (typed FeaturePython)
  n = 9
  ref = C_element
FEATURE [App::DocumentObjectGroupPython] N_element061  label="N_element : 033"  # scripted group (container) (typed FeaturePython)
  n = 3
  ref = N_element
FEATURE [App::DocumentObjectGroupPython] O_element122  label="O_element : 075"  # scripted group (container) (typed FeaturePython)
  n = 5
  ref = O_element
FEATURE [App::DocumentObjectGroupPython] G4_DNA_CYTIDINE  # scripted group (container) (typed FeaturePython)
  Dunit = g/cm3
  Dvalue = 1
  Group = -> [H_element131,C_element141,N_element061,O_element122]
  conduct = 2
  density = 1
  expand = 3
  formula = G4_DNA_CYTIDINE
  name = G4_DNA_CYTIDINE
  specific = 4
FEATURE [App::DocumentObjectGroupPython] H_element132  label="H_element : 079"  # scripted group (container) (typed FeaturePython)
  n = 9
  ref = H_element
FEATURE [App::DocumentObjectGroupPython] C_element142  label="C_element : 087"  # scripted group (container) (typed FeaturePython)
  n = 9
  ref = C_element
FEATURE [App::DocumentObjectGroupPython] N_element062  label="N_element : 034"  # scripted group (container) (typed FeaturePython)
  n = 2
  ref = N_element
FEATURE [App::DocumentObjectGroupPython] O_element123  label="O_element : 076"  # scripted group (container) (typed FeaturePython)
  n = 6
  ref = O_element
FEATURE [App::DocumentObjectGroupPython] G4_DNA_URIDINE  # scripted group (container) (typed FeaturePython)
  Dunit = g/cm3
  Dvalue = 1
  Group = -> [H_element132,C_element142,N_element062,O_element123]
  conduct = 2
  density = 1
  expand = 3
  formula = G4_DNA_URIDINE
  name = G4_DNA_URIDINE
  specific = 4
FEATURE [App::DocumentObjectGroupPython] H_element133  label="H_element : 080"  # scripted group (container) (typed FeaturePython)
  n = 11
  ref = H_element
FEATURE [App::DocumentObjectGroupPython] C_element143  label="C_element : 088"  # scripted group (container) (typed FeaturePython)
  n = 10
  ref = C_element
FEATURE [App::DocumentObjectGroupPython] N_element063  label="N_element : 035"  # scripted group (container) (typed FeaturePython)
  n = 2
  ref = N_element
FEATURE [App::DocumentObjectGroupPython] O_element124  label="O_element : 077"  # scripted group (container) (typed FeaturePython)
  n = 6
  ref = O_element
FEATURE [App::DocumentObjectGroupPython] G4_DNA_METHYLURIDINE  # scripted group (container) (typed FeaturePython)
  Dunit = g/cm3
  Dvalue = 1
  Group = -> [H_element133,C_element143,N_element063,O_element124]
  conduct = 2
  density = 1
  expand = 3
  formula = G4_DNA_METHYLURIDINE
  name = G4_DNA_METHYLURIDINE
  specific = 4
FEATURE [App::DocumentObjectGroupPython] P_element014  label="P_element : 003"  # scripted group (container) (typed FeaturePython)
  n = 1
  ref = P_element
FEATURE [App::DocumentObjectGroupPython] O_element125  label="O_element : 078"  # scripted group (container) (typed FeaturePython)
  n = 3
  ref = O_element
FEATURE [App::DocumentObjectGroupPython] G4_DNA_MONOPHOSPHATE  # scripted group (container) (typed FeaturePython)
  Dunit = g/cm3
  Dvalue = 1
  Group = -> [P_element014,O_element125]
  conduct = 2
  density = 1
  expand = 3
  formula = G4_DNA_MONOPHOSPHATE
  name = G4_DNA_MONOPHOSPHATE
  specific = 4
FEATURE [App::DocumentObjectGroupPython] H_element134  label="H_element : 081"  # scripted group (container) (typed FeaturePython)
  n = 10
  ref = H_element
FEATURE [App::DocumentObjectGroupPython] C_element144  label="C_element : 089"  # scripted group (container) (typed FeaturePython)
  n = 10
  ref = C_element
FEATURE [App::DocumentObjectGroupPython] N_element064  label="N_element : 036"  # scripted group (container) (typed FeaturePython)
  n = 5
  ref = N_element
FEATURE [App::DocumentObjectGroupPython] O_element126  label="O_element : 079"  # scripted group (container) (typed FeaturePython)
  n = 7
  ref = O_element
FEATURE [App::DocumentObjectGroupPython] P_element015  label="P_element : 004"  # scripted group (container) (typed FeaturePython)
  n = 1
  ref = P_element
FEATURE [App::DocumentObjectGroupPython] G4_DNA_A  # scripted group (container) (typed FeaturePython)
  Dunit = g/cm3
  Dvalue = 1
  Group = -> [H_element134,C_element144,N_element064,O_element126,P_element015]
  conduct = 2
  density = 1
  expand = 3
  formula = G4_DNA_A
  name = G4_DNA_A
  specific = 4
FEATURE [App::DocumentObjectGroupPython] H_element135  label="H_element : 082"  # scripted group (container) (typed FeaturePython)
  n = 10
  ref = H_element
FEATURE [App::DocumentObjectGroupPython] C_element145  label="C_element : 090"  # scripted group (container) (typed FeaturePython)
  n = 10
  ref = C_element
FEATURE [App::DocumentObjectGroupPython] N_element065  label="N_element : 037"  # scripted group (container) (typed FeaturePython)
  n = 5
  ref = N_element
FEATURE [App::DocumentObjectGroupPython] O_element127  label="O_element : 8"  # scripted group (container) (typed FeaturePython)
  n = 8
  ref = O_element
FEATURE [App::DocumentObjectGroupPython] P_element016  label="P_element : 005"  # scripted group (container) (typed FeaturePython)
  n = 1
  ref = P_element
FEATURE [App::DocumentObjectGroupPython] G4_DNA_G  # scripted group (container) (typed FeaturePython)
  Dunit = g/cm3
  Dvalue = 1
  Group = -> [H_element135,C_element145,N_element065,O_element127,P_element016]
  conduct = 2
  density = 1
  expand = 3
  formula = G4_DNA_G
  name = G4_DNA_G
  specific = 4
FEATURE [App::DocumentObjectGroupPython] H_element136  label="H_element : 083"  # scripted group (container) (typed FeaturePython)
  n = 10
  ref = H_element
FEATURE [App::DocumentObjectGroupPython] C_element146  label="C_element : 091"  # scripted group (container) (typed FeaturePython)
  n = 9
  ref = C_element
FEATURE [App::DocumentObjectGroupPython] N_element066  label="N_element : 038"  # scripted group (container) (typed FeaturePython)
  n = 3
  ref = N_element
FEATURE [App::DocumentObjectGroupPython] O_element128  label="O_element : 080"  # scripted group (container) (typed FeaturePython)
  n = 8
  ref = O_element
FEATURE [App::DocumentObjectGroupPython] P_element017  label="P_element : 006"  # scripted group (container) (typed FeaturePython)
  n = 1
  ref = P_element
FEATURE [App::DocumentObjectGroupPython] G4_DNA_C  # scripted group (container) (typed FeaturePython)
  Dunit = g/cm3
  Dvalue = 1
  Group = -> [H_element136,C_element146,N_element066,O_element128,P_element017]
  conduct = 2
  density = 1
  expand = 3
  formula = G4_DNA_C
  name = G4_DNA_C
  specific = 4
FEATURE [App::DocumentObjectGroupPython] H_element137  label="H_element : 084"  # scripted group (container) (typed FeaturePython)
  n = 9
  ref = H_element
FEATURE [App::DocumentObjectGroupPython] C_element147  label="C_element : 092"  # scripted group (container) (typed FeaturePython)
  n = 9
  ref = C_element
FEATURE [App::DocumentObjectGroupPython] N_element067  label="N_element : 039"  # scripted group (container) (typed FeaturePython)
  n = 2
  ref = N_element
FEATURE [App::DocumentObjectGroupPython] O_element129  label="O_element : 9"  # scripted group (container) (typed FeaturePython)
  n = 9
  ref = O_element
FEATURE [App::DocumentObjectGroupPython] P_element018  label="P_element : 007"  # scripted group (container) (typed FeaturePython)
  n = 1
  ref = P_element
FEATURE [App::DocumentObjectGroupPython] G4_DNA_U  # scripted group (container) (typed FeaturePython)
  Dunit = g/cm3
  Dvalue = 1
  Group = -> [H_element137,C_element147,N_element067,O_element129,P_element018]
  conduct = 2
  density = 1
  expand = 3
  formula = G4_DNA_U
  name = G4_DNA_U
  specific = 4
FEATURE [App::DocumentObjectGroupPython] H_element138  label="H_element : 085"  # scripted group (container) (typed FeaturePython)
  n = 11
  ref = H_element
FEATURE [App::DocumentObjectGroupPython] C_element148  label="C_element : 093"  # scripted group (container) (typed FeaturePython)
  n = 10
  ref = C_element
FEATURE [App::DocumentObjectGroupPython] N_element068  label="N_element : 040"  # scripted group (container) (typed FeaturePython)
  n = 2
  ref = N_element
FEATURE [App::DocumentObjectGroupPython] O_element130  label="O_element : 081"  # scripted group (container) (typed FeaturePython)
  n = 9
  ref = O_element
FEATURE [App::DocumentObjectGroupPython] P_element019  label="P_element : 008"  # scripted group (container) (typed FeaturePython)
  n = 1
  ref = P_element
FEATURE [App::DocumentObjectGroupPython] G4_DNA_MU  # scripted group (container) (typed FeaturePython)
  Dunit = g/cm3
  Dvalue = 1
  Group = -> [H_element138,C_element148,N_element068,O_element130,P_element019]
  conduct = 2
  density = 1
  expand = 3
  formula = G4_DNA_MU
  name = G4_DNA_MU
  specific = 4
FEATURE [App::DocumentObjectGroupPython] BioChemical  # scripted group (container) (typed FeaturePython)
  Group = -> [G4_CYTOSINE,G4_THYMINE,G4_URACIL,G4_DNA_ADENINE,G4_DNA_GUANINE,G4_DNA_CYTOSINE,G4_DNA_THYMINE,G4_DNA_URACIL,G4_DNA_ADENOSINE,G4_DNA_GUANOSINE,G4_DNA_CYTIDINE,G4_DNA_URIDINE,G4_DNA_METHYLURIDINE,G4_DNA_MONOPHOSPHATE,G4_DNA_A,G4_DNA_G,G4_DNA_C,G4_DNA_U,G4_DNA_MU]
FEATURE [App::DocumentObjectGroupPython] G4Materials  # scripted group (container) (typed FeaturePython)
  Group = -> [NIST,Element,HEP,Space,BioChemical]
  version = 1
FEATURE [App::DocumentObjectGroupPython] Geant4  # scripted group (container) (typed FeaturePython)
  Group = -> [G4Isotopes,G4Elements,G4Materials]
FEATURE [App::DocumentObjectGroupPython] Materials  # scripted group (container) (typed FeaturePython)
  Group = -> [Geant4]
FEATURE [Part::FeaturePython] GDMLBox_WorldBox  # WARN: FeaturePython — macro-defined, semantics opaque (R4)
  lunit = 2
  material = 5
  x = 200
  y = 200
  z = 200
FEATURE [Sketcher::SketchObject] Sketch
  FullyConstrained = false
  Placement = pos=(0,0,0) rot=(1,0,0;1.5708rad)
  sketch-geometry (29):
    g0: LineSegment StartX=40 StartY=9.87547 StartZ=0 EndX=60 EndY=9.87547 EndZ=0
    g1: LineSegment StartX=60 StartY=9.87547 StartZ=0 EndX=60 EndY=-10.1245 EndZ=0
    g2: LineSegment StartX=60 StartY=-10.1245 StartZ=0 EndX=40 EndY=-10.1245 EndZ=0
    g3: LineSegment StartX=40 StartY=-10.1245 StartZ=0 EndX=40 EndY=9.87547 EndZ=0
    g4-g16: Circle x13 (B-spline internal-alignment scaffolding for g17; pole/knot coordinates omitted)
    g17: BSplineCurve PolesCount=13 KnotsCount=11 Degree=3 IsPeriodic=0
    g18-g28: GeomPoint x11 (B-spline internal-alignment scaffolding for g17; pole/knot coordinates omitted)
  constraints (13):
    c: Coincident(g0,g1)
    c: Coincident(g1,g2)
    c: Coincident(g2,g3)
    c: Coincident(g3,g0)
    c: Horizontal(g0)
    c: Horizontal(g2)
    c: Vertical(g1)
    c: Vertical(g3)
    c: Weight(g4) = 1
    c: Equal(g4, g5-g16) x12
    c: InternalAlignment(g4-g16 -> g17) x13
    c: InternalAlignment(g18-g28 -> g17) x11
    c: Coincident(g17,g17)
FEATURE [Part::Revolution] Revolve
  Angle = 180
  Axis = (0,0,1)
  Base = (0,0,0)
  FaceMakerClass = Part::FaceMakerBullseye
  Solid = true
  Source = -> Sketch
  Symmetric = false
  material = 6
FEATURE [App::Part] Part
  Group = -> [Sketch,Revolve]
  Origin = -> Origin001
FEATURE [App::Part] worldVOL
  Group = -> [GDMLBox_WorldBox,Part]
  Origin = -> Origin
